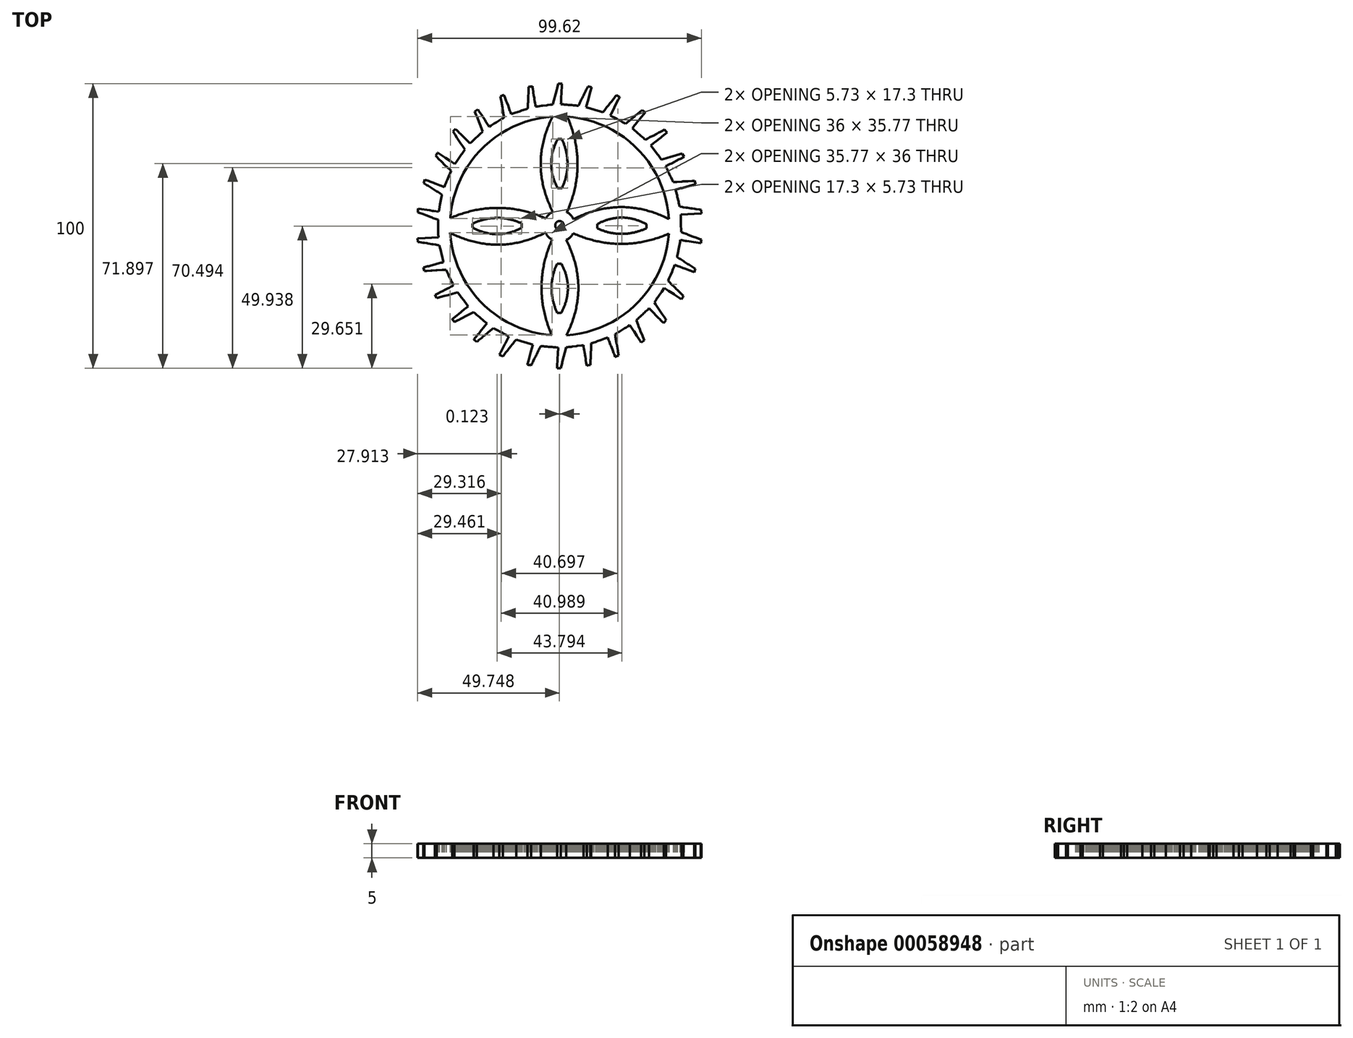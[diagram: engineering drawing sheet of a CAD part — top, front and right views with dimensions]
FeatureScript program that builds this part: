
annotation { "Feature Type Name" : "Feature", "Feature Type Description" : "" }
export const myFeature = defineFeature(function(context is Context, id is Id, definition is map)
    precondition{}
    {
        {
            var Q0;
            Q0=qCreatedBy(makeId("Top.planeOp"),FACE);
            var sketch = newSketch(context, id + "F0", { "sketchPlane" : qUnion([Q0])});
            skLineSegment(sketch, "E0", {"start": v(-36.57, 34.1) * mm, "end": v(-36.87, 33.77) * mm});
            skLineSegment(sketch, "E1", {"start": v(-36.87, 33.77) * mm, "end": v(-37.17, 33.44) * mm});
            skLineSegment(sketch, "E2", {"start": v(-37.17, 33.44) * mm, "end": v(-37.45, 33.13) * mm});
            skLineSegment(sketch, "E3", {"start": v(-37.45, 33.13) * mm, "end": v(-37.2, 32.76) * mm});
            skLineSegment(sketch, "E4", {"start": v(-37.2, 32.76) * mm, "end": v(-36.95, 32.39) * mm});
            skLineSegment(sketch, "E5", {"start": v(-36.95, 32.39) * mm, "end": v(-36.7, 32.02) * mm});
            skLineSegment(sketch, "E6", {"start": v(-36.7, 32.02) * mm, "end": v(-36.46, 31.65) * mm});
            skLineSegment(sketch, "E7", {"start": v(-36.46, 31.65) * mm, "end": v(-36.21, 31.28) * mm});
            skLineSegment(sketch, "E8", {"start": v(-36.21, 31.28) * mm, "end": v(-35.97, 30.9) * mm});
            skLineSegment(sketch, "E9", {"start": v(-35.97, 30.9) * mm, "end": v(-35.72, 30.53) * mm});
            skLineSegment(sketch, "E10", {"start": v(-35.72, 30.53) * mm, "end": v(-35.47, 30.16) * mm});
            skLineSegment(sketch, "E11", {"start": v(-35.47, 30.16) * mm, "end": v(-35.23, 29.8) * mm});
            skLineSegment(sketch, "E12", {"start": v(-35.23, 29.8) * mm, "end": v(-34.98, 29.42) * mm});
            skLineSegment(sketch, "E13", {"start": v(-34.98, 29.42) * mm, "end": v(-34.74, 29.05) * mm});
            skLineSegment(sketch, "E14", {"start": v(-34.74, 29.05) * mm, "end": v(-34.49, 28.68) * mm});
            skLineSegment(sketch, "E15", {"start": v(-34.49, 28.68) * mm, "end": v(-34.24, 28.3) * mm});
            skLineSegment(sketch, "E16", {"start": v(-34.24, 28.3) * mm, "end": v(-34, 27.93) * mm});
            skLineSegment(sketch, "E17", {"start": v(-34, 27.93) * mm, "end": v(-33.75, 27.56) * mm});
            skLineSegment(sketch, "E18", {"start": v(-33.75, 27.56) * mm, "end": v(-33.5, 27.2) * mm});
            skLineSegment(sketch, "E19", {"start": v(-33.5, 27.2) * mm, "end": v(-33.26, 26.83) * mm});
            skLineSegment(sketch, "E20", {"start": v(-33.26, 26.83) * mm, "end": v(-33.51, 26.46) * mm});
            skLineSegment(sketch, "E21", {"start": v(-33.51, 26.46) * mm, "end": v(-33.77, 26.1) * mm});
            skLineSegment(sketch, "E22", {"start": v(-33.77, 26.1) * mm, "end": v(-34.02, 25.73) * mm});
            skLineSegment(sketch, "E23", {"start": v(-34.02, 25.73) * mm, "end": v(-34.28, 25.37) * mm});
            skLineSegment(sketch, "E24", {"start": v(-34.28, 25.37) * mm, "end": v(-34.53, 25) * mm});
            skLineSegment(sketch, "E25", {"start": v(-34.53, 25) * mm, "end": v(-34.79, 24.63) * mm});
            skLineSegment(sketch, "E26", {"start": v(-34.79, 24.63) * mm, "end": v(-35.04, 24.27) * mm});
            skLineSegment(sketch, "E27", {"start": v(-35.04, 24.27) * mm, "end": v(-35.3, 23.9) * mm});
            skLineSegment(sketch, "E28", {"start": v(-35.3, 23.9) * mm, "end": v(-35.55, 23.53) * mm});
            skLineSegment(sketch, "E29", {"start": v(-35.55, 23.53) * mm, "end": v(-35.8, 23.17) * mm});
            skLineSegment(sketch, "E30", {"start": v(-35.8, 23.17) * mm, "end": v(-36.06, 22.8) * mm});
            skLineSegment(sketch, "E31", {"start": v(-36.06, 22.8) * mm, "end": v(-36.31, 22.44) * mm});
            skLineSegment(sketch, "E32", {"start": v(-36.31, 22.44) * mm, "end": v(-36.56, 22.07) * mm});
            skLineSegment(sketch, "E33", {"start": v(-36.56, 22.07) * mm, "end": v(-36.76, 21.8) * mm});
            skLineSegment(sketch, "E34", {"start": v(-36.76, 21.8) * mm, "end": v(-37.13, 22.03) * mm});
            skLineSegment(sketch, "E35", {"start": v(-37.13, 22.03) * mm, "end": v(-37.5, 22.28) * mm});
            skLineSegment(sketch, "E36", {"start": v(-37.5, 22.28) * mm, "end": v(-37.88, 22.52) * mm});
            skLineSegment(sketch, "E37", {"start": v(-37.88, 22.52) * mm, "end": v(-38.25, 22.76) * mm});
            skLineSegment(sketch, "E38", {"start": v(-38.25, 22.76) * mm, "end": v(-38.63, 23) * mm});
            skLineSegment(sketch, "E39", {"start": v(-38.63, 23) * mm, "end": v(-39, 23.25) * mm});
            skLineSegment(sketch, "E40", {"start": v(-39, 23.25) * mm, "end": v(-39.38, 23.49) * mm});
            skLineSegment(sketch, "E41", {"start": v(-39.38, 23.49) * mm, "end": v(-39.75, 23.73) * mm});
            skLineSegment(sketch, "E42", {"start": v(-39.75, 23.73) * mm, "end": v(-40.12, 23.98) * mm});
            skLineSegment(sketch, "E43", {"start": v(-40.12, 23.98) * mm, "end": v(-40.5, 24.22) * mm});
            skLineSegment(sketch, "E44", {"start": v(-40.5, 24.22) * mm, "end": v(-40.87, 24.46) * mm});
            skLineSegment(sketch, "E45", {"start": v(-40.87, 24.46) * mm, "end": v(-41.24, 24.7) * mm});
            skLineSegment(sketch, "E46", {"start": v(-41.24, 24.7) * mm, "end": v(-41.62, 24.95) * mm});
            skLineSegment(sketch, "E47", {"start": v(-41.62, 24.95) * mm, "end": v(-42, 25.19) * mm});
            skLineSegment(sketch, "E48", {"start": v(-42, 25.19) * mm, "end": v(-42.37, 25.43) * mm});
            skLineSegment(sketch, "E49", {"start": v(-42.37, 25.43) * mm, "end": v(-42.74, 25.67) * mm});
            skLineSegment(sketch, "E50", {"start": v(-42.74, 25.67) * mm, "end": v(-42.86, 25.75) * mm});
            skLineSegment(sketch, "E51", {"start": v(-42.86, 25.75) * mm, "end": v(-43.08, 25.37) * mm});
            skLineSegment(sketch, "E52", {"start": v(-43.08, 25.37) * mm, "end": v(-43.3, 24.98) * mm});
            skLineSegment(sketch, "E53", {"start": v(-43.3, 24.98) * mm, "end": v(-43.52, 24.62) * mm});
            skLineSegment(sketch, "E54", {"start": v(-43.52, 24.62) * mm, "end": v(-43.2, 24.3) * mm});
            skLineSegment(sketch, "E55", {"start": v(-43.2, 24.3) * mm, "end": v(-42.88, 24) * mm});
            skLineSegment(sketch, "E56", {"start": v(-42.88, 24) * mm, "end": v(-42.56, 23.69) * mm});
            skLineSegment(sketch, "E57", {"start": v(-42.56, 23.69) * mm, "end": v(-42.24, 23.37) * mm});
            skLineSegment(sketch, "E58", {"start": v(-42.24, 23.37) * mm, "end": v(-41.93, 23.06) * mm});
            skLineSegment(sketch, "E59", {"start": v(-41.93, 23.06) * mm, "end": v(-41.6, 22.75) * mm});
            skLineSegment(sketch, "E60", {"start": v(-41.6, 22.75) * mm, "end": v(-41.29, 22.44) * mm});
            skLineSegment(sketch, "E61", {"start": v(-41.29, 22.44) * mm, "end": v(-40.97, 22.13) * mm});
            skLineSegment(sketch, "E62", {"start": v(-40.97, 22.13) * mm, "end": v(-40.65, 21.82) * mm});
            skLineSegment(sketch, "E63", {"start": v(-40.65, 21.82) * mm, "end": v(-40.33, 21.5) * mm});
            skLineSegment(sketch, "E64", {"start": v(-40.33, 21.5) * mm, "end": v(-40.02, 21.2) * mm});
            skLineSegment(sketch, "E65", {"start": v(-40.02, 21.2) * mm, "end": v(-39.7, 20.88) * mm});
            skLineSegment(sketch, "E66", {"start": v(-39.7, 20.88) * mm, "end": v(-39.38, 20.57) * mm});
            skLineSegment(sketch, "E67", {"start": v(-39.38, 20.57) * mm, "end": v(-39.06, 20.26) * mm});
            skLineSegment(sketch, "E68", {"start": v(-39.06, 20.26) * mm, "end": v(-38.74, 19.94) * mm});
            skLineSegment(sketch, "E69", {"start": v(-38.74, 19.94) * mm, "end": v(-38.42, 19.63) * mm});
            skLineSegment(sketch, "E70", {"start": v(-38.42, 19.63) * mm, "end": v(-38.11, 19.33) * mm});
            skLineSegment(sketch, "E71", {"start": v(-38.11, 19.33) * mm, "end": v(-38.28, 18.92) * mm});
            skLineSegment(sketch, "E72", {"start": v(-38.28, 18.92) * mm, "end": v(-38.46, 18.5) * mm});
            skLineSegment(sketch, "E73", {"start": v(-38.46, 18.5) * mm, "end": v(-38.63, 18.1) * mm});
            skLineSegment(sketch, "E74", {"start": v(-38.63, 18.1) * mm, "end": v(-38.8, 17.68) * mm});
            skLineSegment(sketch, "E75", {"start": v(-38.8, 17.68) * mm, "end": v(-38.97, 17.27) * mm});
            skLineSegment(sketch, "E76", {"start": v(-38.97, 17.27) * mm, "end": v(-39.15, 16.86) * mm});
            skLineSegment(sketch, "E77", {"start": v(-39.15, 16.86) * mm, "end": v(-39.32, 16.45) * mm});
            skLineSegment(sketch, "E78", {"start": v(-39.32, 16.45) * mm, "end": v(-39.5, 16.04) * mm});
            skLineSegment(sketch, "E79", {"start": v(-39.5, 16.04) * mm, "end": v(-39.66, 15.63) * mm});
            skLineSegment(sketch, "E80", {"start": v(-39.66, 15.63) * mm, "end": v(-39.84, 15.22) * mm});
            skLineSegment(sketch, "E81", {"start": v(-39.84, 15.22) * mm, "end": v(-40, 14.8) * mm});
            skLineSegment(sketch, "E82", {"start": v(-40, 14.8) * mm, "end": v(-40.18, 14.4) * mm});
            skLineSegment(sketch, "E83", {"start": v(-40.18, 14.4) * mm, "end": v(-40.35, 13.99) * mm});
            skLineSegment(sketch, "E84", {"start": v(-40.35, 13.99) * mm, "end": v(-40.49, 13.67) * mm});
            skLineSegment(sketch, "E85", {"start": v(-40.49, 13.67) * mm, "end": v(-40.9, 13.83) * mm});
            skLineSegment(sketch, "E86", {"start": v(-40.9, 13.83) * mm, "end": v(-41.32, 14) * mm});
            skLineSegment(sketch, "E87", {"start": v(-41.32, 14) * mm, "end": v(-41.73, 14.15) * mm});
            skLineSegment(sketch, "E88", {"start": v(-41.73, 14.15) * mm, "end": v(-42.15, 14.31) * mm});
            skLineSegment(sketch, "E89", {"start": v(-42.15, 14.31) * mm, "end": v(-42.57, 14.47) * mm});
            skLineSegment(sketch, "E90", {"start": v(-42.57, 14.47) * mm, "end": v(-42.98, 14.63) * mm});
            skLineSegment(sketch, "E91", {"start": v(-42.98, 14.63) * mm, "end": v(-43.4, 14.8) * mm});
            skLineSegment(sketch, "E92", {"start": v(-43.4, 14.8) * mm, "end": v(-43.81, 14.95) * mm});
            skLineSegment(sketch, "E93", {"start": v(-43.81, 14.95) * mm, "end": v(-44.23, 15.1) * mm});
            skLineSegment(sketch, "E94", {"start": v(-44.23, 15.1) * mm, "end": v(-44.65, 15.27) * mm});
            skLineSegment(sketch, "E95", {"start": v(-44.65, 15.27) * mm, "end": v(-45.06, 15.43) * mm});
            skLineSegment(sketch, "E96", {"start": v(-45.06, 15.43) * mm, "end": v(-45.48, 15.59) * mm});
            skLineSegment(sketch, "E97", {"start": v(-45.48, 15.59) * mm, "end": v(-45.9, 15.75) * mm});
            skLineSegment(sketch, "E98", {"start": v(-45.9, 15.75) * mm, "end": v(-46.31, 15.9) * mm});
            skLineSegment(sketch, "E99", {"start": v(-46.31, 15.9) * mm, "end": v(-46.73, 16.07) * mm});
            skLineSegment(sketch, "E100", {"start": v(-46.73, 16.07) * mm, "end": v(-47.14, 16.23) * mm});
            skLineSegment(sketch, "E101", {"start": v(-47.14, 16.23) * mm, "end": v(-47.28, 16.28) * mm});
            skLineSegment(sketch, "E102", {"start": v(-47.28, 16.28) * mm, "end": v(-47.42, 15.86) * mm});
            skLineSegment(sketch, "E103", {"start": v(-47.42, 15.86) * mm, "end": v(-47.56, 15.43) * mm});
            skLineSegment(sketch, "E104", {"start": v(-47.56, 15.43) * mm, "end": v(-47.69, 15.04) * mm});
            skLineSegment(sketch, "E105", {"start": v(-47.69, 15.04) * mm, "end": v(-47.3, 14.8) * mm});
            skLineSegment(sketch, "E106", {"start": v(-47.3, 14.8) * mm, "end": v(-46.93, 14.56) * mm});
            skLineSegment(sketch, "E107", {"start": v(-46.93, 14.56) * mm, "end": v(-46.56, 14.32) * mm});
            skLineSegment(sketch, "E108", {"start": v(-46.56, 14.32) * mm, "end": v(-46.18, 14.08) * mm});
            skLineSegment(sketch, "E109", {"start": v(-46.18, 14.08) * mm, "end": v(-45.8, 13.84) * mm});
            skLineSegment(sketch, "E110", {"start": v(-45.8, 13.84) * mm, "end": v(-45.43, 13.6) * mm});
            skLineSegment(sketch, "E111", {"start": v(-45.43, 13.6) * mm, "end": v(-45.05, 13.36) * mm});
            skLineSegment(sketch, "E112", {"start": v(-45.05, 13.36) * mm, "end": v(-44.68, 13.13) * mm});
            skLineSegment(sketch, "E113", {"start": v(-44.68, 13.13) * mm, "end": v(-44.3, 12.89) * mm});
            skLineSegment(sketch, "E114", {"start": v(-44.3, 12.89) * mm, "end": v(-43.92, 12.65) * mm});
            skLineSegment(sketch, "E115", {"start": v(-43.92, 12.65) * mm, "end": v(-43.55, 12.4) * mm});
            skLineSegment(sketch, "E116", {"start": v(-43.55, 12.4) * mm, "end": v(-43.17, 12.17) * mm});
            skLineSegment(sketch, "E117", {"start": v(-43.17, 12.17) * mm, "end": v(-42.8, 11.93) * mm});
            skLineSegment(sketch, "E118", {"start": v(-42.8, 11.93) * mm, "end": v(-42.42, 11.7) * mm});
            skLineSegment(sketch, "E119", {"start": v(-42.42, 11.7) * mm, "end": v(-42.04, 11.45) * mm});
            skLineSegment(sketch, "E120", {"start": v(-42.04, 11.45) * mm, "end": v(-41.67, 11.22) * mm});
            skLineSegment(sketch, "E121", {"start": v(-41.67, 11.22) * mm, "end": v(-41.3, 10.98) * mm});
            skLineSegment(sketch, "E122", {"start": v(-41.3, 10.98) * mm, "end": v(-41.38, 10.54) * mm});
            skLineSegment(sketch, "E123", {"start": v(-41.38, 10.54) * mm, "end": v(-41.46, 10.1) * mm});
            skLineSegment(sketch, "E124", {"start": v(-41.46, 10.1) * mm, "end": v(-41.55, 9.67) * mm});
            skLineSegment(sketch, "E125", {"start": v(-41.55, 9.67) * mm, "end": v(-41.63, 9.23) * mm});
            skLineSegment(sketch, "E126", {"start": v(-41.63, 9.23) * mm, "end": v(-41.71, 8.8) * mm});
            skLineSegment(sketch, "E127", {"start": v(-41.71, 8.8) * mm, "end": v(-41.8, 8.35) * mm});
            skLineSegment(sketch, "E128", {"start": v(-41.8, 8.35) * mm, "end": v(-41.88, 7.92) * mm});
            skLineSegment(sketch, "E129", {"start": v(-41.88, 7.92) * mm, "end": v(-41.96, 7.48) * mm});
            skLineSegment(sketch, "E130", {"start": v(-41.96, 7.48) * mm, "end": v(-42.05, 7.04) * mm});
            skLineSegment(sketch, "E131", {"start": v(-42.05, 7.04) * mm, "end": v(-42.13, 6.6) * mm});
            skLineSegment(sketch, "E132", {"start": v(-42.13, 6.6) * mm, "end": v(-42.21, 6.17) * mm});
            skLineSegment(sketch, "E133", {"start": v(-42.21, 6.17) * mm, "end": v(-42.3, 5.73) * mm});
            skLineSegment(sketch, "E134", {"start": v(-42.3, 5.73) * mm, "end": v(-42.38, 5.3) * mm});
            skLineSegment(sketch, "E135", {"start": v(-42.38, 5.3) * mm, "end": v(-42.44, 4.96) * mm});
            skLineSegment(sketch, "E136", {"start": v(-42.44, 4.96) * mm, "end": v(-42.88, 5.03) * mm});
            skLineSegment(sketch, "E137", {"start": v(-42.88, 5.03) * mm, "end": v(-43.32, 5.1) * mm});
            skLineSegment(sketch, "E138", {"start": v(-43.32, 5.1) * mm, "end": v(-43.76, 5.16) * mm});
            skLineSegment(sketch, "E139", {"start": v(-43.76, 5.16) * mm, "end": v(-44.2, 5.23) * mm});
            skLineSegment(sketch, "E140", {"start": v(-44.2, 5.23) * mm, "end": v(-44.65, 5.3) * mm});
            skLineSegment(sketch, "E141", {"start": v(-44.65, 5.3) * mm, "end": v(-45.09, 5.37) * mm});
            skLineSegment(sketch, "E142", {"start": v(-45.09, 5.37) * mm, "end": v(-45.53, 5.44) * mm});
            skLineSegment(sketch, "E143", {"start": v(-45.53, 5.44) * mm, "end": v(-45.97, 5.51) * mm});
            skLineSegment(sketch, "E144", {"start": v(-45.97, 5.51) * mm, "end": v(-46.4, 5.58) * mm});
            skLineSegment(sketch, "E145", {"start": v(-46.4, 5.58) * mm, "end": v(-46.85, 5.65) * mm});
            skLineSegment(sketch, "E146", {"start": v(-46.85, 5.65) * mm, "end": v(-47.29, 5.72) * mm});
            skLineSegment(sketch, "E147", {"start": v(-47.29, 5.72) * mm, "end": v(-47.73, 5.8) * mm});
            skLineSegment(sketch, "E148", {"start": v(-47.73, 5.8) * mm, "end": v(-48.17, 5.86) * mm});
            skLineSegment(sketch, "E149", {"start": v(-48.17, 5.86) * mm, "end": v(-48.6, 5.93) * mm});
            skLineSegment(sketch, "E150", {"start": v(-48.6, 5.93) * mm, "end": v(-49.05, 6) * mm});
            skLineSegment(sketch, "E151", {"start": v(-49.05, 6) * mm, "end": v(-49.49, 6.07) * mm});
            skLineSegment(sketch, "E152", {"start": v(-49.49, 6.07) * mm, "end": v(-49.63, 6.1) * mm});
            skLineSegment(sketch, "E153", {"start": v(-49.63, 6.1) * mm, "end": v(-49.68, 5.65) * mm});
            skLineSegment(sketch, "E154", {"start": v(-49.68, 5.65) * mm, "end": v(-49.72, 5.2) * mm});
            skLineSegment(sketch, "E155", {"start": v(-49.72, 5.2) * mm, "end": v(-49.77, 4.8) * mm});
            skLineSegment(sketch, "E156", {"start": v(-49.77, 4.8) * mm, "end": v(-49.35, 4.64) * mm});
            skLineSegment(sketch, "E157", {"start": v(-49.35, 4.64) * mm, "end": v(-48.93, 4.48) * mm});
            skLineSegment(sketch, "E158", {"start": v(-48.93, 4.48) * mm, "end": v(-48.52, 4.33) * mm});
            skLineSegment(sketch, "E159", {"start": v(-48.52, 4.33) * mm, "end": v(-48.1, 4.17) * mm});
            skLineSegment(sketch, "E160", {"start": v(-48.1, 4.17) * mm, "end": v(-47.68, 4.02) * mm});
            skLineSegment(sketch, "E161", {"start": v(-47.68, 4.02) * mm, "end": v(-47.26, 3.86) * mm});
            skLineSegment(sketch, "E162", {"start": v(-47.26, 3.86) * mm, "end": v(-46.85, 3.7) * mm});
            skLineSegment(sketch, "E163", {"start": v(-46.85, 3.7) * mm, "end": v(-46.43, 3.55) * mm});
            skLineSegment(sketch, "E164", {"start": v(-46.43, 3.55) * mm, "end": v(-46.01, 3.4) * mm});
            skLineSegment(sketch, "E165", {"start": v(-46.01, 3.4) * mm, "end": v(-45.6, 3.24) * mm});
            skLineSegment(sketch, "E166", {"start": v(-45.6, 3.24) * mm, "end": v(-45.18, 3.08) * mm});
            skLineSegment(sketch, "E167", {"start": v(-45.18, 3.08) * mm, "end": v(-44.76, 2.93) * mm});
            skLineSegment(sketch, "E168", {"start": v(-44.76, 2.93) * mm, "end": v(-44.34, 2.77) * mm});
            skLineSegment(sketch, "E169", {"start": v(-44.34, 2.77) * mm, "end": v(-43.92, 2.62) * mm});
            skLineSegment(sketch, "E170", {"start": v(-43.92, 2.62) * mm, "end": v(-43.5, 2.46) * mm});
            skLineSegment(sketch, "E171", {"start": v(-43.5, 2.46) * mm, "end": v(-43.09, 2.3) * mm});
            skLineSegment(sketch, "E172", {"start": v(-43.09, 2.3) * mm, "end": v(-42.68, 2.16) * mm});
            skLineSegment(sketch, "E173", {"start": v(-42.68, 2.16) * mm, "end": v(-42.67, 1.7) * mm});
            skLineSegment(sketch, "E174", {"start": v(-42.67, 1.7) * mm, "end": v(-42.66, 1.26) * mm});
            skLineSegment(sketch, "E175", {"start": v(-42.66, 1.26) * mm, "end": v(-42.65, 0.82) * mm});
            skLineSegment(sketch, "E176", {"start": v(-42.65, 0.82) * mm, "end": v(-42.64, 0.37) * mm});
            skLineSegment(sketch, "E177", {"start": v(-42.64, 0.37) * mm, "end": v(-42.63, -0.07) * mm});
            skLineSegment(sketch, "E178", {"start": v(-42.63, -0.07) * mm, "end": v(-42.62, -0.52) * mm});
            skLineSegment(sketch, "E179", {"start": v(-42.62, -0.52) * mm, "end": v(-42.61, -0.96) * mm});
            skLineSegment(sketch, "E180", {"start": v(-42.61, -0.96) * mm, "end": v(-42.6, -1.4) * mm});
            skLineSegment(sketch, "E181", {"start": v(-42.6, -1.4) * mm, "end": v(-42.6, -1.85) * mm});
            skLineSegment(sketch, "E182", {"start": v(-42.6, -1.85) * mm, "end": v(-42.58, -2.3) * mm});
            skLineSegment(sketch, "E183", {"start": v(-42.58, -2.3) * mm, "end": v(-42.57, -2.75) * mm});
            skLineSegment(sketch, "E184", {"start": v(-42.57, -2.75) * mm, "end": v(-42.56, -3.2) * mm});
            skLineSegment(sketch, "E185", {"start": v(-42.56, -3.2) * mm, "end": v(-42.55, -3.64) * mm});
            skLineSegment(sketch, "E186", {"start": v(-42.55, -3.64) * mm, "end": v(-42.55, -3.98) * mm});
            skLineSegment(sketch, "E187", {"start": v(-42.55, -3.98) * mm, "end": v(-43, -4) * mm});
            skLineSegment(sketch, "E188", {"start": v(-43, -4) * mm, "end": v(-43.44, -4.02) * mm});
            skLineSegment(sketch, "E189", {"start": v(-43.44, -4.02) * mm, "end": v(-43.88, -4.05) * mm});
            skLineSegment(sketch, "E190", {"start": v(-43.88, -4.05) * mm, "end": v(-44.33, -4.07) * mm});
            skLineSegment(sketch, "E191", {"start": v(-44.33, -4.07) * mm, "end": v(-44.77, -4.1) * mm});
            skLineSegment(sketch, "E192", {"start": v(-44.77, -4.1) * mm, "end": v(-45.22, -4.12) * mm});
            skLineSegment(sketch, "E193", {"start": v(-45.22, -4.12) * mm, "end": v(-45.66, -4.14) * mm});
            skLineSegment(sketch, "E194", {"start": v(-45.66, -4.14) * mm, "end": v(-46.1, -4.16) * mm});
            skLineSegment(sketch, "E195", {"start": v(-46.1, -4.16) * mm, "end": v(-46.55, -4.19) * mm});
            skLineSegment(sketch, "E196", {"start": v(-46.55, -4.19) * mm, "end": v(-47, -4.21) * mm});
            skLineSegment(sketch, "E197", {"start": v(-47, -4.21) * mm, "end": v(-47.44, -4.23) * mm});
            skLineSegment(sketch, "E198", {"start": v(-47.44, -4.23) * mm, "end": v(-47.89, -4.26) * mm});
            skLineSegment(sketch, "E199", {"start": v(-47.89, -4.26) * mm, "end": v(-48.33, -4.28) * mm});
            skLineSegment(sketch, "E200", {"start": v(-48.33, -4.28) * mm, "end": v(-48.78, -4.3) * mm});
            skLineSegment(sketch, "E201", {"start": v(-48.78, -4.3) * mm, "end": v(-49.22, -4.33) * mm});
            skLineSegment(sketch, "E202", {"start": v(-49.22, -4.33) * mm, "end": v(-49.67, -4.35) * mm});
            skLineSegment(sketch, "E203", {"start": v(-49.67, -4.35) * mm, "end": v(-49.8, -4.36) * mm});
            skLineSegment(sketch, "E204", {"start": v(-49.8, -4.36) * mm, "end": v(-49.77, -4.8) * mm});
            skLineSegment(sketch, "E205", {"start": v(-49.77, -4.8) * mm, "end": v(-49.72, -5.24) * mm});
            skLineSegment(sketch, "E206", {"start": v(-49.72, -5.24) * mm, "end": v(-49.68, -5.66) * mm});
            skLineSegment(sketch, "E207", {"start": v(-49.68, -5.66) * mm, "end": v(-49.24, -5.73) * mm});
            skLineSegment(sketch, "E208", {"start": v(-49.24, -5.73) * mm, "end": v(-48.8, -5.8) * mm});
            skLineSegment(sketch, "E209", {"start": v(-48.8, -5.8) * mm, "end": v(-48.36, -5.86) * mm});
            skLineSegment(sketch, "E210", {"start": v(-48.36, -5.86) * mm, "end": v(-47.92, -5.92) * mm});
            skLineSegment(sketch, "E211", {"start": v(-47.92, -5.92) * mm, "end": v(-47.47, -5.99) * mm});
            skLineSegment(sketch, "E212", {"start": v(-47.47, -5.99) * mm, "end": v(-47.03, -6.05) * mm});
            skLineSegment(sketch, "E213", {"start": v(-47.03, -6.05) * mm, "end": v(-46.6, -6.12) * mm});
            skLineSegment(sketch, "E214", {"start": v(-46.6, -6.12) * mm, "end": v(-46.15, -6.18) * mm});
            skLineSegment(sketch, "E215", {"start": v(-46.15, -6.18) * mm, "end": v(-45.71, -6.25) * mm});
            skLineSegment(sketch, "E216", {"start": v(-45.71, -6.25) * mm, "end": v(-45.27, -6.31) * mm});
            skLineSegment(sketch, "E217", {"start": v(-45.27, -6.31) * mm, "end": v(-44.83, -6.38) * mm});
            skLineSegment(sketch, "E218", {"start": v(-44.83, -6.38) * mm, "end": v(-44.39, -6.44) * mm});
            skLineSegment(sketch, "E219", {"start": v(-44.39, -6.44) * mm, "end": v(-43.95, -6.5) * mm});
            skLineSegment(sketch, "E220", {"start": v(-43.95, -6.5) * mm, "end": v(-43.5, -6.57) * mm});
            skLineSegment(sketch, "E221", {"start": v(-43.5, -6.57) * mm, "end": v(-43.07, -6.64) * mm});
            skLineSegment(sketch, "E222", {"start": v(-43.07, -6.64) * mm, "end": v(-42.63, -6.7) * mm});
            skLineSegment(sketch, "E223", {"start": v(-42.63, -6.7) * mm, "end": v(-42.2, -6.77) * mm});
            skLineSegment(sketch, "E224", {"start": v(-42.2, -6.77) * mm, "end": v(-42.1, -7.2) * mm});
            skLineSegment(sketch, "E225", {"start": v(-42.1, -7.2) * mm, "end": v(-41.99, -7.63) * mm});
            skLineSegment(sketch, "E226", {"start": v(-41.99, -7.63) * mm, "end": v(-41.89, -8.07) * mm});
            skLineSegment(sketch, "E227", {"start": v(-41.89, -8.07) * mm, "end": v(-41.79, -8.5) * mm});
            skLineSegment(sketch, "E228", {"start": v(-41.79, -8.5) * mm, "end": v(-41.68, -8.93) * mm});
            skLineSegment(sketch, "E229", {"start": v(-41.68, -8.93) * mm, "end": v(-41.58, -9.37) * mm});
            skLineSegment(sketch, "E230", {"start": v(-41.58, -9.37) * mm, "end": v(-41.48, -9.8) * mm});
            skLineSegment(sketch, "E231", {"start": v(-41.48, -9.8) * mm, "end": v(-41.38, -10.24) * mm});
            skLineSegment(sketch, "E232", {"start": v(-41.38, -10.24) * mm, "end": v(-41.28, -10.67) * mm});
            skLineSegment(sketch, "E233", {"start": v(-41.28, -10.67) * mm, "end": v(-41.17, -11.1) * mm});
            skLineSegment(sketch, "E234", {"start": v(-41.17, -11.1) * mm, "end": v(-41.07, -11.54) * mm});
            skLineSegment(sketch, "E235", {"start": v(-41.07, -11.54) * mm, "end": v(-40.97, -11.97) * mm});
            skLineSegment(sketch, "E236", {"start": v(-40.97, -11.97) * mm, "end": v(-40.87, -12.4) * mm});
            skLineSegment(sketch, "E237", {"start": v(-40.87, -12.4) * mm, "end": v(-40.8, -12.74) * mm});
            skLineSegment(sketch, "E238", {"start": v(-40.8, -12.74) * mm, "end": v(-41.22, -12.85) * mm});
            skLineSegment(sketch, "E239", {"start": v(-41.22, -12.85) * mm, "end": v(-41.65, -12.97) * mm});
            skLineSegment(sketch, "E240", {"start": v(-41.65, -12.97) * mm, "end": v(-42.08, -13.08) * mm});
            skLineSegment(sketch, "E241", {"start": v(-42.08, -13.08) * mm, "end": v(-42.51, -13.2) * mm});
            skLineSegment(sketch, "E242", {"start": v(-42.51, -13.2) * mm, "end": v(-42.94, -13.31) * mm});
            skLineSegment(sketch, "E243", {"start": v(-42.94, -13.31) * mm, "end": v(-43.37, -13.43) * mm});
            skLineSegment(sketch, "E244", {"start": v(-43.37, -13.43) * mm, "end": v(-43.8, -13.54) * mm});
            skLineSegment(sketch, "E245", {"start": v(-43.8, -13.54) * mm, "end": v(-44.23, -13.66) * mm});
            skLineSegment(sketch, "E246", {"start": v(-44.23, -13.66) * mm, "end": v(-44.66, -13.77) * mm});
            skLineSegment(sketch, "E247", {"start": v(-44.66, -13.77) * mm, "end": v(-45.1, -13.89) * mm});
            skLineSegment(sketch, "E248", {"start": v(-45.1, -13.89) * mm, "end": v(-45.53, -14) * mm});
            skLineSegment(sketch, "E249", {"start": v(-45.53, -14) * mm, "end": v(-45.96, -14.12) * mm});
            skLineSegment(sketch, "E250", {"start": v(-45.96, -14.12) * mm, "end": v(-46.39, -14.24) * mm});
            skLineSegment(sketch, "E251", {"start": v(-46.39, -14.24) * mm, "end": v(-46.82, -14.35) * mm});
            skLineSegment(sketch, "E252", {"start": v(-46.82, -14.35) * mm, "end": v(-47.25, -14.47) * mm});
            skLineSegment(sketch, "E253", {"start": v(-47.25, -14.47) * mm, "end": v(-47.68, -14.58) * mm});
            skLineSegment(sketch, "E254", {"start": v(-47.68, -14.58) * mm, "end": v(-47.82, -14.62) * mm});
            skLineSegment(sketch, "E255", {"start": v(-47.82, -14.62) * mm, "end": v(-47.68, -15.04) * mm});
            skLineSegment(sketch, "E256", {"start": v(-47.68, -15.04) * mm, "end": v(-47.54, -15.47) * mm});
            skLineSegment(sketch, "E257", {"start": v(-47.54, -15.47) * mm, "end": v(-47.42, -15.87) * mm});
            skLineSegment(sketch, "E258", {"start": v(-47.42, -15.87) * mm, "end": v(-46.97, -15.84) * mm});
            skLineSegment(sketch, "E259", {"start": v(-46.97, -15.84) * mm, "end": v(-46.53, -15.8) * mm});
            skLineSegment(sketch, "E260", {"start": v(-46.53, -15.8) * mm, "end": v(-46.08, -15.78) * mm});
            skLineSegment(sketch, "E261", {"start": v(-46.08, -15.78) * mm, "end": v(-45.64, -15.75) * mm});
            skLineSegment(sketch, "E262", {"start": v(-45.64, -15.75) * mm, "end": v(-45.2, -15.73) * mm});
            skLineSegment(sketch, "E263", {"start": v(-45.2, -15.73) * mm, "end": v(-44.75, -15.7) * mm});
            skLineSegment(sketch, "E264", {"start": v(-44.75, -15.7) * mm, "end": v(-44.3, -15.67) * mm});
            skLineSegment(sketch, "E265", {"start": v(-44.3, -15.67) * mm, "end": v(-43.86, -15.64) * mm});
            skLineSegment(sketch, "E266", {"start": v(-43.86, -15.64) * mm, "end": v(-43.41, -15.61) * mm});
            skLineSegment(sketch, "E267", {"start": v(-43.41, -15.61) * mm, "end": v(-42.97, -15.59) * mm});
            skLineSegment(sketch, "E268", {"start": v(-42.97, -15.59) * mm, "end": v(-42.52, -15.56) * mm});
            skLineSegment(sketch, "E269", {"start": v(-42.52, -15.56) * mm, "end": v(-42.08, -15.53) * mm});
            skLineSegment(sketch, "E270", {"start": v(-42.08, -15.53) * mm, "end": v(-41.63, -15.5) * mm});
            skLineSegment(sketch, "E271", {"start": v(-41.63, -15.5) * mm, "end": v(-41.19, -15.47) * mm});
            skLineSegment(sketch, "E272", {"start": v(-41.19, -15.47) * mm, "end": v(-40.75, -15.45) * mm});
            skLineSegment(sketch, "E273", {"start": v(-40.75, -15.45) * mm, "end": v(-40.3, -15.42) * mm});
            skLineSegment(sketch, "E274", {"start": v(-40.3, -15.42) * mm, "end": v(-39.87, -15.39) * mm});
            skLineSegment(sketch, "E275", {"start": v(-39.87, -15.39) * mm, "end": v(-39.68, -15.8) * mm});
            skLineSegment(sketch, "E276", {"start": v(-39.68, -15.8) * mm, "end": v(-39.49, -16.2) * mm});
            skLineSegment(sketch, "E277", {"start": v(-39.49, -16.2) * mm, "end": v(-39.3, -16.6) * mm});
            skLineSegment(sketch, "E278", {"start": v(-39.3, -16.6) * mm, "end": v(-39.1, -17) * mm});
            skLineSegment(sketch, "E279", {"start": v(-39.1, -17) * mm, "end": v(-38.92, -17.4) * mm});
            skLineSegment(sketch, "E280", {"start": v(-38.92, -17.4) * mm, "end": v(-38.73, -17.8) * mm});
            skLineSegment(sketch, "E281", {"start": v(-38.73, -17.8) * mm, "end": v(-38.54, -18.21) * mm});
            skLineSegment(sketch, "E282", {"start": v(-38.54, -18.21) * mm, "end": v(-38.35, -18.61) * mm});
            skLineSegment(sketch, "E283", {"start": v(-38.35, -18.61) * mm, "end": v(-38.16, -19.02) * mm});
            skLineSegment(sketch, "E284", {"start": v(-38.16, -19.02) * mm, "end": v(-37.97, -19.42) * mm});
            skLineSegment(sketch, "E285", {"start": v(-37.97, -19.42) * mm, "end": v(-37.78, -19.82) * mm});
            skLineSegment(sketch, "E286", {"start": v(-37.78, -19.82) * mm, "end": v(-37.59, -20.23) * mm});
            skLineSegment(sketch, "E287", {"start": v(-37.59, -20.23) * mm, "end": v(-37.4, -20.63) * mm});
            skLineSegment(sketch, "E288", {"start": v(-37.4, -20.63) * mm, "end": v(-37.25, -20.94) * mm});
            skLineSegment(sketch, "E289", {"start": v(-37.25, -20.94) * mm, "end": v(-37.65, -21.14) * mm});
            skLineSegment(sketch, "E290", {"start": v(-37.65, -21.14) * mm, "end": v(-38.05, -21.34) * mm});
            skLineSegment(sketch, "E291", {"start": v(-38.05, -21.34) * mm, "end": v(-38.44, -21.55) * mm});
            skLineSegment(sketch, "E292", {"start": v(-38.44, -21.55) * mm, "end": v(-38.84, -21.75) * mm});
            skLineSegment(sketch, "E293", {"start": v(-38.84, -21.75) * mm, "end": v(-39.24, -21.95) * mm});
            skLineSegment(sketch, "E294", {"start": v(-39.24, -21.95) * mm, "end": v(-39.63, -22.15) * mm});
            skLineSegment(sketch, "E295", {"start": v(-39.63, -22.15) * mm, "end": v(-40.03, -22.35) * mm});
            skLineSegment(sketch, "E296", {"start": v(-40.03, -22.35) * mm, "end": v(-40.43, -22.56) * mm});
            skLineSegment(sketch, "E297", {"start": v(-40.43, -22.56) * mm, "end": v(-40.82, -22.76) * mm});
            skLineSegment(sketch, "E298", {"start": v(-40.82, -22.76) * mm, "end": v(-41.22, -22.96) * mm});
            skLineSegment(sketch, "E299", {"start": v(-41.22, -22.96) * mm, "end": v(-41.62, -23.16) * mm});
            skLineSegment(sketch, "E300", {"start": v(-41.62, -23.16) * mm, "end": v(-42.02, -23.37) * mm});
            skLineSegment(sketch, "E301", {"start": v(-42.02, -23.37) * mm, "end": v(-42.41, -23.57) * mm});
            skLineSegment(sketch, "E302", {"start": v(-42.41, -23.57) * mm, "end": v(-42.8, -23.77) * mm});
            skLineSegment(sketch, "E303", {"start": v(-42.8, -23.77) * mm, "end": v(-43.2, -23.97) * mm});
            skLineSegment(sketch, "E304", {"start": v(-43.2, -23.97) * mm, "end": v(-43.6, -24.18) * mm});
            skLineSegment(sketch, "E305", {"start": v(-43.6, -24.18) * mm, "end": v(-43.73, -24.24) * mm});
            skLineSegment(sketch, "E306", {"start": v(-43.73, -24.24) * mm, "end": v(-43.5, -24.63) * mm});
            skLineSegment(sketch, "E307", {"start": v(-43.5, -24.63) * mm, "end": v(-43.29, -25.01) * mm});
            skLineSegment(sketch, "E308", {"start": v(-43.29, -25.01) * mm, "end": v(-43.08, -25.38) * mm});
            skLineSegment(sketch, "E309", {"start": v(-43.08, -25.38) * mm, "end": v(-42.65, -25.26) * mm});
            skLineSegment(sketch, "E310", {"start": v(-42.65, -25.26) * mm, "end": v(-42.22, -25.14) * mm});
            skLineSegment(sketch, "E311", {"start": v(-42.22, -25.14) * mm, "end": v(-41.8, -25.02) * mm});
            skLineSegment(sketch, "E312", {"start": v(-41.8, -25.02) * mm, "end": v(-41.36, -24.9) * mm});
            skLineSegment(sketch, "E313", {"start": v(-41.36, -24.9) * mm, "end": v(-40.94, -24.78) * mm});
            skLineSegment(sketch, "E314", {"start": v(-40.94, -24.78) * mm, "end": v(-40.5, -24.66) * mm});
            skLineSegment(sketch, "E315", {"start": v(-40.5, -24.66) * mm, "end": v(-40.08, -24.54) * mm});
            skLineSegment(sketch, "E316", {"start": v(-40.08, -24.54) * mm, "end": v(-39.65, -24.42) * mm});
            skLineSegment(sketch, "E317", {"start": v(-39.65, -24.42) * mm, "end": v(-39.22, -24.3) * mm});
            skLineSegment(sketch, "E318", {"start": v(-39.22, -24.3) * mm, "end": v(-38.79, -24.18) * mm});
            skLineSegment(sketch, "E319", {"start": v(-38.79, -24.18) * mm, "end": v(-38.36, -24.06) * mm});
            skLineSegment(sketch, "E320", {"start": v(-38.36, -24.06) * mm, "end": v(-37.93, -23.94) * mm});
            skLineSegment(sketch, "E321", {"start": v(-37.93, -23.94) * mm, "end": v(-37.5, -23.82) * mm});
            skLineSegment(sketch, "E322", {"start": v(-37.5, -23.82) * mm, "end": v(-37.07, -23.7) * mm});
            skLineSegment(sketch, "E323", {"start": v(-37.07, -23.7) * mm, "end": v(-36.64, -23.58) * mm});
            skLineSegment(sketch, "E324", {"start": v(-36.64, -23.58) * mm, "end": v(-36.21, -23.46) * mm});
            skLineSegment(sketch, "E325", {"start": v(-36.21, -23.46) * mm, "end": v(-35.8, -23.34) * mm});
            skLineSegment(sketch, "E326", {"start": v(-35.8, -23.34) * mm, "end": v(-35.52, -23.7) * mm});
            skLineSegment(sketch, "E327", {"start": v(-35.52, -23.7) * mm, "end": v(-35.26, -24.05) * mm});
            skLineSegment(sketch, "E328", {"start": v(-35.26, -24.05) * mm, "end": v(-34.99, -24.4) * mm});
            skLineSegment(sketch, "E329", {"start": v(-34.99, -24.4) * mm, "end": v(-34.72, -24.76) * mm});
            skLineSegment(sketch, "E330", {"start": v(-34.72, -24.76) * mm, "end": v(-34.45, -25.12) * mm});
            skLineSegment(sketch, "E331", {"start": v(-34.45, -25.12) * mm, "end": v(-34.18, -25.47) * mm});
            skLineSegment(sketch, "E332", {"start": v(-34.18, -25.47) * mm, "end": v(-33.9, -25.83) * mm});
            skLineSegment(sketch, "E333", {"start": v(-33.9, -25.83) * mm, "end": v(-33.64, -26.18) * mm});
            skLineSegment(sketch, "E334", {"start": v(-33.64, -26.18) * mm, "end": v(-33.37, -26.54) * mm});
            skLineSegment(sketch, "E335", {"start": v(-33.37, -26.54) * mm, "end": v(-33.1, -26.9) * mm});
            skLineSegment(sketch, "E336", {"start": v(-33.1, -26.9) * mm, "end": v(-32.83, -27.25) * mm});
            skLineSegment(sketch, "E337", {"start": v(-32.83, -27.25) * mm, "end": v(-32.56, -27.6) * mm});
            skLineSegment(sketch, "E338", {"start": v(-32.56, -27.6) * mm, "end": v(-32.29, -27.95) * mm});
            skLineSegment(sketch, "E339", {"start": v(-32.29, -27.95) * mm, "end": v(-32.08, -28.23) * mm});
            skLineSegment(sketch, "E340", {"start": v(-32.08, -28.23) * mm, "end": v(-32.43, -28.5) * mm});
            skLineSegment(sketch, "E341", {"start": v(-32.43, -28.5) * mm, "end": v(-32.78, -28.79) * mm});
            skLineSegment(sketch, "E342", {"start": v(-32.78, -28.79) * mm, "end": v(-33.12, -29.07) * mm});
            skLineSegment(sketch, "E343", {"start": v(-33.12, -29.07) * mm, "end": v(-33.47, -29.35) * mm});
            skLineSegment(sketch, "E344", {"start": v(-33.47, -29.35) * mm, "end": v(-33.82, -29.63) * mm});
            skLineSegment(sketch, "E345", {"start": v(-33.82, -29.63) * mm, "end": v(-34.16, -29.9) * mm});
            skLineSegment(sketch, "E346", {"start": v(-34.16, -29.9) * mm, "end": v(-34.5, -30.19) * mm});
            skLineSegment(sketch, "E347", {"start": v(-34.5, -30.19) * mm, "end": v(-34.85, -30.47) * mm});
            skLineSegment(sketch, "E348", {"start": v(-34.85, -30.47) * mm, "end": v(-35.2, -30.75) * mm});
            skLineSegment(sketch, "E349", {"start": v(-35.2, -30.75) * mm, "end": v(-35.55, -31.03) * mm});
            skLineSegment(sketch, "E350", {"start": v(-35.55, -31.03) * mm, "end": v(-35.9, -31.31) * mm});
            skLineSegment(sketch, "E351", {"start": v(-35.9, -31.31) * mm, "end": v(-36.24, -31.6) * mm});
            skLineSegment(sketch, "E352", {"start": v(-36.24, -31.6) * mm, "end": v(-36.59, -31.87) * mm});
            skLineSegment(sketch, "E353", {"start": v(-36.59, -31.87) * mm, "end": v(-36.93, -32.15) * mm});
            skLineSegment(sketch, "E354", {"start": v(-36.93, -32.15) * mm, "end": v(-37.28, -32.43) * mm});
            skLineSegment(sketch, "E355", {"start": v(-37.28, -32.43) * mm, "end": v(-37.62, -32.71) * mm});
            skLineSegment(sketch, "E356", {"start": v(-37.62, -32.71) * mm, "end": v(-37.74, -32.8) * mm});
            skLineSegment(sketch, "E357", {"start": v(-37.74, -32.8) * mm, "end": v(-37.44, -33.14) * mm});
            skLineSegment(sketch, "E358", {"start": v(-37.44, -33.14) * mm, "end": v(-37.14, -33.47) * mm});
            skLineSegment(sketch, "E359", {"start": v(-37.14, -33.47) * mm, "end": v(-36.86, -33.78) * mm});
            skLineSegment(sketch, "E360", {"start": v(-36.86, -33.78) * mm, "end": v(-36.47, -33.57) * mm});
            skLineSegment(sketch, "E361", {"start": v(-36.47, -33.57) * mm, "end": v(-36.07, -33.37) * mm});
            skLineSegment(sketch, "E362", {"start": v(-36.07, -33.37) * mm, "end": v(-35.68, -33.16) * mm});
            skLineSegment(sketch, "E363", {"start": v(-35.68, -33.16) * mm, "end": v(-35.28, -32.95) * mm});
            skLineSegment(sketch, "E364", {"start": v(-35.28, -32.95) * mm, "end": v(-34.89, -32.75) * mm});
            skLineSegment(sketch, "E365", {"start": v(-34.89, -32.75) * mm, "end": v(-34.5, -32.54) * mm});
            skLineSegment(sketch, "E366", {"start": v(-34.5, -32.54) * mm, "end": v(-34.1, -32.33) * mm});
            skLineSegment(sketch, "E367", {"start": v(-34.1, -32.33) * mm, "end": v(-33.7, -32.13) * mm});
            skLineSegment(sketch, "E368", {"start": v(-33.7, -32.13) * mm, "end": v(-33.3, -31.92) * mm});
            skLineSegment(sketch, "E369", {"start": v(-33.3, -31.92) * mm, "end": v(-32.91, -31.71) * mm});
            skLineSegment(sketch, "E370", {"start": v(-32.91, -31.71) * mm, "end": v(-32.52, -31.5) * mm});
            skLineSegment(sketch, "E371", {"start": v(-32.52, -31.5) * mm, "end": v(-32.12, -31.3) * mm});
            skLineSegment(sketch, "E372", {"start": v(-32.12, -31.3) * mm, "end": v(-31.73, -31.1) * mm});
            skLineSegment(sketch, "E373", {"start": v(-31.73, -31.1) * mm, "end": v(-31.34, -30.89) * mm});
            skLineSegment(sketch, "E374", {"start": v(-31.34, -30.89) * mm, "end": v(-30.94, -30.68) * mm});
            skLineSegment(sketch, "E375", {"start": v(-30.94, -30.68) * mm, "end": v(-30.55, -30.48) * mm});
            skLineSegment(sketch, "E376", {"start": v(-30.55, -30.48) * mm, "end": v(-30.16, -30.27) * mm});
            skLineSegment(sketch, "E377", {"start": v(-30.16, -30.27) * mm, "end": v(-29.82, -30.57) * mm});
            skLineSegment(sketch, "E378", {"start": v(-29.82, -30.57) * mm, "end": v(-29.48, -30.86) * mm});
            skLineSegment(sketch, "E379", {"start": v(-29.48, -30.86) * mm, "end": v(-29.15, -31.15) * mm});
            skLineSegment(sketch, "E380", {"start": v(-29.15, -31.15) * mm, "end": v(-28.8, -31.44) * mm});
            skLineSegment(sketch, "E381", {"start": v(-28.8, -31.44) * mm, "end": v(-28.47, -31.73) * mm});
            skLineSegment(sketch, "E382", {"start": v(-28.47, -31.73) * mm, "end": v(-28.13, -32.02) * mm});
            skLineSegment(sketch, "E383", {"start": v(-28.13, -32.02) * mm, "end": v(-27.8, -32.31) * mm});
            skLineSegment(sketch, "E384", {"start": v(-27.8, -32.31) * mm, "end": v(-27.46, -32.6) * mm});
            skLineSegment(sketch, "E385", {"start": v(-27.46, -32.6) * mm, "end": v(-27.12, -32.9) * mm});
            skLineSegment(sketch, "E386", {"start": v(-27.12, -32.9) * mm, "end": v(-26.78, -33.18) * mm});
            skLineSegment(sketch, "E387", {"start": v(-26.78, -33.18) * mm, "end": v(-26.45, -33.48) * mm});
            skLineSegment(sketch, "E388", {"start": v(-26.45, -33.48) * mm, "end": v(-26.1, -33.77) * mm});
            skLineSegment(sketch, "E389", {"start": v(-26.1, -33.77) * mm, "end": v(-25.77, -34.06) * mm});
            skLineSegment(sketch, "E390", {"start": v(-25.77, -34.06) * mm, "end": v(-25.51, -34.28) * mm});
            skLineSegment(sketch, "E391", {"start": v(-25.51, -34.28) * mm, "end": v(-25.8, -34.63) * mm});
            skLineSegment(sketch, "E392", {"start": v(-25.8, -34.63) * mm, "end": v(-26.07, -34.97) * mm});
            skLineSegment(sketch, "E393", {"start": v(-26.07, -34.97) * mm, "end": v(-26.36, -35.32) * mm});
            skLineSegment(sketch, "E394", {"start": v(-26.36, -35.32) * mm, "end": v(-26.64, -35.67) * mm});
            skLineSegment(sketch, "E395", {"start": v(-26.64, -35.67) * mm, "end": v(-26.92, -36.01) * mm});
            skLineSegment(sketch, "E396", {"start": v(-26.92, -36.01) * mm, "end": v(-27.2, -36.36) * mm});
            skLineSegment(sketch, "E397", {"start": v(-27.2, -36.36) * mm, "end": v(-27.48, -36.7) * mm});
            skLineSegment(sketch, "E398", {"start": v(-27.48, -36.7) * mm, "end": v(-27.76, -37.05) * mm});
            skLineSegment(sketch, "E399", {"start": v(-27.76, -37.05) * mm, "end": v(-28.04, -37.4) * mm});
            skLineSegment(sketch, "E400", {"start": v(-28.04, -37.4) * mm, "end": v(-28.32, -37.74) * mm});
            skLineSegment(sketch, "E401", {"start": v(-28.32, -37.74) * mm, "end": v(-28.6, -38.09) * mm});
            skLineSegment(sketch, "E402", {"start": v(-28.6, -38.09) * mm, "end": v(-28.88, -38.44) * mm});
            skLineSegment(sketch, "E403", {"start": v(-28.88, -38.44) * mm, "end": v(-29.16, -38.78) * mm});
            skLineSegment(sketch, "E404", {"start": v(-29.16, -38.78) * mm, "end": v(-29.44, -39.13) * mm});
            skLineSegment(sketch, "E405", {"start": v(-29.44, -39.13) * mm, "end": v(-29.72, -39.47) * mm});
            skLineSegment(sketch, "E406", {"start": v(-29.72, -39.47) * mm, "end": v(-30, -39.82) * mm});
            skLineSegment(sketch, "E407", {"start": v(-30, -39.82) * mm, "end": v(-30.1, -39.93) * mm});
            skLineSegment(sketch, "E408", {"start": v(-30.1, -39.93) * mm, "end": v(-29.73, -40.2) * mm});
            skLineSegment(sketch, "E409", {"start": v(-29.73, -40.2) * mm, "end": v(-29.37, -40.46) * mm});
            skLineSegment(sketch, "E410", {"start": v(-29.37, -40.46) * mm, "end": v(-29.04, -40.7) * mm});
            skLineSegment(sketch, "E411", {"start": v(-29.04, -40.7) * mm, "end": v(-28.7, -40.42) * mm});
            skLineSegment(sketch, "E412", {"start": v(-28.7, -40.42) * mm, "end": v(-28.35, -40.14) * mm});
            skLineSegment(sketch, "E413", {"start": v(-28.35, -40.14) * mm, "end": v(-28, -39.85) * mm});
            skLineSegment(sketch, "E414", {"start": v(-28, -39.85) * mm, "end": v(-27.66, -39.57) * mm});
            skLineSegment(sketch, "E415", {"start": v(-27.66, -39.57) * mm, "end": v(-27.32, -39.29) * mm});
            skLineSegment(sketch, "E416", {"start": v(-27.32, -39.29) * mm, "end": v(-26.98, -39) * mm});
            skLineSegment(sketch, "E417", {"start": v(-26.98, -39) * mm, "end": v(-26.63, -38.72) * mm});
            skLineSegment(sketch, "E418", {"start": v(-26.63, -38.72) * mm, "end": v(-26.29, -38.43) * mm});
            skLineSegment(sketch, "E419", {"start": v(-26.29, -38.43) * mm, "end": v(-25.94, -38.15) * mm});
            skLineSegment(sketch, "E420", {"start": v(-25.94, -38.15) * mm, "end": v(-25.6, -37.87) * mm});
            skLineSegment(sketch, "E421", {"start": v(-25.6, -37.87) * mm, "end": v(-25.26, -37.58) * mm});
            skLineSegment(sketch, "E422", {"start": v(-25.26, -37.58) * mm, "end": v(-24.91, -37.3) * mm});
            skLineSegment(sketch, "E423", {"start": v(-24.91, -37.3) * mm, "end": v(-24.57, -37.01) * mm});
            skLineSegment(sketch, "E424", {"start": v(-24.57, -37.01) * mm, "end": v(-24.23, -36.73) * mm});
            skLineSegment(sketch, "E425", {"start": v(-24.23, -36.73) * mm, "end": v(-23.88, -36.44) * mm});
            skLineSegment(sketch, "E426", {"start": v(-23.88, -36.44) * mm, "end": v(-23.54, -36.16) * mm});
            skLineSegment(sketch, "E427", {"start": v(-23.54, -36.16) * mm, "end": v(-23.2, -35.88) * mm});
            skLineSegment(sketch, "E428", {"start": v(-23.2, -35.88) * mm, "end": v(-22.82, -36.1) * mm});
            skLineSegment(sketch, "E429", {"start": v(-22.82, -36.1) * mm, "end": v(-22.42, -36.31) * mm});
            skLineSegment(sketch, "E430", {"start": v(-22.42, -36.31) * mm, "end": v(-22.03, -36.53) * mm});
            skLineSegment(sketch, "E431", {"start": v(-22.03, -36.53) * mm, "end": v(-21.64, -36.74) * mm});
            skLineSegment(sketch, "E432", {"start": v(-21.64, -36.74) * mm, "end": v(-21.25, -36.96) * mm});
            skLineSegment(sketch, "E433", {"start": v(-21.25, -36.96) * mm, "end": v(-20.86, -37.17) * mm});
            skLineSegment(sketch, "E434", {"start": v(-20.86, -37.17) * mm, "end": v(-20.47, -37.38) * mm});
            skLineSegment(sketch, "E435", {"start": v(-20.47, -37.38) * mm, "end": v(-20.08, -37.6) * mm});
            skLineSegment(sketch, "E436", {"start": v(-20.08, -37.6) * mm, "end": v(-19.7, -37.81) * mm});
            skLineSegment(sketch, "E437", {"start": v(-19.7, -37.81) * mm, "end": v(-19.3, -38.03) * mm});
            skLineSegment(sketch, "E438", {"start": v(-19.3, -38.03) * mm, "end": v(-18.9, -38.24) * mm});
            skLineSegment(sketch, "E439", {"start": v(-18.9, -38.24) * mm, "end": v(-18.52, -38.46) * mm});
            skLineSegment(sketch, "E440", {"start": v(-18.52, -38.46) * mm, "end": v(-18.13, -38.67) * mm});
            skLineSegment(sketch, "E441", {"start": v(-18.13, -38.67) * mm, "end": v(-17.83, -38.84) * mm});
            skLineSegment(sketch, "E442", {"start": v(-17.83, -38.84) * mm, "end": v(-18.03, -39.23) * mm});
            skLineSegment(sketch, "E443", {"start": v(-18.03, -39.23) * mm, "end": v(-18.23, -39.63) * mm});
            skLineSegment(sketch, "E444", {"start": v(-18.23, -39.63) * mm, "end": v(-18.44, -40.03) * mm});
            skLineSegment(sketch, "E445", {"start": v(-18.44, -40.03) * mm, "end": v(-18.64, -40.42) * mm});
            skLineSegment(sketch, "E446", {"start": v(-18.64, -40.42) * mm, "end": v(-18.84, -40.82) * mm});
            skLineSegment(sketch, "E447", {"start": v(-18.84, -40.82) * mm, "end": v(-19.04, -41.22) * mm});
            skLineSegment(sketch, "E448", {"start": v(-19.04, -41.22) * mm, "end": v(-19.25, -41.61) * mm});
            skLineSegment(sketch, "E449", {"start": v(-19.25, -41.61) * mm, "end": v(-19.45, -42.01) * mm});
            skLineSegment(sketch, "E450", {"start": v(-19.45, -42.01) * mm, "end": v(-19.65, -42.4) * mm});
            skLineSegment(sketch, "E451", {"start": v(-19.65, -42.4) * mm, "end": v(-19.85, -42.8) * mm});
            skLineSegment(sketch, "E452", {"start": v(-19.85, -42.8) * mm, "end": v(-20.05, -43.2) * mm});
            skLineSegment(sketch, "E453", {"start": v(-20.05, -43.2) * mm, "end": v(-20.26, -43.6) * mm});
            skLineSegment(sketch, "E454", {"start": v(-20.26, -43.6) * mm, "end": v(-20.46, -44) * mm});
            skLineSegment(sketch, "E455", {"start": v(-20.46, -44) * mm, "end": v(-20.66, -44.4) * mm});
            skLineSegment(sketch, "E456", {"start": v(-20.66, -44.4) * mm, "end": v(-20.86, -44.8) * mm});
            skLineSegment(sketch, "E457", {"start": v(-20.86, -44.8) * mm, "end": v(-21.07, -45.19) * mm});
            skLineSegment(sketch, "E458", {"start": v(-21.07, -45.19) * mm, "end": v(-21.13, -45.32) * mm});
            skLineSegment(sketch, "E459", {"start": v(-21.13, -45.32) * mm, "end": v(-20.72, -45.5) * mm});
            skLineSegment(sketch, "E460", {"start": v(-20.72, -45.5) * mm, "end": v(-20.32, -45.68) * mm});
            skLineSegment(sketch, "E461", {"start": v(-20.32, -45.68) * mm, "end": v(-19.94, -45.85) * mm});
            skLineSegment(sketch, "E462", {"start": v(-19.94, -45.85) * mm, "end": v(-19.66, -45.5) * mm});
            skLineSegment(sketch, "E463", {"start": v(-19.66, -45.5) * mm, "end": v(-19.38, -45.15) * mm});
            skLineSegment(sketch, "E464", {"start": v(-19.38, -45.15) * mm, "end": v(-19.1, -44.8) * mm});
            skLineSegment(sketch, "E465", {"start": v(-19.1, -44.8) * mm, "end": v(-18.83, -44.46) * mm});
            skLineSegment(sketch, "E466", {"start": v(-18.83, -44.46) * mm, "end": v(-18.55, -44.1) * mm});
            skLineSegment(sketch, "E467", {"start": v(-18.55, -44.1) * mm, "end": v(-18.28, -43.76) * mm});
            skLineSegment(sketch, "E468", {"start": v(-18.28, -43.76) * mm, "end": v(-18, -43.4) * mm});
            skLineSegment(sketch, "E469", {"start": v(-18, -43.4) * mm, "end": v(-17.72, -43.06) * mm});
            skLineSegment(sketch, "E470", {"start": v(-17.72, -43.06) * mm, "end": v(-17.45, -42.7) * mm});
            skLineSegment(sketch, "E471", {"start": v(-17.45, -42.7) * mm, "end": v(-17.17, -42.36) * mm});
            skLineSegment(sketch, "E472", {"start": v(-17.17, -42.36) * mm, "end": v(-16.9, -42.01) * mm});
            skLineSegment(sketch, "E473", {"start": v(-16.9, -42.01) * mm, "end": v(-16.62, -41.66) * mm});
            skLineSegment(sketch, "E474", {"start": v(-16.62, -41.66) * mm, "end": v(-16.34, -41.31) * mm});
            skLineSegment(sketch, "E475", {"start": v(-16.34, -41.31) * mm, "end": v(-16.06, -40.96) * mm});
            skLineSegment(sketch, "E476", {"start": v(-16.06, -40.96) * mm, "end": v(-15.79, -40.61) * mm});
            skLineSegment(sketch, "E477", {"start": v(-15.79, -40.61) * mm, "end": v(-15.5, -40.27) * mm});
            skLineSegment(sketch, "E478", {"start": v(-15.5, -40.27) * mm, "end": v(-15.24, -39.92) * mm});
            skLineSegment(sketch, "E479", {"start": v(-15.24, -39.92) * mm, "end": v(-14.81, -40.05) * mm});
            skLineSegment(sketch, "E480", {"start": v(-14.81, -40.05) * mm, "end": v(-14.38, -40.18) * mm});
            skLineSegment(sketch, "E481", {"start": v(-14.38, -40.18) * mm, "end": v(-13.96, -40.3) * mm});
            skLineSegment(sketch, "E482", {"start": v(-13.96, -40.3) * mm, "end": v(-13.53, -40.44) * mm});
            skLineSegment(sketch, "E483", {"start": v(-13.53, -40.44) * mm, "end": v(-13.1, -40.57) * mm});
            skLineSegment(sketch, "E484", {"start": v(-13.1, -40.57) * mm, "end": v(-12.68, -40.7) * mm});
            skLineSegment(sketch, "E485", {"start": v(-12.68, -40.7) * mm, "end": v(-12.25, -40.82) * mm});
            skLineSegment(sketch, "E486", {"start": v(-12.25, -40.82) * mm, "end": v(-11.82, -40.95) * mm});
            skLineSegment(sketch, "E487", {"start": v(-11.82, -40.95) * mm, "end": v(-11.4, -41.08) * mm});
            skLineSegment(sketch, "E488", {"start": v(-11.4, -41.08) * mm, "end": v(-10.97, -41.2) * mm});
            skLineSegment(sketch, "E489", {"start": v(-10.97, -41.2) * mm, "end": v(-10.54, -41.34) * mm});
            skLineSegment(sketch, "E490", {"start": v(-10.54, -41.34) * mm, "end": v(-10.12, -41.47) * mm});
            skLineSegment(sketch, "E491", {"start": v(-10.12, -41.47) * mm, "end": v(-9.7, -41.6) * mm});
            skLineSegment(sketch, "E492", {"start": v(-9.7, -41.6) * mm, "end": v(-9.37, -41.7) * mm});
            skLineSegment(sketch, "E493", {"start": v(-9.37, -41.7) * mm, "end": v(-9.48, -42.12) * mm});
            skLineSegment(sketch, "E494", {"start": v(-9.48, -42.12) * mm, "end": v(-9.6, -42.55) * mm});
            skLineSegment(sketch, "E495", {"start": v(-9.6, -42.55) * mm, "end": v(-9.71, -42.99) * mm});
            skLineSegment(sketch, "E496", {"start": v(-9.71, -42.99) * mm, "end": v(-9.83, -43.42) * mm});
            skLineSegment(sketch, "E497", {"start": v(-9.83, -43.42) * mm, "end": v(-9.94, -43.85) * mm});
            skLineSegment(sketch, "E498", {"start": v(-9.94, -43.85) * mm, "end": v(-10.06, -44.28) * mm});
            skLineSegment(sketch, "E499", {"start": v(-10.06, -44.28) * mm, "end": v(-10.17, -44.7) * mm});
            skLineSegment(sketch, "E500", {"start": v(-10.17, -44.7) * mm, "end": v(-10.29, -45.14) * mm});
            skLineSegment(sketch, "E501", {"start": v(-10.29, -45.14) * mm, "end": v(-10.4, -45.57) * mm});
            skLineSegment(sketch, "E502", {"start": v(-10.4, -45.57) * mm, "end": v(-10.52, -46) * mm});
            skLineSegment(sketch, "E503", {"start": v(-10.52, -46) * mm, "end": v(-10.63, -46.43) * mm});
            skLineSegment(sketch, "E504", {"start": v(-10.63, -46.43) * mm, "end": v(-10.75, -46.86) * mm});
            skLineSegment(sketch, "E505", {"start": v(-10.75, -46.86) * mm, "end": v(-10.86, -47.29) * mm});
            skLineSegment(sketch, "E506", {"start": v(-10.86, -47.29) * mm, "end": v(-10.98, -47.72) * mm});
            skLineSegment(sketch, "E507", {"start": v(-10.98, -47.72) * mm, "end": v(-11.1, -48.15) * mm});
            skLineSegment(sketch, "E508", {"start": v(-11.1, -48.15) * mm, "end": v(-11.21, -48.58) * mm});
            skLineSegment(sketch, "E509", {"start": v(-11.21, -48.58) * mm, "end": v(-11.25, -48.72) * mm});
            skLineSegment(sketch, "E510", {"start": v(-11.25, -48.72) * mm, "end": v(-10.81, -48.81) * mm});
            skLineSegment(sketch, "E511", {"start": v(-10.81, -48.81) * mm, "end": v(-10.38, -48.9) * mm});
            skLineSegment(sketch, "E512", {"start": v(-10.38, -48.9) * mm, "end": v(-9.97, -49) * mm});
            skLineSegment(sketch, "E513", {"start": v(-9.97, -49) * mm, "end": v(-9.77, -48.6) * mm});
            skLineSegment(sketch, "E514", {"start": v(-9.77, -48.6) * mm, "end": v(-9.57, -48.2) * mm});
            skLineSegment(sketch, "E515", {"start": v(-9.57, -48.2) * mm, "end": v(-9.37, -47.8) * mm});
            skLineSegment(sketch, "E516", {"start": v(-9.37, -47.8) * mm, "end": v(-9.18, -47.4) * mm});
            skLineSegment(sketch, "E517", {"start": v(-9.18, -47.4) * mm, "end": v(-8.98, -47) * mm});
            skLineSegment(sketch, "E518", {"start": v(-8.98, -47) * mm, "end": v(-8.78, -46.6) * mm});
            skLineSegment(sketch, "E519", {"start": v(-8.78, -46.6) * mm, "end": v(-8.58, -46.2) * mm});
            skLineSegment(sketch, "E520", {"start": v(-8.58, -46.2) * mm, "end": v(-8.38, -45.8) * mm});
            skLineSegment(sketch, "E521", {"start": v(-8.38, -45.8) * mm, "end": v(-8.19, -45.4) * mm});
            skLineSegment(sketch, "E522", {"start": v(-8.19, -45.4) * mm, "end": v(-7.99, -45) * mm});
            skLineSegment(sketch, "E523", {"start": v(-7.99, -45) * mm, "end": v(-7.79, -44.6) * mm});
            skLineSegment(sketch, "E524", {"start": v(-7.79, -44.6) * mm, "end": v(-7.6, -44.2) * mm});
            skLineSegment(sketch, "E525", {"start": v(-7.6, -44.2) * mm, "end": v(-7.4, -43.8) * mm});
            skLineSegment(sketch, "E526", {"start": v(-7.4, -43.8) * mm, "end": v(-7.2, -43.4) * mm});
            skLineSegment(sketch, "E527", {"start": v(-7.2, -43.4) * mm, "end": v(-7, -43) * mm});
            skLineSegment(sketch, "E528", {"start": v(-7, -43) * mm, "end": v(-6.8, -42.6) * mm});
            skLineSegment(sketch, "E529", {"start": v(-6.8, -42.6) * mm, "end": v(-6.6, -42.22) * mm});
            skLineSegment(sketch, "E530", {"start": v(-6.6, -42.22) * mm, "end": v(-6.16, -42.26) * mm});
            skLineSegment(sketch, "E531", {"start": v(-6.16, -42.26) * mm, "end": v(-5.72, -42.3) * mm});
            skLineSegment(sketch, "E532", {"start": v(-5.72, -42.3) * mm, "end": v(-5.27, -42.33) * mm});
            skLineSegment(sketch, "E533", {"start": v(-5.27, -42.33) * mm, "end": v(-4.83, -42.37) * mm});
            skLineSegment(sketch, "E534", {"start": v(-4.83, -42.37) * mm, "end": v(-4.38, -42.4) * mm});
            skLineSegment(sketch, "E535", {"start": v(-4.38, -42.4) * mm, "end": v(-3.94, -42.44) * mm});
            skLineSegment(sketch, "E536", {"start": v(-3.94, -42.44) * mm, "end": v(-3.5, -42.48) * mm});
            skLineSegment(sketch, "E537", {"start": v(-3.5, -42.48) * mm, "end": v(-3.05, -42.52) * mm});
            skLineSegment(sketch, "E538", {"start": v(-3.05, -42.52) * mm, "end": v(-2.6, -42.55) * mm});
            skLineSegment(sketch, "E539", {"start": v(-2.6, -42.55) * mm, "end": v(-2.16, -42.6) * mm});
            skLineSegment(sketch, "E540", {"start": v(-2.16, -42.6) * mm, "end": v(-1.72, -42.63) * mm});
            skLineSegment(sketch, "E541", {"start": v(-1.72, -42.63) * mm, "end": v(-1.28, -42.66) * mm});
            skLineSegment(sketch, "E542", {"start": v(-1.28, -42.66) * mm, "end": v(-0.83, -42.7) * mm});
            skLineSegment(sketch, "E543", {"start": v(-0.83, -42.7) * mm, "end": v(-0.5, -42.73) * mm});
            skLineSegment(sketch, "E544", {"start": v(-0.5, -42.73) * mm, "end": v(-0.52, -43.17) * mm});
            skLineSegment(sketch, "E545", {"start": v(-0.52, -43.17) * mm, "end": v(-0.54, -43.62) * mm});
            skLineSegment(sketch, "E546", {"start": v(-0.54, -43.62) * mm, "end": v(-0.56, -44.06) * mm});
            skLineSegment(sketch, "E547", {"start": v(-0.56, -44.06) * mm, "end": v(-0.59, -44.5) * mm});
            skLineSegment(sketch, "E548", {"start": v(-0.59, -44.5) * mm, "end": v(-0.6, -44.95) * mm});
            skLineSegment(sketch, "E549", {"start": v(-0.6, -44.95) * mm, "end": v(-0.63, -45.4) * mm});
            skLineSegment(sketch, "E550", {"start": v(-0.63, -45.4) * mm, "end": v(-0.66, -45.84) * mm});
            skLineSegment(sketch, "E551", {"start": v(-0.66, -45.84) * mm, "end": v(-0.68, -46.29) * mm});
            skLineSegment(sketch, "E552", {"start": v(-0.68, -46.29) * mm, "end": v(-0.7, -46.73) * mm});
            skLineSegment(sketch, "E553", {"start": v(-0.7, -46.73) * mm, "end": v(-0.73, -47.18) * mm});
            skLineSegment(sketch, "E554", {"start": v(-0.73, -47.18) * mm, "end": v(-0.75, -47.62) * mm});
            skLineSegment(sketch, "E555", {"start": v(-0.75, -47.62) * mm, "end": v(-0.77, -48.07) * mm});
            skLineSegment(sketch, "E556", {"start": v(-0.77, -48.07) * mm, "end": v(-0.8, -48.52) * mm});
            skLineSegment(sketch, "E557", {"start": v(-0.8, -48.52) * mm, "end": v(-0.82, -48.96) * mm});
            skLineSegment(sketch, "E558", {"start": v(-0.82, -48.96) * mm, "end": v(-0.84, -49.4) * mm});
            skLineSegment(sketch, "E559", {"start": v(-0.84, -49.4) * mm, "end": v(-0.87, -49.85) * mm});
            skLineSegment(sketch, "E560", {"start": v(-0.87, -49.85) * mm, "end": v(-0.87, -50) * mm});
            skLineSegment(sketch, "E561", {"start": v(-0.87, -50) * mm, "end": v(-0.43, -50) * mm});
            skLineSegment(sketch, "E562", {"start": v(-0.43, -50) * mm, "end": v(0.02, -50) * mm});
            skLineSegment(sketch, "E563", {"start": v(0.02, -50) * mm, "end": v(0.44, -50) * mm});
            skLineSegment(sketch, "E564", {"start": v(0.44, -50) * mm, "end": v(0.55, -49.57) * mm});
            skLineSegment(sketch, "E565", {"start": v(0.55, -49.57) * mm, "end": v(0.66, -49.13) * mm});
            skLineSegment(sketch, "E566", {"start": v(0.66, -49.13) * mm, "end": v(0.77, -48.7) * mm});
            skLineSegment(sketch, "E567", {"start": v(0.77, -48.7) * mm, "end": v(0.88, -48.27) * mm});
            skLineSegment(sketch, "E568", {"start": v(0.88, -48.27) * mm, "end": v(1, -47.84) * mm});
            skLineSegment(sketch, "E569", {"start": v(1, -47.84) * mm, "end": v(1.1, -47.4) * mm});
            skLineSegment(sketch, "E570", {"start": v(1.1, -47.4) * mm, "end": v(1.21, -46.98) * mm});
            skLineSegment(sketch, "E571", {"start": v(1.21, -46.98) * mm, "end": v(1.32, -46.55) * mm});
            skLineSegment(sketch, "E572", {"start": v(1.32, -46.55) * mm, "end": v(1.43, -46.11) * mm});
            skLineSegment(sketch, "E573", {"start": v(1.43, -46.11) * mm, "end": v(1.54, -45.68) * mm});
            skLineSegment(sketch, "E574", {"start": v(1.54, -45.68) * mm, "end": v(1.66, -45.25) * mm});
            skLineSegment(sketch, "E575", {"start": v(1.66, -45.25) * mm, "end": v(1.77, -44.82) * mm});
            skLineSegment(sketch, "E576", {"start": v(1.77, -44.82) * mm, "end": v(1.88, -44.39) * mm});
            skLineSegment(sketch, "E577", {"start": v(1.88, -44.39) * mm, "end": v(1.99, -43.96) * mm});
            skLineSegment(sketch, "E578", {"start": v(1.99, -43.96) * mm, "end": v(2.1, -43.52) * mm});
            skLineSegment(sketch, "E579", {"start": v(2.1, -43.52) * mm, "end": v(2.2, -43.1) * mm});
            skLineSegment(sketch, "E580", {"start": v(2.2, -43.1) * mm, "end": v(2.32, -42.67) * mm});
            skLineSegment(sketch, "E581", {"start": v(2.32, -42.67) * mm, "end": v(2.76, -42.61) * mm});
            skLineSegment(sketch, "E582", {"start": v(2.76, -42.61) * mm, "end": v(3.2, -42.56) * mm});
            skLineSegment(sketch, "E583", {"start": v(3.2, -42.56) * mm, "end": v(3.64, -42.5) * mm});
            skLineSegment(sketch, "E584", {"start": v(3.64, -42.5) * mm, "end": v(4.09, -42.45) * mm});
            skLineSegment(sketch, "E585", {"start": v(4.09, -42.45) * mm, "end": v(4.53, -42.39) * mm});
            skLineSegment(sketch, "E586", {"start": v(4.53, -42.39) * mm, "end": v(4.97, -42.33) * mm});
            skLineSegment(sketch, "E587", {"start": v(4.97, -42.33) * mm, "end": v(5.41, -42.28) * mm});
            skLineSegment(sketch, "E588", {"start": v(5.41, -42.28) * mm, "end": v(5.85, -42.22) * mm});
            skLineSegment(sketch, "E589", {"start": v(5.85, -42.22) * mm, "end": v(6.3, -42.17) * mm});
            skLineSegment(sketch, "E590", {"start": v(6.3, -42.17) * mm, "end": v(6.74, -42.1) * mm});
            skLineSegment(sketch, "E591", {"start": v(6.74, -42.1) * mm, "end": v(7.18, -42.05) * mm});
            skLineSegment(sketch, "E592", {"start": v(7.18, -42.05) * mm, "end": v(7.62, -42) * mm});
            skLineSegment(sketch, "E593", {"start": v(7.62, -42) * mm, "end": v(8.06, -41.94) * mm});
            skLineSegment(sketch, "E594", {"start": v(8.06, -41.94) * mm, "end": v(8.4, -41.9) * mm});
            skLineSegment(sketch, "E595", {"start": v(8.4, -41.9) * mm, "end": v(8.47, -42.34) * mm});
            skLineSegment(sketch, "E596", {"start": v(8.47, -42.34) * mm, "end": v(8.54, -42.78) * mm});
            skLineSegment(sketch, "E597", {"start": v(8.54, -42.78) * mm, "end": v(8.61, -43.22) * mm});
            skLineSegment(sketch, "E598", {"start": v(8.61, -43.22) * mm, "end": v(8.68, -43.66) * mm});
            skLineSegment(sketch, "E599", {"start": v(8.68, -43.66) * mm, "end": v(8.75, -44.1) * mm});
            skLineSegment(sketch, "E600", {"start": v(8.75, -44.1) * mm, "end": v(8.82, -44.54) * mm});
            skLineSegment(sketch, "E601", {"start": v(8.82, -44.54) * mm, "end": v(8.9, -44.98) * mm});
            skLineSegment(sketch, "E602", {"start": v(8.9, -44.98) * mm, "end": v(8.96, -45.42) * mm});
            skLineSegment(sketch, "E603", {"start": v(8.96, -45.42) * mm, "end": v(9.03, -45.86) * mm});
            skLineSegment(sketch, "E604", {"start": v(9.03, -45.86) * mm, "end": v(9.1, -46.3) * mm});
            skLineSegment(sketch, "E605", {"start": v(9.1, -46.3) * mm, "end": v(9.17, -46.74) * mm});
            skLineSegment(sketch, "E606", {"start": v(9.17, -46.74) * mm, "end": v(9.24, -47.18) * mm});
            skLineSegment(sketch, "E607", {"start": v(9.24, -47.18) * mm, "end": v(9.3, -47.62) * mm});
            skLineSegment(sketch, "E608", {"start": v(9.3, -47.62) * mm, "end": v(9.38, -48.06) * mm});
            skLineSegment(sketch, "E609", {"start": v(9.38, -48.06) * mm, "end": v(9.45, -48.5) * mm});
            skLineSegment(sketch, "E610", {"start": v(9.45, -48.5) * mm, "end": v(9.52, -48.94) * mm});
            skLineSegment(sketch, "E611", {"start": v(9.52, -48.94) * mm, "end": v(9.54, -49.08) * mm});
            skLineSegment(sketch, "E612", {"start": v(9.54, -49.08) * mm, "end": v(9.98, -49) * mm});
            skLineSegment(sketch, "E613", {"start": v(9.98, -49) * mm, "end": v(10.41, -48.9) * mm});
            skLineSegment(sketch, "E614", {"start": v(10.41, -48.9) * mm, "end": v(10.82, -48.81) * mm});
            skLineSegment(sketch, "E615", {"start": v(10.82, -48.81) * mm, "end": v(10.84, -48.37) * mm});
            skLineSegment(sketch, "E616", {"start": v(10.84, -48.37) * mm, "end": v(10.86, -47.92) * mm});
            skLineSegment(sketch, "E617", {"start": v(10.86, -47.92) * mm, "end": v(10.88, -47.48) * mm});
            skLineSegment(sketch, "E618", {"start": v(10.88, -47.48) * mm, "end": v(10.9, -47.03) * mm});
            skLineSegment(sketch, "E619", {"start": v(10.9, -47.03) * mm, "end": v(10.92, -46.59) * mm});
            skLineSegment(sketch, "E620", {"start": v(10.92, -46.59) * mm, "end": v(10.93, -46.14) * mm});
            skLineSegment(sketch, "E621", {"start": v(10.93, -46.14) * mm, "end": v(10.95, -45.7) * mm});
            skLineSegment(sketch, "E622", {"start": v(10.95, -45.7) * mm, "end": v(10.97, -45.25) * mm});
            skLineSegment(sketch, "E623", {"start": v(10.97, -45.25) * mm, "end": v(10.99, -44.8) * mm});
            skLineSegment(sketch, "E624", {"start": v(10.99, -44.8) * mm, "end": v(11, -44.36) * mm});
            skLineSegment(sketch, "E625", {"start": v(11, -44.36) * mm, "end": v(11.03, -43.92) * mm});
            skLineSegment(sketch, "E626", {"start": v(11.03, -43.92) * mm, "end": v(11.05, -43.47) * mm});
            skLineSegment(sketch, "E627", {"start": v(11.05, -43.47) * mm, "end": v(11.06, -43.03) * mm});
            skLineSegment(sketch, "E628", {"start": v(11.06, -43.03) * mm, "end": v(11.08, -42.58) * mm});
            skLineSegment(sketch, "E629", {"start": v(11.08, -42.58) * mm, "end": v(11.1, -42.14) * mm});
            skLineSegment(sketch, "E630", {"start": v(11.1, -42.14) * mm, "end": v(11.12, -41.7) * mm});
            skLineSegment(sketch, "E631", {"start": v(11.12, -41.7) * mm, "end": v(11.14, -41.26) * mm});
            skLineSegment(sketch, "E632", {"start": v(11.14, -41.26) * mm, "end": v(11.56, -41.1) * mm});
            skLineSegment(sketch, "E633", {"start": v(11.56, -41.1) * mm, "end": v(11.98, -40.96) * mm});
            skLineSegment(sketch, "E634", {"start": v(11.98, -40.96) * mm, "end": v(12.4, -40.82) * mm});
            skLineSegment(sketch, "E635", {"start": v(12.4, -40.82) * mm, "end": v(12.82, -40.67) * mm});
            skLineSegment(sketch, "E636", {"start": v(12.82, -40.67) * mm, "end": v(13.24, -40.52) * mm});
            skLineSegment(sketch, "E637", {"start": v(13.24, -40.52) * mm, "end": v(13.66, -40.38) * mm});
            skLineSegment(sketch, "E638", {"start": v(13.66, -40.38) * mm, "end": v(14.08, -40.23) * mm});
            skLineSegment(sketch, "E639", {"start": v(14.08, -40.23) * mm, "end": v(14.5, -40.08) * mm});
            skLineSegment(sketch, "E640", {"start": v(14.5, -40.08) * mm, "end": v(14.93, -39.93) * mm});
            skLineSegment(sketch, "E641", {"start": v(14.93, -39.93) * mm, "end": v(15.35, -39.79) * mm});
            skLineSegment(sketch, "E642", {"start": v(15.35, -39.79) * mm, "end": v(15.77, -39.64) * mm});
            skLineSegment(sketch, "E643", {"start": v(15.77, -39.64) * mm, "end": v(16.19, -39.5) * mm});
            skLineSegment(sketch, "E644", {"start": v(16.19, -39.5) * mm, "end": v(16.6, -39.35) * mm});
            skLineSegment(sketch, "E645", {"start": v(16.6, -39.35) * mm, "end": v(16.93, -39.24) * mm});
            skLineSegment(sketch, "E646", {"start": v(16.93, -39.24) * mm, "end": v(17.09, -39.65) * mm});
            skLineSegment(sketch, "E647", {"start": v(17.09, -39.65) * mm, "end": v(17.25, -40.07) * mm});
            skLineSegment(sketch, "E648", {"start": v(17.25, -40.07) * mm, "end": v(17.4, -40.48) * mm});
            skLineSegment(sketch, "E649", {"start": v(17.4, -40.48) * mm, "end": v(17.57, -40.9) * mm});
            skLineSegment(sketch, "E650", {"start": v(17.57, -40.9) * mm, "end": v(17.73, -41.32) * mm});
            skLineSegment(sketch, "E651", {"start": v(17.73, -41.32) * mm, "end": v(17.89, -41.73) * mm});
            skLineSegment(sketch, "E652", {"start": v(17.89, -41.73) * mm, "end": v(18.05, -42.15) * mm});
            skLineSegment(sketch, "E653", {"start": v(18.05, -42.15) * mm, "end": v(18.2, -42.56) * mm});
            skLineSegment(sketch, "E654", {"start": v(18.2, -42.56) * mm, "end": v(18.37, -42.98) * mm});
            skLineSegment(sketch, "E655", {"start": v(18.37, -42.98) * mm, "end": v(18.53, -43.4) * mm});
            skLineSegment(sketch, "E656", {"start": v(18.53, -43.4) * mm, "end": v(18.69, -43.81) * mm});
            skLineSegment(sketch, "E657", {"start": v(18.69, -43.81) * mm, "end": v(18.85, -44.23) * mm});
            skLineSegment(sketch, "E658", {"start": v(18.85, -44.23) * mm, "end": v(19, -44.64) * mm});
            skLineSegment(sketch, "E659", {"start": v(19, -44.64) * mm, "end": v(19.17, -45.06) * mm});
            skLineSegment(sketch, "E660", {"start": v(19.17, -45.06) * mm, "end": v(19.33, -45.48) * mm});
            skLineSegment(sketch, "E661", {"start": v(19.33, -45.48) * mm, "end": v(19.49, -45.9) * mm});
            skLineSegment(sketch, "E662", {"start": v(19.49, -45.9) * mm, "end": v(19.54, -46.03) * mm});
            skLineSegment(sketch, "E663", {"start": v(19.54, -46.03) * mm, "end": v(19.94, -45.85) * mm});
            skLineSegment(sketch, "E664", {"start": v(19.94, -45.85) * mm, "end": v(20.35, -45.67) * mm});
            skLineSegment(sketch, "E665", {"start": v(20.35, -45.67) * mm, "end": v(20.73, -45.5) * mm});
            skLineSegment(sketch, "E666", {"start": v(20.73, -45.5) * mm, "end": v(20.66, -45.06) * mm});
            skLineSegment(sketch, "E667", {"start": v(20.66, -45.06) * mm, "end": v(20.59, -44.62) * mm});
            skLineSegment(sketch, "E668", {"start": v(20.59, -44.62) * mm, "end": v(20.51, -44.18) * mm});
            skLineSegment(sketch, "E669", {"start": v(20.51, -44.18) * mm, "end": v(20.44, -43.74) * mm});
            skLineSegment(sketch, "E670", {"start": v(20.44, -43.74) * mm, "end": v(20.36, -43.3) * mm});
            skLineSegment(sketch, "E671", {"start": v(20.36, -43.3) * mm, "end": v(20.29, -42.86) * mm});
            skLineSegment(sketch, "E672", {"start": v(20.29, -42.86) * mm, "end": v(20.21, -42.42) * mm});
            skLineSegment(sketch, "E673", {"start": v(20.21, -42.42) * mm, "end": v(20.14, -41.98) * mm});
            skLineSegment(sketch, "E674", {"start": v(20.14, -41.98) * mm, "end": v(20.07, -41.54) * mm});
            skLineSegment(sketch, "E675", {"start": v(20.07, -41.54) * mm, "end": v(20, -41.1) * mm});
            skLineSegment(sketch, "E676", {"start": v(20, -41.1) * mm, "end": v(19.92, -40.66) * mm});
            skLineSegment(sketch, "E677", {"start": v(19.92, -40.66) * mm, "end": v(19.84, -40.23) * mm});
            skLineSegment(sketch, "E678", {"start": v(19.84, -40.23) * mm, "end": v(19.77, -39.79) * mm});
            skLineSegment(sketch, "E679", {"start": v(19.77, -39.79) * mm, "end": v(19.7, -39.35) * mm});
            skLineSegment(sketch, "E680", {"start": v(19.7, -39.35) * mm, "end": v(19.62, -38.9) * mm});
            skLineSegment(sketch, "E681", {"start": v(19.62, -38.9) * mm, "end": v(19.55, -38.47) * mm});
            skLineSegment(sketch, "E682", {"start": v(19.55, -38.47) * mm, "end": v(19.47, -38.04) * mm});
            skLineSegment(sketch, "E683", {"start": v(19.47, -38.04) * mm, "end": v(19.85, -37.8) * mm});
            skLineSegment(sketch, "E684", {"start": v(19.85, -37.8) * mm, "end": v(20.23, -37.58) * mm});
            skLineSegment(sketch, "E685", {"start": v(20.23, -37.58) * mm, "end": v(20.62, -37.35) * mm});
            skLineSegment(sketch, "E686", {"start": v(20.62, -37.35) * mm, "end": v(21, -37.11) * mm});
            skLineSegment(sketch, "E687", {"start": v(21, -37.11) * mm, "end": v(21.38, -36.88) * mm});
            skLineSegment(sketch, "E688", {"start": v(21.38, -36.88) * mm, "end": v(21.76, -36.65) * mm});
            skLineSegment(sketch, "E689", {"start": v(21.76, -36.65) * mm, "end": v(22.14, -36.42) * mm});
            skLineSegment(sketch, "E690", {"start": v(22.14, -36.42) * mm, "end": v(22.52, -36.2) * mm});
            skLineSegment(sketch, "E691", {"start": v(22.52, -36.2) * mm, "end": v(22.9, -35.96) * mm});
            skLineSegment(sketch, "E692", {"start": v(22.9, -35.96) * mm, "end": v(23.28, -35.73) * mm});
            skLineSegment(sketch, "E693", {"start": v(23.28, -35.73) * mm, "end": v(23.66, -35.5) * mm});
            skLineSegment(sketch, "E694", {"start": v(23.66, -35.5) * mm, "end": v(24.05, -35.27) * mm});
            skLineSegment(sketch, "E695", {"start": v(24.05, -35.27) * mm, "end": v(24.43, -35.03) * mm});
            skLineSegment(sketch, "E696", {"start": v(24.43, -35.03) * mm, "end": v(24.72, -34.86) * mm});
            skLineSegment(sketch, "E697", {"start": v(24.72, -34.86) * mm, "end": v(24.96, -35.23) * mm});
            skLineSegment(sketch, "E698", {"start": v(24.96, -35.23) * mm, "end": v(25.2, -35.6) * mm});
            skLineSegment(sketch, "E699", {"start": v(25.2, -35.6) * mm, "end": v(25.45, -35.98) * mm});
            skLineSegment(sketch, "E700", {"start": v(25.45, -35.98) * mm, "end": v(25.69, -36.35) * mm});
            skLineSegment(sketch, "E701", {"start": v(25.69, -36.35) * mm, "end": v(25.93, -36.73) * mm});
            skLineSegment(sketch, "E702", {"start": v(25.93, -36.73) * mm, "end": v(26.17, -37.1) * mm});
            skLineSegment(sketch, "E703", {"start": v(26.17, -37.1) * mm, "end": v(26.42, -37.47) * mm});
            skLineSegment(sketch, "E704", {"start": v(26.42, -37.47) * mm, "end": v(26.66, -37.85) * mm});
            skLineSegment(sketch, "E705", {"start": v(26.66, -37.85) * mm, "end": v(26.9, -38.22) * mm});
            skLineSegment(sketch, "E706", {"start": v(26.9, -38.22) * mm, "end": v(27.14, -38.6) * mm});
            skLineSegment(sketch, "E707", {"start": v(27.14, -38.6) * mm, "end": v(27.39, -38.97) * mm});
            skLineSegment(sketch, "E708", {"start": v(27.39, -38.97) * mm, "end": v(27.63, -39.34) * mm});
            skLineSegment(sketch, "E709", {"start": v(27.63, -39.34) * mm, "end": v(27.87, -39.72) * mm});
            skLineSegment(sketch, "E710", {"start": v(27.87, -39.72) * mm, "end": v(28.12, -40.1) * mm});
            skLineSegment(sketch, "E711", {"start": v(28.12, -40.1) * mm, "end": v(28.36, -40.46) * mm});
            skLineSegment(sketch, "E712", {"start": v(28.36, -40.46) * mm, "end": v(28.6, -40.84) * mm});
            skLineSegment(sketch, "E713", {"start": v(28.6, -40.84) * mm, "end": v(28.68, -40.96) * mm});
            skLineSegment(sketch, "E714", {"start": v(28.68, -40.96) * mm, "end": v(29.04, -40.7) * mm});
            skLineSegment(sketch, "E715", {"start": v(29.04, -40.7) * mm, "end": v(29.4, -40.44) * mm});
            skLineSegment(sketch, "E716", {"start": v(29.4, -40.44) * mm, "end": v(29.74, -40.2) * mm});
            skLineSegment(sketch, "E717", {"start": v(29.74, -40.2) * mm, "end": v(29.58, -39.78) * mm});
            skLineSegment(sketch, "E718", {"start": v(29.58, -39.78) * mm, "end": v(29.41, -39.36) * mm});
            skLineSegment(sketch, "E719", {"start": v(29.41, -39.36) * mm, "end": v(29.25, -38.95) * mm});
            skLineSegment(sketch, "E720", {"start": v(29.25, -38.95) * mm, "end": v(29.08, -38.54) * mm});
            skLineSegment(sketch, "E721", {"start": v(29.08, -38.54) * mm, "end": v(28.92, -38.12) * mm});
            skLineSegment(sketch, "E722", {"start": v(28.92, -38.12) * mm, "end": v(28.76, -37.7) * mm});
            skLineSegment(sketch, "E723", {"start": v(28.76, -37.7) * mm, "end": v(28.6, -37.3) * mm});
            skLineSegment(sketch, "E724", {"start": v(28.6, -37.3) * mm, "end": v(28.43, -36.88) * mm});
            skLineSegment(sketch, "E725", {"start": v(28.43, -36.88) * mm, "end": v(28.26, -36.46) * mm});
            skLineSegment(sketch, "E726", {"start": v(28.26, -36.46) * mm, "end": v(28.1, -36.05) * mm});
            skLineSegment(sketch, "E727", {"start": v(28.1, -36.05) * mm, "end": v(27.94, -35.64) * mm});
            skLineSegment(sketch, "E728", {"start": v(27.94, -35.64) * mm, "end": v(27.77, -35.22) * mm});
            skLineSegment(sketch, "E729", {"start": v(27.77, -35.22) * mm, "end": v(27.6, -34.8) * mm});
            skLineSegment(sketch, "E730", {"start": v(27.6, -34.8) * mm, "end": v(27.44, -34.4) * mm});
            skLineSegment(sketch, "E731", {"start": v(27.44, -34.4) * mm, "end": v(27.28, -33.98) * mm});
            skLineSegment(sketch, "E732", {"start": v(27.28, -33.98) * mm, "end": v(27.12, -33.56) * mm});
            skLineSegment(sketch, "E733", {"start": v(27.12, -33.56) * mm, "end": v(26.96, -33.16) * mm});
            skLineSegment(sketch, "E734", {"start": v(26.96, -33.16) * mm, "end": v(27.28, -32.85) * mm});
            skLineSegment(sketch, "E735", {"start": v(27.28, -32.85) * mm, "end": v(27.6, -32.55) * mm});
            skLineSegment(sketch, "E736", {"start": v(27.6, -32.55) * mm, "end": v(27.93, -32.24) * mm});
            skLineSegment(sketch, "E737", {"start": v(27.93, -32.24) * mm, "end": v(28.25, -31.94) * mm});
            skLineSegment(sketch, "E738", {"start": v(28.25, -31.94) * mm, "end": v(28.58, -31.63) * mm});
            skLineSegment(sketch, "E739", {"start": v(28.58, -31.63) * mm, "end": v(28.9, -31.33) * mm});
            skLineSegment(sketch, "E740", {"start": v(28.9, -31.33) * mm, "end": v(29.23, -31.02) * mm});
            skLineSegment(sketch, "E741", {"start": v(29.23, -31.02) * mm, "end": v(29.55, -30.72) * mm});
            skLineSegment(sketch, "E742", {"start": v(29.55, -30.72) * mm, "end": v(29.88, -30.41) * mm});
            skLineSegment(sketch, "E743", {"start": v(29.88, -30.41) * mm, "end": v(30.2, -30.1) * mm});
            skLineSegment(sketch, "E744", {"start": v(30.2, -30.1) * mm, "end": v(30.53, -29.8) * mm});
            skLineSegment(sketch, "E745", {"start": v(30.53, -29.8) * mm, "end": v(30.85, -29.5) * mm});
            skLineSegment(sketch, "E746", {"start": v(30.85, -29.5) * mm, "end": v(31.18, -29.2) * mm});
            skLineSegment(sketch, "E747", {"start": v(31.18, -29.2) * mm, "end": v(31.43, -28.96) * mm});
            skLineSegment(sketch, "E748", {"start": v(31.43, -28.96) * mm, "end": v(31.74, -29.27) * mm});
            skLineSegment(sketch, "E749", {"start": v(31.74, -29.27) * mm, "end": v(32.06, -29.59) * mm});
            skLineSegment(sketch, "E750", {"start": v(32.06, -29.59) * mm, "end": v(32.37, -29.9) * mm});
            skLineSegment(sketch, "E751", {"start": v(32.37, -29.9) * mm, "end": v(32.69, -30.22) * mm});
            skLineSegment(sketch, "E752", {"start": v(32.69, -30.22) * mm, "end": v(33, -30.53) * mm});
            skLineSegment(sketch, "E753", {"start": v(33, -30.53) * mm, "end": v(33.32, -30.85) * mm});
            skLineSegment(sketch, "E754", {"start": v(33.32, -30.85) * mm, "end": v(33.63, -31.16) * mm});
            skLineSegment(sketch, "E755", {"start": v(33.63, -31.16) * mm, "end": v(33.95, -31.48) * mm});
            skLineSegment(sketch, "E756", {"start": v(33.95, -31.48) * mm, "end": v(34.26, -31.8) * mm});
            skLineSegment(sketch, "E757", {"start": v(34.26, -31.8) * mm, "end": v(34.58, -32.1) * mm});
            skLineSegment(sketch, "E758", {"start": v(34.58, -32.1) * mm, "end": v(34.9, -32.42) * mm});
            skLineSegment(sketch, "E759", {"start": v(34.9, -32.42) * mm, "end": v(35.2, -32.74) * mm});
            skLineSegment(sketch, "E760", {"start": v(35.2, -32.74) * mm, "end": v(35.52, -33.05) * mm});
            skLineSegment(sketch, "E761", {"start": v(35.52, -33.05) * mm, "end": v(35.84, -33.37) * mm});
            skLineSegment(sketch, "E762", {"start": v(35.84, -33.37) * mm, "end": v(36.15, -33.68) * mm});
            skLineSegment(sketch, "E763", {"start": v(36.15, -33.68) * mm, "end": v(36.47, -34) * mm});
            skLineSegment(sketch, "E764", {"start": v(36.47, -34) * mm, "end": v(36.57, -34.1) * mm});
            skLineSegment(sketch, "E765", {"start": v(36.57, -34.1) * mm, "end": v(36.87, -33.77) * mm});
            skLineSegment(sketch, "E766", {"start": v(36.87, -33.77) * mm, "end": v(37.17, -33.44) * mm});
            skLineSegment(sketch, "E767", {"start": v(37.17, -33.44) * mm, "end": v(37.45, -33.13) * mm});
            skLineSegment(sketch, "E768", {"start": v(37.45, -33.13) * mm, "end": v(37.2, -32.76) * mm});
            skLineSegment(sketch, "E769", {"start": v(37.2, -32.76) * mm, "end": v(36.95, -32.39) * mm});
            skLineSegment(sketch, "E770", {"start": v(36.95, -32.39) * mm, "end": v(36.7, -32.02) * mm});
            skLineSegment(sketch, "E771", {"start": v(36.7, -32.02) * mm, "end": v(36.46, -31.65) * mm});
            skLineSegment(sketch, "E772", {"start": v(36.46, -31.65) * mm, "end": v(36.21, -31.28) * mm});
            skLineSegment(sketch, "E773", {"start": v(36.21, -31.28) * mm, "end": v(35.97, -30.9) * mm});
            skLineSegment(sketch, "E774", {"start": v(35.97, -30.9) * mm, "end": v(35.72, -30.53) * mm});
            skLineSegment(sketch, "E775", {"start": v(35.72, -30.53) * mm, "end": v(35.47, -30.16) * mm});
            skLineSegment(sketch, "E776", {"start": v(35.47, -30.16) * mm, "end": v(35.23, -29.8) * mm});
            skLineSegment(sketch, "E777", {"start": v(35.23, -29.8) * mm, "end": v(34.98, -29.42) * mm});
            skLineSegment(sketch, "E778", {"start": v(34.98, -29.42) * mm, "end": v(34.74, -29.05) * mm});
            skLineSegment(sketch, "E779", {"start": v(34.74, -29.05) * mm, "end": v(34.49, -28.68) * mm});
            skLineSegment(sketch, "E780", {"start": v(34.49, -28.68) * mm, "end": v(34.24, -28.3) * mm});
            skLineSegment(sketch, "E781", {"start": v(34.24, -28.3) * mm, "end": v(34, -27.93) * mm});
            skLineSegment(sketch, "E782", {"start": v(34, -27.93) * mm, "end": v(33.75, -27.56) * mm});
            skLineSegment(sketch, "E783", {"start": v(33.75, -27.56) * mm, "end": v(33.5, -27.2) * mm});
            skLineSegment(sketch, "E784", {"start": v(33.5, -27.2) * mm, "end": v(33.26, -26.83) * mm});
            skLineSegment(sketch, "E785", {"start": v(33.26, -26.83) * mm, "end": v(33.51, -26.46) * mm});
            skLineSegment(sketch, "E786", {"start": v(33.51, -26.46) * mm, "end": v(33.77, -26.1) * mm});
            skLineSegment(sketch, "E787", {"start": v(33.77, -26.1) * mm, "end": v(34.02, -25.73) * mm});
            skLineSegment(sketch, "E788", {"start": v(34.02, -25.73) * mm, "end": v(34.28, -25.37) * mm});
            skLineSegment(sketch, "E789", {"start": v(34.28, -25.37) * mm, "end": v(34.53, -25) * mm});
            skLineSegment(sketch, "E790", {"start": v(34.53, -25) * mm, "end": v(34.79, -24.63) * mm});
            skLineSegment(sketch, "E791", {"start": v(34.79, -24.63) * mm, "end": v(35.04, -24.27) * mm});
            skLineSegment(sketch, "E792", {"start": v(35.04, -24.27) * mm, "end": v(35.3, -23.9) * mm});
            skLineSegment(sketch, "E793", {"start": v(35.3, -23.9) * mm, "end": v(35.55, -23.53) * mm});
            skLineSegment(sketch, "E794", {"start": v(35.55, -23.53) * mm, "end": v(35.8, -23.17) * mm});
            skLineSegment(sketch, "E795", {"start": v(35.8, -23.17) * mm, "end": v(36.06, -22.8) * mm});
            skLineSegment(sketch, "E796", {"start": v(36.06, -22.8) * mm, "end": v(36.31, -22.44) * mm});
            skLineSegment(sketch, "E797", {"start": v(36.31, -22.44) * mm, "end": v(36.56, -22.07) * mm});
            skLineSegment(sketch, "E798", {"start": v(36.56, -22.07) * mm, "end": v(36.76, -21.8) * mm});
            skLineSegment(sketch, "E799", {"start": v(36.76, -21.8) * mm, "end": v(37.13, -22.03) * mm});
            skLineSegment(sketch, "E800", {"start": v(37.13, -22.03) * mm, "end": v(37.5, -22.28) * mm});
            skLineSegment(sketch, "E801", {"start": v(37.5, -22.28) * mm, "end": v(37.88, -22.52) * mm});
            skLineSegment(sketch, "E802", {"start": v(37.88, -22.52) * mm, "end": v(38.25, -22.76) * mm});
            skLineSegment(sketch, "E803", {"start": v(38.25, -22.76) * mm, "end": v(38.63, -23) * mm});
            skLineSegment(sketch, "E804", {"start": v(38.63, -23) * mm, "end": v(39, -23.25) * mm});
            skLineSegment(sketch, "E805", {"start": v(39, -23.25) * mm, "end": v(39.38, -23.49) * mm});
            skLineSegment(sketch, "E806", {"start": v(39.38, -23.49) * mm, "end": v(39.75, -23.73) * mm});
            skLineSegment(sketch, "E807", {"start": v(39.75, -23.73) * mm, "end": v(40.12, -23.98) * mm});
            skLineSegment(sketch, "E808", {"start": v(40.12, -23.98) * mm, "end": v(40.5, -24.22) * mm});
            skLineSegment(sketch, "E809", {"start": v(40.5, -24.22) * mm, "end": v(40.87, -24.46) * mm});
            skLineSegment(sketch, "E810", {"start": v(40.87, -24.46) * mm, "end": v(41.24, -24.7) * mm});
            skLineSegment(sketch, "E811", {"start": v(41.24, -24.7) * mm, "end": v(41.62, -24.95) * mm});
            skLineSegment(sketch, "E812", {"start": v(41.62, -24.95) * mm, "end": v(42, -25.19) * mm});
            skLineSegment(sketch, "E813", {"start": v(42, -25.19) * mm, "end": v(42.37, -25.43) * mm});
            skLineSegment(sketch, "E814", {"start": v(42.37, -25.43) * mm, "end": v(42.74, -25.67) * mm});
            skLineSegment(sketch, "E815", {"start": v(42.74, -25.67) * mm, "end": v(42.86, -25.75) * mm});
            skLineSegment(sketch, "E816", {"start": v(42.86, -25.75) * mm, "end": v(43.08, -25.37) * mm});
            skLineSegment(sketch, "E817", {"start": v(43.08, -25.37) * mm, "end": v(43.3, -24.98) * mm});
            skLineSegment(sketch, "E818", {"start": v(43.3, -24.98) * mm, "end": v(43.52, -24.62) * mm});
            skLineSegment(sketch, "E819", {"start": v(43.52, -24.62) * mm, "end": v(43.2, -24.3) * mm});
            skLineSegment(sketch, "E820", {"start": v(43.2, -24.3) * mm, "end": v(42.88, -24) * mm});
            skLineSegment(sketch, "E821", {"start": v(42.88, -24) * mm, "end": v(42.56, -23.69) * mm});
            skLineSegment(sketch, "E822", {"start": v(42.56, -23.69) * mm, "end": v(42.24, -23.37) * mm});
            skLineSegment(sketch, "E823", {"start": v(42.24, -23.37) * mm, "end": v(41.93, -23.06) * mm});
            skLineSegment(sketch, "E824", {"start": v(41.93, -23.06) * mm, "end": v(41.6, -22.75) * mm});
            skLineSegment(sketch, "E825", {"start": v(41.6, -22.75) * mm, "end": v(41.29, -22.44) * mm});
            skLineSegment(sketch, "E826", {"start": v(41.29, -22.44) * mm, "end": v(40.97, -22.13) * mm});
            skLineSegment(sketch, "E827", {"start": v(40.97, -22.13) * mm, "end": v(40.65, -21.82) * mm});
            skLineSegment(sketch, "E828", {"start": v(40.65, -21.82) * mm, "end": v(40.33, -21.5) * mm});
            skLineSegment(sketch, "E829", {"start": v(40.33, -21.5) * mm, "end": v(40.02, -21.2) * mm});
            skLineSegment(sketch, "E830", {"start": v(40.02, -21.2) * mm, "end": v(39.7, -20.88) * mm});
            skLineSegment(sketch, "E831", {"start": v(39.7, -20.88) * mm, "end": v(39.38, -20.57) * mm});
            skLineSegment(sketch, "E832", {"start": v(39.38, -20.57) * mm, "end": v(39.06, -20.26) * mm});
            skLineSegment(sketch, "E833", {"start": v(39.06, -20.26) * mm, "end": v(38.74, -19.94) * mm});
            skLineSegment(sketch, "E834", {"start": v(38.74, -19.94) * mm, "end": v(38.42, -19.63) * mm});
            skLineSegment(sketch, "E835", {"start": v(38.42, -19.63) * mm, "end": v(38.11, -19.33) * mm});
            skLineSegment(sketch, "E836", {"start": v(38.11, -19.33) * mm, "end": v(38.28, -18.92) * mm});
            skLineSegment(sketch, "E837", {"start": v(38.28, -18.92) * mm, "end": v(38.46, -18.5) * mm});
            skLineSegment(sketch, "E838", {"start": v(38.46, -18.5) * mm, "end": v(38.63, -18.1) * mm});
            skLineSegment(sketch, "E839", {"start": v(38.63, -18.1) * mm, "end": v(38.8, -17.68) * mm});
            skLineSegment(sketch, "E840", {"start": v(38.8, -17.68) * mm, "end": v(38.97, -17.27) * mm});
            skLineSegment(sketch, "E841", {"start": v(38.97, -17.27) * mm, "end": v(39.15, -16.86) * mm});
            skLineSegment(sketch, "E842", {"start": v(39.15, -16.86) * mm, "end": v(39.32, -16.45) * mm});
            skLineSegment(sketch, "E843", {"start": v(39.32, -16.45) * mm, "end": v(39.5, -16.04) * mm});
            skLineSegment(sketch, "E844", {"start": v(39.5, -16.04) * mm, "end": v(39.66, -15.63) * mm});
            skLineSegment(sketch, "E845", {"start": v(39.66, -15.63) * mm, "end": v(39.84, -15.22) * mm});
            skLineSegment(sketch, "E846", {"start": v(39.84, -15.22) * mm, "end": v(40, -14.8) * mm});
            skLineSegment(sketch, "E847", {"start": v(40, -14.8) * mm, "end": v(40.18, -14.4) * mm});
            skLineSegment(sketch, "E848", {"start": v(40.18, -14.4) * mm, "end": v(40.35, -13.99) * mm});
            skLineSegment(sketch, "E849", {"start": v(40.35, -13.99) * mm, "end": v(40.49, -13.67) * mm});
            skLineSegment(sketch, "E850", {"start": v(40.49, -13.67) * mm, "end": v(40.9, -13.83) * mm});
            skLineSegment(sketch, "E851", {"start": v(40.9, -13.83) * mm, "end": v(41.32, -14) * mm});
            skLineSegment(sketch, "E852", {"start": v(41.32, -14) * mm, "end": v(41.73, -14.15) * mm});
            skLineSegment(sketch, "E853", {"start": v(41.73, -14.15) * mm, "end": v(42.15, -14.31) * mm});
            skLineSegment(sketch, "E854", {"start": v(42.15, -14.31) * mm, "end": v(42.57, -14.47) * mm});
            skLineSegment(sketch, "E855", {"start": v(42.57, -14.47) * mm, "end": v(42.98, -14.63) * mm});
            skLineSegment(sketch, "E856", {"start": v(42.98, -14.63) * mm, "end": v(43.4, -14.8) * mm});
            skLineSegment(sketch, "E857", {"start": v(43.4, -14.8) * mm, "end": v(43.81, -14.95) * mm});
            skLineSegment(sketch, "E858", {"start": v(43.81, -14.95) * mm, "end": v(44.23, -15.1) * mm});
            skLineSegment(sketch, "E859", {"start": v(44.23, -15.1) * mm, "end": v(44.65, -15.27) * mm});
            skLineSegment(sketch, "E860", {"start": v(44.65, -15.27) * mm, "end": v(45.06, -15.43) * mm});
            skLineSegment(sketch, "E861", {"start": v(45.06, -15.43) * mm, "end": v(45.48, -15.59) * mm});
            skLineSegment(sketch, "E862", {"start": v(45.48, -15.59) * mm, "end": v(45.9, -15.75) * mm});
            skLineSegment(sketch, "E863", {"start": v(45.9, -15.75) * mm, "end": v(46.31, -15.9) * mm});
            skLineSegment(sketch, "E864", {"start": v(46.31, -15.9) * mm, "end": v(46.73, -16.07) * mm});
            skLineSegment(sketch, "E865", {"start": v(46.73, -16.07) * mm, "end": v(47.14, -16.23) * mm});
            skLineSegment(sketch, "E866", {"start": v(47.14, -16.23) * mm, "end": v(47.28, -16.28) * mm});
            skLineSegment(sketch, "E867", {"start": v(47.28, -16.28) * mm, "end": v(47.42, -15.86) * mm});
            skLineSegment(sketch, "E868", {"start": v(47.42, -15.86) * mm, "end": v(47.56, -15.43) * mm});
            skLineSegment(sketch, "E869", {"start": v(47.56, -15.43) * mm, "end": v(47.69, -15.04) * mm});
            skLineSegment(sketch, "E870", {"start": v(47.69, -15.04) * mm, "end": v(47.3, -14.8) * mm});
            skLineSegment(sketch, "E871", {"start": v(47.3, -14.8) * mm, "end": v(46.93, -14.56) * mm});
            skLineSegment(sketch, "E872", {"start": v(46.93, -14.56) * mm, "end": v(46.56, -14.32) * mm});
            skLineSegment(sketch, "E873", {"start": v(46.56, -14.32) * mm, "end": v(46.18, -14.08) * mm});
            skLineSegment(sketch, "E874", {"start": v(46.18, -14.08) * mm, "end": v(45.8, -13.84) * mm});
            skLineSegment(sketch, "E875", {"start": v(45.8, -13.84) * mm, "end": v(45.43, -13.6) * mm});
            skLineSegment(sketch, "E876", {"start": v(45.43, -13.6) * mm, "end": v(45.05, -13.36) * mm});
            skLineSegment(sketch, "E877", {"start": v(45.05, -13.36) * mm, "end": v(44.68, -13.13) * mm});
            skLineSegment(sketch, "E878", {"start": v(44.68, -13.13) * mm, "end": v(44.3, -12.89) * mm});
            skLineSegment(sketch, "E879", {"start": v(44.3, -12.89) * mm, "end": v(43.92, -12.65) * mm});
            skLineSegment(sketch, "E880", {"start": v(43.92, -12.65) * mm, "end": v(43.55, -12.4) * mm});
            skLineSegment(sketch, "E881", {"start": v(43.55, -12.4) * mm, "end": v(43.17, -12.17) * mm});
            skLineSegment(sketch, "E882", {"start": v(43.17, -12.17) * mm, "end": v(42.8, -11.93) * mm});
            skLineSegment(sketch, "E883", {"start": v(42.8, -11.93) * mm, "end": v(42.42, -11.7) * mm});
            skLineSegment(sketch, "E884", {"start": v(42.42, -11.7) * mm, "end": v(42.04, -11.45) * mm});
            skLineSegment(sketch, "E885", {"start": v(42.04, -11.45) * mm, "end": v(41.67, -11.22) * mm});
            skLineSegment(sketch, "E886", {"start": v(41.67, -11.22) * mm, "end": v(41.3, -10.98) * mm});
            skLineSegment(sketch, "E887", {"start": v(41.3, -10.98) * mm, "end": v(41.38, -10.54) * mm});
            skLineSegment(sketch, "E888", {"start": v(41.38, -10.54) * mm, "end": v(41.46, -10.1) * mm});
            skLineSegment(sketch, "E889", {"start": v(41.46, -10.1) * mm, "end": v(41.55, -9.67) * mm});
            skLineSegment(sketch, "E890", {"start": v(41.55, -9.67) * mm, "end": v(41.63, -9.23) * mm});
            skLineSegment(sketch, "E891", {"start": v(41.63, -9.23) * mm, "end": v(41.71, -8.8) * mm});
            skLineSegment(sketch, "E892", {"start": v(41.71, -8.8) * mm, "end": v(41.8, -8.35) * mm});
            skLineSegment(sketch, "E893", {"start": v(41.8, -8.35) * mm, "end": v(41.88, -7.92) * mm});
            skLineSegment(sketch, "E894", {"start": v(41.88, -7.92) * mm, "end": v(41.96, -7.48) * mm});
            skLineSegment(sketch, "E895", {"start": v(41.96, -7.48) * mm, "end": v(42.05, -7.04) * mm});
            skLineSegment(sketch, "E896", {"start": v(42.05, -7.04) * mm, "end": v(42.13, -6.6) * mm});
            skLineSegment(sketch, "E897", {"start": v(42.13, -6.6) * mm, "end": v(42.21, -6.17) * mm});
            skLineSegment(sketch, "E898", {"start": v(42.21, -6.17) * mm, "end": v(42.3, -5.73) * mm});
            skLineSegment(sketch, "E899", {"start": v(42.3, -5.73) * mm, "end": v(42.38, -5.3) * mm});
            skLineSegment(sketch, "E900", {"start": v(42.38, -5.3) * mm, "end": v(42.44, -4.96) * mm});
            skLineSegment(sketch, "E901", {"start": v(42.44, -4.96) * mm, "end": v(42.88, -5.03) * mm});
            skLineSegment(sketch, "E902", {"start": v(42.88, -5.03) * mm, "end": v(43.32, -5.1) * mm});
            skLineSegment(sketch, "E903", {"start": v(43.32, -5.1) * mm, "end": v(43.76, -5.16) * mm});
            skLineSegment(sketch, "E904", {"start": v(43.76, -5.16) * mm, "end": v(44.2, -5.23) * mm});
            skLineSegment(sketch, "E905", {"start": v(44.2, -5.23) * mm, "end": v(44.65, -5.3) * mm});
            skLineSegment(sketch, "E906", {"start": v(44.65, -5.3) * mm, "end": v(45.09, -5.37) * mm});
            skLineSegment(sketch, "E907", {"start": v(45.09, -5.37) * mm, "end": v(45.53, -5.44) * mm});
            skLineSegment(sketch, "E908", {"start": v(45.53, -5.44) * mm, "end": v(45.97, -5.51) * mm});
            skLineSegment(sketch, "E909", {"start": v(45.97, -5.51) * mm, "end": v(46.4, -5.58) * mm});
            skLineSegment(sketch, "E910", {"start": v(46.4, -5.58) * mm, "end": v(46.85, -5.65) * mm});
            skLineSegment(sketch, "E911", {"start": v(46.85, -5.65) * mm, "end": v(47.29, -5.72) * mm});
            skLineSegment(sketch, "E912", {"start": v(47.29, -5.72) * mm, "end": v(47.73, -5.8) * mm});
            skLineSegment(sketch, "E913", {"start": v(47.73, -5.8) * mm, "end": v(48.17, -5.86) * mm});
            skLineSegment(sketch, "E914", {"start": v(48.17, -5.86) * mm, "end": v(48.6, -5.93) * mm});
            skLineSegment(sketch, "E915", {"start": v(48.6, -5.93) * mm, "end": v(49.05, -6) * mm});
            skLineSegment(sketch, "E916", {"start": v(49.05, -6) * mm, "end": v(49.49, -6.07) * mm});
            skLineSegment(sketch, "E917", {"start": v(49.49, -6.07) * mm, "end": v(49.63, -6.1) * mm});
            skLineSegment(sketch, "E918", {"start": v(49.63, -6.1) * mm, "end": v(49.68, -5.65) * mm});
            skLineSegment(sketch, "E919", {"start": v(49.68, -5.65) * mm, "end": v(49.72, -5.2) * mm});
            skLineSegment(sketch, "E920", {"start": v(49.72, -5.2) * mm, "end": v(49.77, -4.8) * mm});
            skLineSegment(sketch, "E921", {"start": v(49.77, -4.8) * mm, "end": v(49.35, -4.64) * mm});
            skLineSegment(sketch, "E922", {"start": v(49.35, -4.64) * mm, "end": v(48.93, -4.48) * mm});
            skLineSegment(sketch, "E923", {"start": v(48.93, -4.48) * mm, "end": v(48.52, -4.33) * mm});
            skLineSegment(sketch, "E924", {"start": v(48.52, -4.33) * mm, "end": v(48.1, -4.17) * mm});
            skLineSegment(sketch, "E925", {"start": v(48.1, -4.17) * mm, "end": v(47.68, -4.02) * mm});
            skLineSegment(sketch, "E926", {"start": v(47.68, -4.02) * mm, "end": v(47.26, -3.86) * mm});
            skLineSegment(sketch, "E927", {"start": v(47.26, -3.86) * mm, "end": v(46.85, -3.7) * mm});
            skLineSegment(sketch, "E928", {"start": v(46.85, -3.7) * mm, "end": v(46.43, -3.55) * mm});
            skLineSegment(sketch, "E929", {"start": v(46.43, -3.55) * mm, "end": v(46.01, -3.4) * mm});
            skLineSegment(sketch, "E930", {"start": v(46.01, -3.4) * mm, "end": v(45.6, -3.24) * mm});
            skLineSegment(sketch, "E931", {"start": v(45.6, -3.24) * mm, "end": v(45.18, -3.08) * mm});
            skLineSegment(sketch, "E932", {"start": v(45.18, -3.08) * mm, "end": v(44.76, -2.93) * mm});
            skLineSegment(sketch, "E933", {"start": v(44.76, -2.93) * mm, "end": v(44.34, -2.77) * mm});
            skLineSegment(sketch, "E934", {"start": v(44.34, -2.77) * mm, "end": v(43.92, -2.62) * mm});
            skLineSegment(sketch, "E935", {"start": v(43.92, -2.62) * mm, "end": v(43.5, -2.46) * mm});
            skLineSegment(sketch, "E936", {"start": v(43.5, -2.46) * mm, "end": v(43.09, -2.3) * mm});
            skLineSegment(sketch, "E937", {"start": v(43.09, -2.3) * mm, "end": v(42.68, -2.16) * mm});
            skLineSegment(sketch, "E938", {"start": v(42.68, -2.16) * mm, "end": v(42.67, -1.7) * mm});
            skLineSegment(sketch, "E939", {"start": v(42.67, -1.7) * mm, "end": v(42.66, -1.26) * mm});
            skLineSegment(sketch, "E940", {"start": v(42.66, -1.26) * mm, "end": v(42.65, -0.82) * mm});
            skLineSegment(sketch, "E941", {"start": v(42.65, -0.82) * mm, "end": v(42.64, -0.37) * mm});
            skLineSegment(sketch, "E942", {"start": v(42.64, -0.37) * mm, "end": v(42.63, 0.07) * mm});
            skLineSegment(sketch, "E943", {"start": v(42.63, 0.07) * mm, "end": v(42.62, 0.52) * mm});
            skLineSegment(sketch, "E944", {"start": v(42.62, 0.52) * mm, "end": v(42.61, 0.96) * mm});
            skLineSegment(sketch, "E945", {"start": v(42.61, 0.96) * mm, "end": v(42.6, 1.4) * mm});
            skLineSegment(sketch, "E946", {"start": v(42.6, 1.4) * mm, "end": v(42.6, 1.85) * mm});
            skLineSegment(sketch, "E947", {"start": v(42.6, 1.85) * mm, "end": v(42.58, 2.3) * mm});
            skLineSegment(sketch, "E948", {"start": v(42.58, 2.3) * mm, "end": v(42.57, 2.75) * mm});
            skLineSegment(sketch, "E949", {"start": v(42.57, 2.75) * mm, "end": v(42.56, 3.2) * mm});
            skLineSegment(sketch, "E950", {"start": v(42.56, 3.2) * mm, "end": v(42.55, 3.64) * mm});
            skLineSegment(sketch, "E951", {"start": v(42.55, 3.64) * mm, "end": v(42.55, 3.98) * mm});
            skLineSegment(sketch, "E952", {"start": v(42.55, 3.98) * mm, "end": v(43, 4) * mm});
            skLineSegment(sketch, "E953", {"start": v(43, 4) * mm, "end": v(43.44, 4.02) * mm});
            skLineSegment(sketch, "E954", {"start": v(43.44, 4.02) * mm, "end": v(43.88, 4.05) * mm});
            skLineSegment(sketch, "E955", {"start": v(43.88, 4.05) * mm, "end": v(44.33, 4.07) * mm});
            skLineSegment(sketch, "E956", {"start": v(44.33, 4.07) * mm, "end": v(44.77, 4.1) * mm});
            skLineSegment(sketch, "E957", {"start": v(44.77, 4.1) * mm, "end": v(45.22, 4.12) * mm});
            skLineSegment(sketch, "E958", {"start": v(45.22, 4.12) * mm, "end": v(45.66, 4.14) * mm});
            skLineSegment(sketch, "E959", {"start": v(45.66, 4.14) * mm, "end": v(46.1, 4.16) * mm});
            skLineSegment(sketch, "E960", {"start": v(46.1, 4.16) * mm, "end": v(46.55, 4.19) * mm});
            skLineSegment(sketch, "E961", {"start": v(46.55, 4.19) * mm, "end": v(47, 4.21) * mm});
            skLineSegment(sketch, "E962", {"start": v(47, 4.21) * mm, "end": v(47.44, 4.23) * mm});
            skLineSegment(sketch, "E963", {"start": v(47.44, 4.23) * mm, "end": v(47.89, 4.26) * mm});
            skLineSegment(sketch, "E964", {"start": v(47.89, 4.26) * mm, "end": v(48.33, 4.28) * mm});
            skLineSegment(sketch, "E965", {"start": v(48.33, 4.28) * mm, "end": v(48.78, 4.3) * mm});
            skLineSegment(sketch, "E966", {"start": v(48.78, 4.3) * mm, "end": v(49.22, 4.33) * mm});
            skLineSegment(sketch, "E967", {"start": v(49.22, 4.33) * mm, "end": v(49.67, 4.35) * mm});
            skLineSegment(sketch, "E968", {"start": v(49.67, 4.35) * mm, "end": v(49.8, 4.36) * mm});
            skLineSegment(sketch, "E969", {"start": v(49.8, 4.36) * mm, "end": v(49.77, 4.8) * mm});
            skLineSegment(sketch, "E970", {"start": v(49.77, 4.8) * mm, "end": v(49.72, 5.24) * mm});
            skLineSegment(sketch, "E971", {"start": v(49.72, 5.24) * mm, "end": v(49.68, 5.66) * mm});
            skLineSegment(sketch, "E972", {"start": v(49.68, 5.66) * mm, "end": v(49.24, 5.73) * mm});
            skLineSegment(sketch, "E973", {"start": v(49.24, 5.73) * mm, "end": v(48.8, 5.8) * mm});
            skLineSegment(sketch, "E974", {"start": v(48.8, 5.8) * mm, "end": v(48.36, 5.86) * mm});
            skLineSegment(sketch, "E975", {"start": v(48.36, 5.86) * mm, "end": v(47.92, 5.92) * mm});
            skLineSegment(sketch, "E976", {"start": v(47.92, 5.92) * mm, "end": v(47.47, 5.99) * mm});
            skLineSegment(sketch, "E977", {"start": v(47.47, 5.99) * mm, "end": v(47.03, 6.05) * mm});
            skLineSegment(sketch, "E978", {"start": v(47.03, 6.05) * mm, "end": v(46.6, 6.12) * mm});
            skLineSegment(sketch, "E979", {"start": v(46.6, 6.12) * mm, "end": v(46.15, 6.18) * mm});
            skLineSegment(sketch, "E980", {"start": v(46.15, 6.18) * mm, "end": v(45.71, 6.25) * mm});
            skLineSegment(sketch, "E981", {"start": v(45.71, 6.25) * mm, "end": v(45.27, 6.31) * mm});
            skLineSegment(sketch, "E982", {"start": v(45.27, 6.31) * mm, "end": v(44.83, 6.38) * mm});
            skLineSegment(sketch, "E983", {"start": v(44.83, 6.38) * mm, "end": v(44.39, 6.44) * mm});
            skLineSegment(sketch, "E984", {"start": v(44.39, 6.44) * mm, "end": v(43.95, 6.5) * mm});
            skLineSegment(sketch, "E985", {"start": v(43.95, 6.5) * mm, "end": v(43.5, 6.57) * mm});
            skLineSegment(sketch, "E986", {"start": v(43.5, 6.57) * mm, "end": v(43.07, 6.64) * mm});
            skLineSegment(sketch, "E987", {"start": v(43.07, 6.64) * mm, "end": v(42.63, 6.7) * mm});
            skLineSegment(sketch, "E988", {"start": v(42.63, 6.7) * mm, "end": v(42.2, 6.77) * mm});
            skLineSegment(sketch, "E989", {"start": v(42.2, 6.77) * mm, "end": v(42.1, 7.2) * mm});
            skLineSegment(sketch, "E990", {"start": v(42.1, 7.2) * mm, "end": v(41.99, 7.63) * mm});
            skLineSegment(sketch, "E991", {"start": v(41.99, 7.63) * mm, "end": v(41.89, 8.07) * mm});
            skLineSegment(sketch, "E992", {"start": v(41.89, 8.07) * mm, "end": v(41.79, 8.5) * mm});
            skLineSegment(sketch, "E993", {"start": v(41.79, 8.5) * mm, "end": v(41.68, 8.93) * mm});
            skLineSegment(sketch, "E994", {"start": v(41.68, 8.93) * mm, "end": v(41.58, 9.37) * mm});
            skLineSegment(sketch, "E995", {"start": v(41.58, 9.37) * mm, "end": v(41.48, 9.8) * mm});
            skLineSegment(sketch, "E996", {"start": v(41.48, 9.8) * mm, "end": v(41.38, 10.24) * mm});
            skLineSegment(sketch, "E997", {"start": v(41.38, 10.24) * mm, "end": v(41.28, 10.67) * mm});
            skLineSegment(sketch, "E998", {"start": v(41.28, 10.67) * mm, "end": v(41.17, 11.1) * mm});
            skLineSegment(sketch, "E999", {"start": v(41.17, 11.1) * mm, "end": v(41.07, 11.54) * mm});
            skLineSegment(sketch, "E1000", {"start": v(41.07, 11.54) * mm, "end": v(40.97, 11.97) * mm});
            skLineSegment(sketch, "E1001", {"start": v(40.97, 11.97) * mm, "end": v(40.87, 12.4) * mm});
            skLineSegment(sketch, "E1002", {"start": v(40.87, 12.4) * mm, "end": v(40.8, 12.74) * mm});
            skLineSegment(sketch, "E1003", {"start": v(40.8, 12.74) * mm, "end": v(41.22, 12.85) * mm});
            skLineSegment(sketch, "E1004", {"start": v(41.22, 12.85) * mm, "end": v(41.65, 12.97) * mm});
            skLineSegment(sketch, "E1005", {"start": v(41.65, 12.97) * mm, "end": v(42.08, 13.08) * mm});
            skLineSegment(sketch, "E1006", {"start": v(42.08, 13.08) * mm, "end": v(42.51, 13.2) * mm});
            skLineSegment(sketch, "E1007", {"start": v(42.51, 13.2) * mm, "end": v(42.94, 13.31) * mm});
            skLineSegment(sketch, "E1008", {"start": v(42.94, 13.31) * mm, "end": v(43.37, 13.43) * mm});
            skLineSegment(sketch, "E1009", {"start": v(43.37, 13.43) * mm, "end": v(43.8, 13.54) * mm});
            skLineSegment(sketch, "E1010", {"start": v(43.8, 13.54) * mm, "end": v(44.23, 13.66) * mm});
            skLineSegment(sketch, "E1011", {"start": v(44.23, 13.66) * mm, "end": v(44.66, 13.77) * mm});
            skLineSegment(sketch, "E1012", {"start": v(44.66, 13.77) * mm, "end": v(45.1, 13.89) * mm});
            skLineSegment(sketch, "E1013", {"start": v(45.1, 13.89) * mm, "end": v(45.53, 14) * mm});
            skLineSegment(sketch, "E1014", {"start": v(45.53, 14) * mm, "end": v(45.96, 14.12) * mm});
            skLineSegment(sketch, "E1015", {"start": v(45.96, 14.12) * mm, "end": v(46.39, 14.24) * mm});
            skLineSegment(sketch, "E1016", {"start": v(46.39, 14.24) * mm, "end": v(46.82, 14.35) * mm});
            skLineSegment(sketch, "E1017", {"start": v(46.82, 14.35) * mm, "end": v(47.25, 14.47) * mm});
            skLineSegment(sketch, "E1018", {"start": v(47.25, 14.47) * mm, "end": v(47.68, 14.58) * mm});
            skLineSegment(sketch, "E1019", {"start": v(47.68, 14.58) * mm, "end": v(47.82, 14.62) * mm});
            skLineSegment(sketch, "E1020", {"start": v(47.82, 14.62) * mm, "end": v(47.68, 15.04) * mm});
            skLineSegment(sketch, "E1021", {"start": v(47.68, 15.04) * mm, "end": v(47.54, 15.47) * mm});
            skLineSegment(sketch, "E1022", {"start": v(47.54, 15.47) * mm, "end": v(47.42, 15.87) * mm});
            skLineSegment(sketch, "E1023", {"start": v(47.42, 15.87) * mm, "end": v(46.97, 15.84) * mm});
            skLineSegment(sketch, "E1024", {"start": v(46.97, 15.84) * mm, "end": v(46.53, 15.8) * mm});
            skLineSegment(sketch, "E1025", {"start": v(46.53, 15.8) * mm, "end": v(46.08, 15.78) * mm});
            skLineSegment(sketch, "E1026", {"start": v(46.08, 15.78) * mm, "end": v(45.64, 15.75) * mm});
            skLineSegment(sketch, "E1027", {"start": v(45.64, 15.75) * mm, "end": v(45.2, 15.73) * mm});
            skLineSegment(sketch, "E1028", {"start": v(45.2, 15.73) * mm, "end": v(44.75, 15.7) * mm});
            skLineSegment(sketch, "E1029", {"start": v(44.75, 15.7) * mm, "end": v(44.3, 15.67) * mm});
            skLineSegment(sketch, "E1030", {"start": v(44.3, 15.67) * mm, "end": v(43.86, 15.64) * mm});
            skLineSegment(sketch, "E1031", {"start": v(43.86, 15.64) * mm, "end": v(43.41, 15.61) * mm});
            skLineSegment(sketch, "E1032", {"start": v(43.41, 15.61) * mm, "end": v(42.97, 15.59) * mm});
            skLineSegment(sketch, "E1033", {"start": v(42.97, 15.59) * mm, "end": v(42.52, 15.56) * mm});
            skLineSegment(sketch, "E1034", {"start": v(42.52, 15.56) * mm, "end": v(42.08, 15.53) * mm});
            skLineSegment(sketch, "E1035", {"start": v(42.08, 15.53) * mm, "end": v(41.63, 15.5) * mm});
            skLineSegment(sketch, "E1036", {"start": v(41.63, 15.5) * mm, "end": v(41.19, 15.47) * mm});
            skLineSegment(sketch, "E1037", {"start": v(41.19, 15.47) * mm, "end": v(40.75, 15.45) * mm});
            skLineSegment(sketch, "E1038", {"start": v(40.75, 15.45) * mm, "end": v(40.3, 15.42) * mm});
            skLineSegment(sketch, "E1039", {"start": v(40.3, 15.42) * mm, "end": v(39.87, 15.39) * mm});
            skLineSegment(sketch, "E1040", {"start": v(39.87, 15.39) * mm, "end": v(39.68, 15.8) * mm});
            skLineSegment(sketch, "E1041", {"start": v(39.68, 15.8) * mm, "end": v(39.49, 16.2) * mm});
            skLineSegment(sketch, "E1042", {"start": v(39.49, 16.2) * mm, "end": v(39.3, 16.6) * mm});
            skLineSegment(sketch, "E1043", {"start": v(39.3, 16.6) * mm, "end": v(39.1, 17) * mm});
            skLineSegment(sketch, "E1044", {"start": v(39.1, 17) * mm, "end": v(38.92, 17.4) * mm});
            skLineSegment(sketch, "E1045", {"start": v(38.92, 17.4) * mm, "end": v(38.73, 17.8) * mm});
            skLineSegment(sketch, "E1046", {"start": v(38.73, 17.8) * mm, "end": v(38.54, 18.21) * mm});
            skLineSegment(sketch, "E1047", {"start": v(38.54, 18.21) * mm, "end": v(38.35, 18.61) * mm});
            skLineSegment(sketch, "E1048", {"start": v(38.35, 18.61) * mm, "end": v(38.16, 19.02) * mm});
            skLineSegment(sketch, "E1049", {"start": v(38.16, 19.02) * mm, "end": v(37.97, 19.42) * mm});
            skLineSegment(sketch, "E1050", {"start": v(37.97, 19.42) * mm, "end": v(37.78, 19.82) * mm});
            skLineSegment(sketch, "E1051", {"start": v(37.78, 19.82) * mm, "end": v(37.59, 20.23) * mm});
            skLineSegment(sketch, "E1052", {"start": v(37.59, 20.23) * mm, "end": v(37.4, 20.63) * mm});
            skLineSegment(sketch, "E1053", {"start": v(37.4, 20.63) * mm, "end": v(37.25, 20.94) * mm});
            skLineSegment(sketch, "E1054", {"start": v(37.25, 20.94) * mm, "end": v(37.65, 21.14) * mm});
            skLineSegment(sketch, "E1055", {"start": v(37.65, 21.14) * mm, "end": v(38.05, 21.34) * mm});
            skLineSegment(sketch, "E1056", {"start": v(38.05, 21.34) * mm, "end": v(38.44, 21.55) * mm});
            skLineSegment(sketch, "E1057", {"start": v(38.44, 21.55) * mm, "end": v(38.84, 21.75) * mm});
            skLineSegment(sketch, "E1058", {"start": v(38.84, 21.75) * mm, "end": v(39.24, 21.95) * mm});
            skLineSegment(sketch, "E1059", {"start": v(39.24, 21.95) * mm, "end": v(39.63, 22.15) * mm});
            skLineSegment(sketch, "E1060", {"start": v(39.63, 22.15) * mm, "end": v(40.03, 22.35) * mm});
            skLineSegment(sketch, "E1061", {"start": v(40.03, 22.35) * mm, "end": v(40.43, 22.56) * mm});
            skLineSegment(sketch, "E1062", {"start": v(40.43, 22.56) * mm, "end": v(40.82, 22.76) * mm});
            skLineSegment(sketch, "E1063", {"start": v(40.82, 22.76) * mm, "end": v(41.22, 22.96) * mm});
            skLineSegment(sketch, "E1064", {"start": v(41.22, 22.96) * mm, "end": v(41.62, 23.16) * mm});
            skLineSegment(sketch, "E1065", {"start": v(41.62, 23.16) * mm, "end": v(42.02, 23.37) * mm});
            skLineSegment(sketch, "E1066", {"start": v(42.02, 23.37) * mm, "end": v(42.41, 23.57) * mm});
            skLineSegment(sketch, "E1067", {"start": v(42.41, 23.57) * mm, "end": v(42.8, 23.77) * mm});
            skLineSegment(sketch, "E1068", {"start": v(42.8, 23.77) * mm, "end": v(43.2, 23.97) * mm});
            skLineSegment(sketch, "E1069", {"start": v(43.2, 23.97) * mm, "end": v(43.6, 24.18) * mm});
            skLineSegment(sketch, "E1070", {"start": v(43.6, 24.18) * mm, "end": v(43.73, 24.24) * mm});
            skLineSegment(sketch, "E1071", {"start": v(43.73, 24.24) * mm, "end": v(43.5, 24.63) * mm});
            skLineSegment(sketch, "E1072", {"start": v(43.5, 24.63) * mm, "end": v(43.29, 25.01) * mm});
            skLineSegment(sketch, "E1073", {"start": v(43.29, 25.01) * mm, "end": v(43.08, 25.38) * mm});
            skLineSegment(sketch, "E1074", {"start": v(43.08, 25.38) * mm, "end": v(42.65, 25.26) * mm});
            skLineSegment(sketch, "E1075", {"start": v(42.65, 25.26) * mm, "end": v(42.22, 25.14) * mm});
            skLineSegment(sketch, "E1076", {"start": v(42.22, 25.14) * mm, "end": v(41.8, 25.02) * mm});
            skLineSegment(sketch, "E1077", {"start": v(41.8, 25.02) * mm, "end": v(41.36, 24.9) * mm});
            skLineSegment(sketch, "E1078", {"start": v(41.36, 24.9) * mm, "end": v(40.94, 24.78) * mm});
            skLineSegment(sketch, "E1079", {"start": v(40.94, 24.78) * mm, "end": v(40.5, 24.66) * mm});
            skLineSegment(sketch, "E1080", {"start": v(40.5, 24.66) * mm, "end": v(40.08, 24.54) * mm});
            skLineSegment(sketch, "E1081", {"start": v(40.08, 24.54) * mm, "end": v(39.65, 24.42) * mm});
            skLineSegment(sketch, "E1082", {"start": v(39.65, 24.42) * mm, "end": v(39.22, 24.3) * mm});
            skLineSegment(sketch, "E1083", {"start": v(39.22, 24.3) * mm, "end": v(38.79, 24.18) * mm});
            skLineSegment(sketch, "E1084", {"start": v(38.79, 24.18) * mm, "end": v(38.36, 24.06) * mm});
            skLineSegment(sketch, "E1085", {"start": v(38.36, 24.06) * mm, "end": v(37.93, 23.94) * mm});
            skLineSegment(sketch, "E1086", {"start": v(37.93, 23.94) * mm, "end": v(37.5, 23.82) * mm});
            skLineSegment(sketch, "E1087", {"start": v(37.5, 23.82) * mm, "end": v(37.07, 23.7) * mm});
            skLineSegment(sketch, "E1088", {"start": v(37.07, 23.7) * mm, "end": v(36.64, 23.58) * mm});
            skLineSegment(sketch, "E1089", {"start": v(36.64, 23.58) * mm, "end": v(36.21, 23.46) * mm});
            skLineSegment(sketch, "E1090", {"start": v(36.21, 23.46) * mm, "end": v(35.8, 23.34) * mm});
            skLineSegment(sketch, "E1091", {"start": v(35.8, 23.34) * mm, "end": v(35.52, 23.7) * mm});
            skLineSegment(sketch, "E1092", {"start": v(35.52, 23.7) * mm, "end": v(35.26, 24.05) * mm});
            skLineSegment(sketch, "E1093", {"start": v(35.26, 24.05) * mm, "end": v(34.99, 24.4) * mm});
            skLineSegment(sketch, "E1094", {"start": v(34.99, 24.4) * mm, "end": v(34.72, 24.76) * mm});
            skLineSegment(sketch, "E1095", {"start": v(34.72, 24.76) * mm, "end": v(34.45, 25.12) * mm});
            skLineSegment(sketch, "E1096", {"start": v(34.45, 25.12) * mm, "end": v(34.18, 25.47) * mm});
            skLineSegment(sketch, "E1097", {"start": v(34.18, 25.47) * mm, "end": v(33.9, 25.83) * mm});
            skLineSegment(sketch, "E1098", {"start": v(33.9, 25.83) * mm, "end": v(33.64, 26.18) * mm});
            skLineSegment(sketch, "E1099", {"start": v(33.64, 26.18) * mm, "end": v(33.37, 26.54) * mm});
            skLineSegment(sketch, "E1100", {"start": v(33.37, 26.54) * mm, "end": v(33.1, 26.9) * mm});
            skLineSegment(sketch, "E1101", {"start": v(33.1, 26.9) * mm, "end": v(32.83, 27.25) * mm});
            skLineSegment(sketch, "E1102", {"start": v(32.83, 27.25) * mm, "end": v(32.56, 27.6) * mm});
            skLineSegment(sketch, "E1103", {"start": v(32.56, 27.6) * mm, "end": v(32.29, 27.95) * mm});
            skLineSegment(sketch, "E1104", {"start": v(32.29, 27.95) * mm, "end": v(32.08, 28.23) * mm});
            skLineSegment(sketch, "E1105", {"start": v(32.08, 28.23) * mm, "end": v(32.43, 28.5) * mm});
            skLineSegment(sketch, "E1106", {"start": v(32.43, 28.5) * mm, "end": v(32.78, 28.79) * mm});
            skLineSegment(sketch, "E1107", {"start": v(32.78, 28.79) * mm, "end": v(33.12, 29.07) * mm});
            skLineSegment(sketch, "E1108", {"start": v(33.12, 29.07) * mm, "end": v(33.47, 29.35) * mm});
            skLineSegment(sketch, "E1109", {"start": v(33.47, 29.35) * mm, "end": v(33.82, 29.63) * mm});
            skLineSegment(sketch, "E1110", {"start": v(33.82, 29.63) * mm, "end": v(34.16, 29.9) * mm});
            skLineSegment(sketch, "E1111", {"start": v(34.16, 29.9) * mm, "end": v(34.5, 30.19) * mm});
            skLineSegment(sketch, "E1112", {"start": v(34.5, 30.19) * mm, "end": v(34.85, 30.47) * mm});
            skLineSegment(sketch, "E1113", {"start": v(34.85, 30.47) * mm, "end": v(35.2, 30.75) * mm});
            skLineSegment(sketch, "E1114", {"start": v(35.2, 30.75) * mm, "end": v(35.55, 31.03) * mm});
            skLineSegment(sketch, "E1115", {"start": v(35.55, 31.03) * mm, "end": v(35.9, 31.31) * mm});
            skLineSegment(sketch, "E1116", {"start": v(35.9, 31.31) * mm, "end": v(36.24, 31.6) * mm});
            skLineSegment(sketch, "E1117", {"start": v(36.24, 31.6) * mm, "end": v(36.59, 31.87) * mm});
            skLineSegment(sketch, "E1118", {"start": v(36.59, 31.87) * mm, "end": v(36.93, 32.15) * mm});
            skLineSegment(sketch, "E1119", {"start": v(36.93, 32.15) * mm, "end": v(37.28, 32.43) * mm});
            skLineSegment(sketch, "E1120", {"start": v(37.28, 32.43) * mm, "end": v(37.62, 32.71) * mm});
            skLineSegment(sketch, "E1121", {"start": v(37.62, 32.71) * mm, "end": v(37.74, 32.8) * mm});
            skLineSegment(sketch, "E1122", {"start": v(37.74, 32.8) * mm, "end": v(37.44, 33.14) * mm});
            skLineSegment(sketch, "E1123", {"start": v(37.44, 33.14) * mm, "end": v(37.14, 33.47) * mm});
            skLineSegment(sketch, "E1124", {"start": v(37.14, 33.47) * mm, "end": v(36.86, 33.78) * mm});
            skLineSegment(sketch, "E1125", {"start": v(36.86, 33.78) * mm, "end": v(36.47, 33.57) * mm});
            skLineSegment(sketch, "E1126", {"start": v(36.47, 33.57) * mm, "end": v(36.07, 33.37) * mm});
            skLineSegment(sketch, "E1127", {"start": v(36.07, 33.37) * mm, "end": v(35.68, 33.16) * mm});
            skLineSegment(sketch, "E1128", {"start": v(35.68, 33.16) * mm, "end": v(35.28, 32.95) * mm});
            skLineSegment(sketch, "E1129", {"start": v(35.28, 32.95) * mm, "end": v(34.89, 32.75) * mm});
            skLineSegment(sketch, "E1130", {"start": v(34.89, 32.75) * mm, "end": v(34.5, 32.54) * mm});
            skLineSegment(sketch, "E1131", {"start": v(34.5, 32.54) * mm, "end": v(34.1, 32.33) * mm});
            skLineSegment(sketch, "E1132", {"start": v(34.1, 32.33) * mm, "end": v(33.7, 32.13) * mm});
            skLineSegment(sketch, "E1133", {"start": v(33.7, 32.13) * mm, "end": v(33.3, 31.92) * mm});
            skLineSegment(sketch, "E1134", {"start": v(33.3, 31.92) * mm, "end": v(32.91, 31.71) * mm});
            skLineSegment(sketch, "E1135", {"start": v(32.91, 31.71) * mm, "end": v(32.52, 31.5) * mm});
            skLineSegment(sketch, "E1136", {"start": v(32.52, 31.5) * mm, "end": v(32.12, 31.3) * mm});
            skLineSegment(sketch, "E1137", {"start": v(32.12, 31.3) * mm, "end": v(31.73, 31.1) * mm});
            skLineSegment(sketch, "E1138", {"start": v(31.73, 31.1) * mm, "end": v(31.34, 30.89) * mm});
            skLineSegment(sketch, "E1139", {"start": v(31.34, 30.89) * mm, "end": v(30.94, 30.68) * mm});
            skLineSegment(sketch, "E1140", {"start": v(30.94, 30.68) * mm, "end": v(30.55, 30.48) * mm});
            skLineSegment(sketch, "E1141", {"start": v(30.55, 30.48) * mm, "end": v(30.16, 30.27) * mm});
            skLineSegment(sketch, "E1142", {"start": v(30.16, 30.27) * mm, "end": v(29.82, 30.57) * mm});
            skLineSegment(sketch, "E1143", {"start": v(29.82, 30.57) * mm, "end": v(29.48, 30.86) * mm});
            skLineSegment(sketch, "E1144", {"start": v(29.48, 30.86) * mm, "end": v(29.15, 31.15) * mm});
            skLineSegment(sketch, "E1145", {"start": v(29.15, 31.15) * mm, "end": v(28.8, 31.44) * mm});
            skLineSegment(sketch, "E1146", {"start": v(28.8, 31.44) * mm, "end": v(28.47, 31.73) * mm});
            skLineSegment(sketch, "E1147", {"start": v(28.47, 31.73) * mm, "end": v(28.13, 32.02) * mm});
            skLineSegment(sketch, "E1148", {"start": v(28.13, 32.02) * mm, "end": v(27.8, 32.31) * mm});
            skLineSegment(sketch, "E1149", {"start": v(27.8, 32.31) * mm, "end": v(27.46, 32.6) * mm});
            skLineSegment(sketch, "E1150", {"start": v(27.46, 32.6) * mm, "end": v(27.12, 32.9) * mm});
            skLineSegment(sketch, "E1151", {"start": v(27.12, 32.9) * mm, "end": v(26.78, 33.18) * mm});
            skLineSegment(sketch, "E1152", {"start": v(26.78, 33.18) * mm, "end": v(26.45, 33.48) * mm});
            skLineSegment(sketch, "E1153", {"start": v(26.45, 33.48) * mm, "end": v(26.1, 33.77) * mm});
            skLineSegment(sketch, "E1154", {"start": v(26.1, 33.77) * mm, "end": v(25.77, 34.06) * mm});
            skLineSegment(sketch, "E1155", {"start": v(25.77, 34.06) * mm, "end": v(25.51, 34.28) * mm});
            skLineSegment(sketch, "E1156", {"start": v(25.51, 34.28) * mm, "end": v(25.8, 34.63) * mm});
            skLineSegment(sketch, "E1157", {"start": v(25.8, 34.63) * mm, "end": v(26.07, 34.97) * mm});
            skLineSegment(sketch, "E1158", {"start": v(26.07, 34.97) * mm, "end": v(26.36, 35.32) * mm});
            skLineSegment(sketch, "E1159", {"start": v(26.36, 35.32) * mm, "end": v(26.64, 35.67) * mm});
            skLineSegment(sketch, "E1160", {"start": v(26.64, 35.67) * mm, "end": v(26.92, 36.01) * mm});
            skLineSegment(sketch, "E1161", {"start": v(26.92, 36.01) * mm, "end": v(27.2, 36.36) * mm});
            skLineSegment(sketch, "E1162", {"start": v(27.2, 36.36) * mm, "end": v(27.48, 36.7) * mm});
            skLineSegment(sketch, "E1163", {"start": v(27.48, 36.7) * mm, "end": v(27.76, 37.05) * mm});
            skLineSegment(sketch, "E1164", {"start": v(27.76, 37.05) * mm, "end": v(28.04, 37.4) * mm});
            skLineSegment(sketch, "E1165", {"start": v(28.04, 37.4) * mm, "end": v(28.32, 37.74) * mm});
            skLineSegment(sketch, "E1166", {"start": v(28.32, 37.74) * mm, "end": v(28.6, 38.09) * mm});
            skLineSegment(sketch, "E1167", {"start": v(28.6, 38.09) * mm, "end": v(28.88, 38.44) * mm});
            skLineSegment(sketch, "E1168", {"start": v(28.88, 38.44) * mm, "end": v(29.16, 38.78) * mm});
            skLineSegment(sketch, "E1169", {"start": v(29.16, 38.78) * mm, "end": v(29.44, 39.13) * mm});
            skLineSegment(sketch, "E1170", {"start": v(29.44, 39.13) * mm, "end": v(29.72, 39.47) * mm});
            skLineSegment(sketch, "E1171", {"start": v(29.72, 39.47) * mm, "end": v(30, 39.82) * mm});
            skLineSegment(sketch, "E1172", {"start": v(30, 39.82) * mm, "end": v(30.1, 39.93) * mm});
            skLineSegment(sketch, "E1173", {"start": v(30.1, 39.93) * mm, "end": v(29.73, 40.2) * mm});
            skLineSegment(sketch, "E1174", {"start": v(29.73, 40.2) * mm, "end": v(29.37, 40.46) * mm});
            skLineSegment(sketch, "E1175", {"start": v(29.37, 40.46) * mm, "end": v(29.04, 40.7) * mm});
            skLineSegment(sketch, "E1176", {"start": v(29.04, 40.7) * mm, "end": v(28.7, 40.42) * mm});
            skLineSegment(sketch, "E1177", {"start": v(28.7, 40.42) * mm, "end": v(28.35, 40.14) * mm});
            skLineSegment(sketch, "E1178", {"start": v(28.35, 40.14) * mm, "end": v(28, 39.85) * mm});
            skLineSegment(sketch, "E1179", {"start": v(28, 39.85) * mm, "end": v(27.66, 39.57) * mm});
            skLineSegment(sketch, "E1180", {"start": v(27.66, 39.57) * mm, "end": v(27.32, 39.29) * mm});
            skLineSegment(sketch, "E1181", {"start": v(27.32, 39.29) * mm, "end": v(26.98, 39) * mm});
            skLineSegment(sketch, "E1182", {"start": v(26.98, 39) * mm, "end": v(26.63, 38.72) * mm});
            skLineSegment(sketch, "E1183", {"start": v(26.63, 38.72) * mm, "end": v(26.29, 38.43) * mm});
            skLineSegment(sketch, "E1184", {"start": v(26.29, 38.43) * mm, "end": v(25.94, 38.15) * mm});
            skLineSegment(sketch, "E1185", {"start": v(25.94, 38.15) * mm, "end": v(25.6, 37.87) * mm});
            skLineSegment(sketch, "E1186", {"start": v(25.6, 37.87) * mm, "end": v(25.26, 37.58) * mm});
            skLineSegment(sketch, "E1187", {"start": v(25.26, 37.58) * mm, "end": v(24.91, 37.3) * mm});
            skLineSegment(sketch, "E1188", {"start": v(24.91, 37.3) * mm, "end": v(24.57, 37.01) * mm});
            skLineSegment(sketch, "E1189", {"start": v(24.57, 37.01) * mm, "end": v(24.23, 36.73) * mm});
            skLineSegment(sketch, "E1190", {"start": v(24.23, 36.73) * mm, "end": v(23.88, 36.44) * mm});
            skLineSegment(sketch, "E1191", {"start": v(23.88, 36.44) * mm, "end": v(23.54, 36.16) * mm});
            skLineSegment(sketch, "E1192", {"start": v(23.54, 36.16) * mm, "end": v(23.2, 35.88) * mm});
            skLineSegment(sketch, "E1193", {"start": v(23.2, 35.88) * mm, "end": v(22.82, 36.1) * mm});
            skLineSegment(sketch, "E1194", {"start": v(22.82, 36.1) * mm, "end": v(22.42, 36.31) * mm});
            skLineSegment(sketch, "E1195", {"start": v(22.42, 36.31) * mm, "end": v(22.03, 36.53) * mm});
            skLineSegment(sketch, "E1196", {"start": v(22.03, 36.53) * mm, "end": v(21.64, 36.74) * mm});
            skLineSegment(sketch, "E1197", {"start": v(21.64, 36.74) * mm, "end": v(21.25, 36.96) * mm});
            skLineSegment(sketch, "E1198", {"start": v(21.25, 36.96) * mm, "end": v(20.86, 37.17) * mm});
            skLineSegment(sketch, "E1199", {"start": v(20.86, 37.17) * mm, "end": v(20.47, 37.38) * mm});
            skLineSegment(sketch, "E1200", {"start": v(20.47, 37.38) * mm, "end": v(20.08, 37.6) * mm});
            skLineSegment(sketch, "E1201", {"start": v(20.08, 37.6) * mm, "end": v(19.7, 37.81) * mm});
            skLineSegment(sketch, "E1202", {"start": v(19.7, 37.81) * mm, "end": v(19.3, 38.03) * mm});
            skLineSegment(sketch, "E1203", {"start": v(19.3, 38.03) * mm, "end": v(18.9, 38.24) * mm});
            skLineSegment(sketch, "E1204", {"start": v(18.9, 38.24) * mm, "end": v(18.52, 38.46) * mm});
            skLineSegment(sketch, "E1205", {"start": v(18.52, 38.46) * mm, "end": v(18.13, 38.67) * mm});
            skLineSegment(sketch, "E1206", {"start": v(18.13, 38.67) * mm, "end": v(17.83, 38.84) * mm});
            skLineSegment(sketch, "E1207", {"start": v(17.83, 38.84) * mm, "end": v(18.03, 39.23) * mm});
            skLineSegment(sketch, "E1208", {"start": v(18.03, 39.23) * mm, "end": v(18.23, 39.63) * mm});
            skLineSegment(sketch, "E1209", {"start": v(18.23, 39.63) * mm, "end": v(18.44, 40.03) * mm});
            skLineSegment(sketch, "E1210", {"start": v(18.44, 40.03) * mm, "end": v(18.64, 40.42) * mm});
            skLineSegment(sketch, "E1211", {"start": v(18.64, 40.42) * mm, "end": v(18.84, 40.82) * mm});
            skLineSegment(sketch, "E1212", {"start": v(18.84, 40.82) * mm, "end": v(19.04, 41.22) * mm});
            skLineSegment(sketch, "E1213", {"start": v(19.04, 41.22) * mm, "end": v(19.25, 41.61) * mm});
            skLineSegment(sketch, "E1214", {"start": v(19.25, 41.61) * mm, "end": v(19.45, 42.01) * mm});
            skLineSegment(sketch, "E1215", {"start": v(19.45, 42.01) * mm, "end": v(19.65, 42.4) * mm});
            skLineSegment(sketch, "E1216", {"start": v(19.65, 42.4) * mm, "end": v(19.85, 42.8) * mm});
            skLineSegment(sketch, "E1217", {"start": v(19.85, 42.8) * mm, "end": v(20.05, 43.2) * mm});
            skLineSegment(sketch, "E1218", {"start": v(20.05, 43.2) * mm, "end": v(20.26, 43.6) * mm});
            skLineSegment(sketch, "E1219", {"start": v(20.26, 43.6) * mm, "end": v(20.46, 44) * mm});
            skLineSegment(sketch, "E1220", {"start": v(20.46, 44) * mm, "end": v(20.66, 44.4) * mm});
            skLineSegment(sketch, "E1221", {"start": v(20.66, 44.4) * mm, "end": v(20.86, 44.8) * mm});
            skLineSegment(sketch, "E1222", {"start": v(20.86, 44.8) * mm, "end": v(21.07, 45.19) * mm});
            skLineSegment(sketch, "E1223", {"start": v(21.07, 45.19) * mm, "end": v(21.13, 45.32) * mm});
            skLineSegment(sketch, "E1224", {"start": v(21.13, 45.32) * mm, "end": v(20.72, 45.5) * mm});
            skLineSegment(sketch, "E1225", {"start": v(20.72, 45.5) * mm, "end": v(20.32, 45.68) * mm});
            skLineSegment(sketch, "E1226", {"start": v(20.32, 45.68) * mm, "end": v(19.94, 45.85) * mm});
            skLineSegment(sketch, "E1227", {"start": v(19.94, 45.85) * mm, "end": v(19.66, 45.5) * mm});
            skLineSegment(sketch, "E1228", {"start": v(19.66, 45.5) * mm, "end": v(19.38, 45.15) * mm});
            skLineSegment(sketch, "E1229", {"start": v(19.38, 45.15) * mm, "end": v(19.1, 44.8) * mm});
            skLineSegment(sketch, "E1230", {"start": v(19.1, 44.8) * mm, "end": v(18.83, 44.46) * mm});
            skLineSegment(sketch, "E1231", {"start": v(18.83, 44.46) * mm, "end": v(18.55, 44.1) * mm});
            skLineSegment(sketch, "E1232", {"start": v(18.55, 44.1) * mm, "end": v(18.28, 43.76) * mm});
            skLineSegment(sketch, "E1233", {"start": v(18.28, 43.76) * mm, "end": v(18, 43.4) * mm});
            skLineSegment(sketch, "E1234", {"start": v(18, 43.4) * mm, "end": v(17.72, 43.06) * mm});
            skLineSegment(sketch, "E1235", {"start": v(17.72, 43.06) * mm, "end": v(17.45, 42.7) * mm});
            skLineSegment(sketch, "E1236", {"start": v(17.45, 42.7) * mm, "end": v(17.17, 42.36) * mm});
            skLineSegment(sketch, "E1237", {"start": v(17.17, 42.36) * mm, "end": v(16.9, 42.01) * mm});
            skLineSegment(sketch, "E1238", {"start": v(16.9, 42.01) * mm, "end": v(16.62, 41.66) * mm});
            skLineSegment(sketch, "E1239", {"start": v(16.62, 41.66) * mm, "end": v(16.34, 41.31) * mm});
            skLineSegment(sketch, "E1240", {"start": v(16.34, 41.31) * mm, "end": v(16.06, 40.96) * mm});
            skLineSegment(sketch, "E1241", {"start": v(16.06, 40.96) * mm, "end": v(15.79, 40.61) * mm});
            skLineSegment(sketch, "E1242", {"start": v(15.79, 40.61) * mm, "end": v(15.5, 40.27) * mm});
            skLineSegment(sketch, "E1243", {"start": v(15.5, 40.27) * mm, "end": v(15.24, 39.92) * mm});
            skLineSegment(sketch, "E1244", {"start": v(15.24, 39.92) * mm, "end": v(14.81, 40.05) * mm});
            skLineSegment(sketch, "E1245", {"start": v(14.81, 40.05) * mm, "end": v(14.38, 40.18) * mm});
            skLineSegment(sketch, "E1246", {"start": v(14.38, 40.18) * mm, "end": v(13.96, 40.3) * mm});
            skLineSegment(sketch, "E1247", {"start": v(13.96, 40.3) * mm, "end": v(13.53, 40.44) * mm});
            skLineSegment(sketch, "E1248", {"start": v(13.53, 40.44) * mm, "end": v(13.1, 40.57) * mm});
            skLineSegment(sketch, "E1249", {"start": v(13.1, 40.57) * mm, "end": v(12.68, 40.7) * mm});
            skLineSegment(sketch, "E1250", {"start": v(12.68, 40.7) * mm, "end": v(12.25, 40.82) * mm});
            skLineSegment(sketch, "E1251", {"start": v(12.25, 40.82) * mm, "end": v(11.82, 40.95) * mm});
            skLineSegment(sketch, "E1252", {"start": v(11.82, 40.95) * mm, "end": v(11.4, 41.08) * mm});
            skLineSegment(sketch, "E1253", {"start": v(11.4, 41.08) * mm, "end": v(10.97, 41.2) * mm});
            skLineSegment(sketch, "E1254", {"start": v(10.97, 41.2) * mm, "end": v(10.54, 41.34) * mm});
            skLineSegment(sketch, "E1255", {"start": v(10.54, 41.34) * mm, "end": v(10.12, 41.47) * mm});
            skLineSegment(sketch, "E1256", {"start": v(10.12, 41.47) * mm, "end": v(9.7, 41.6) * mm});
            skLineSegment(sketch, "E1257", {"start": v(9.7, 41.6) * mm, "end": v(9.37, 41.7) * mm});
            skLineSegment(sketch, "E1258", {"start": v(9.37, 41.7) * mm, "end": v(9.48, 42.12) * mm});
            skLineSegment(sketch, "E1259", {"start": v(9.48, 42.12) * mm, "end": v(9.6, 42.55) * mm});
            skLineSegment(sketch, "E1260", {"start": v(9.6, 42.55) * mm, "end": v(9.71, 42.99) * mm});
            skLineSegment(sketch, "E1261", {"start": v(9.71, 42.99) * mm, "end": v(9.83, 43.42) * mm});
            skLineSegment(sketch, "E1262", {"start": v(9.83, 43.42) * mm, "end": v(9.94, 43.85) * mm});
            skLineSegment(sketch, "E1263", {"start": v(9.94, 43.85) * mm, "end": v(10.06, 44.28) * mm});
            skLineSegment(sketch, "E1264", {"start": v(10.06, 44.28) * mm, "end": v(10.17, 44.7) * mm});
            skLineSegment(sketch, "E1265", {"start": v(10.17, 44.7) * mm, "end": v(10.29, 45.14) * mm});
            skLineSegment(sketch, "E1266", {"start": v(10.29, 45.14) * mm, "end": v(10.4, 45.57) * mm});
            skLineSegment(sketch, "E1267", {"start": v(10.4, 45.57) * mm, "end": v(10.52, 46) * mm});
            skLineSegment(sketch, "E1268", {"start": v(10.52, 46) * mm, "end": v(10.63, 46.43) * mm});
            skLineSegment(sketch, "E1269", {"start": v(10.63, 46.43) * mm, "end": v(10.75, 46.86) * mm});
            skLineSegment(sketch, "E1270", {"start": v(10.75, 46.86) * mm, "end": v(10.86, 47.29) * mm});
            skLineSegment(sketch, "E1271", {"start": v(10.86, 47.29) * mm, "end": v(10.98, 47.72) * mm});
            skLineSegment(sketch, "E1272", {"start": v(10.98, 47.72) * mm, "end": v(11.1, 48.15) * mm});
            skLineSegment(sketch, "E1273", {"start": v(11.1, 48.15) * mm, "end": v(11.21, 48.58) * mm});
            skLineSegment(sketch, "E1274", {"start": v(11.21, 48.58) * mm, "end": v(11.25, 48.72) * mm});
            skLineSegment(sketch, "E1275", {"start": v(11.25, 48.72) * mm, "end": v(10.81, 48.81) * mm});
            skLineSegment(sketch, "E1276", {"start": v(10.81, 48.81) * mm, "end": v(10.38, 48.9) * mm});
            skLineSegment(sketch, "E1277", {"start": v(10.38, 48.9) * mm, "end": v(9.97, 49) * mm});
            skLineSegment(sketch, "E1278", {"start": v(9.97, 49) * mm, "end": v(9.77, 48.6) * mm});
            skLineSegment(sketch, "E1279", {"start": v(9.77, 48.6) * mm, "end": v(9.57, 48.2) * mm});
            skLineSegment(sketch, "E1280", {"start": v(9.57, 48.2) * mm, "end": v(9.37, 47.8) * mm});
            skLineSegment(sketch, "E1281", {"start": v(9.37, 47.8) * mm, "end": v(9.18, 47.4) * mm});
            skLineSegment(sketch, "E1282", {"start": v(9.18, 47.4) * mm, "end": v(8.98, 47) * mm});
            skLineSegment(sketch, "E1283", {"start": v(8.98, 47) * mm, "end": v(8.78, 46.6) * mm});
            skLineSegment(sketch, "E1284", {"start": v(8.78, 46.6) * mm, "end": v(8.58, 46.2) * mm});
            skLineSegment(sketch, "E1285", {"start": v(8.58, 46.2) * mm, "end": v(8.38, 45.8) * mm});
            skLineSegment(sketch, "E1286", {"start": v(8.38, 45.8) * mm, "end": v(8.19, 45.4) * mm});
            skLineSegment(sketch, "E1287", {"start": v(8.19, 45.4) * mm, "end": v(7.99, 45) * mm});
            skLineSegment(sketch, "E1288", {"start": v(7.99, 45) * mm, "end": v(7.79, 44.6) * mm});
            skLineSegment(sketch, "E1289", {"start": v(7.79, 44.6) * mm, "end": v(7.6, 44.2) * mm});
            skLineSegment(sketch, "E1290", {"start": v(7.6, 44.2) * mm, "end": v(7.4, 43.8) * mm});
            skLineSegment(sketch, "E1291", {"start": v(7.4, 43.8) * mm, "end": v(7.2, 43.4) * mm});
            skLineSegment(sketch, "E1292", {"start": v(7.2, 43.4) * mm, "end": v(7, 43) * mm});
            skLineSegment(sketch, "E1293", {"start": v(7, 43) * mm, "end": v(6.8, 42.6) * mm});
            skLineSegment(sketch, "E1294", {"start": v(6.8, 42.6) * mm, "end": v(6.6, 42.22) * mm});
            skLineSegment(sketch, "E1295", {"start": v(6.6, 42.22) * mm, "end": v(6.16, 42.26) * mm});
            skLineSegment(sketch, "E1296", {"start": v(6.16, 42.26) * mm, "end": v(5.72, 42.3) * mm});
            skLineSegment(sketch, "E1297", {"start": v(5.72, 42.3) * mm, "end": v(5.27, 42.33) * mm});
            skLineSegment(sketch, "E1298", {"start": v(5.27, 42.33) * mm, "end": v(4.83, 42.37) * mm});
            skLineSegment(sketch, "E1299", {"start": v(4.83, 42.37) * mm, "end": v(4.38, 42.4) * mm});
            skLineSegment(sketch, "E1300", {"start": v(4.38, 42.4) * mm, "end": v(3.94, 42.44) * mm});
            skLineSegment(sketch, "E1301", {"start": v(3.94, 42.44) * mm, "end": v(3.5, 42.48) * mm});
            skLineSegment(sketch, "E1302", {"start": v(3.5, 42.48) * mm, "end": v(3.05, 42.52) * mm});
            skLineSegment(sketch, "E1303", {"start": v(3.05, 42.52) * mm, "end": v(2.6, 42.55) * mm});
            skLineSegment(sketch, "E1304", {"start": v(2.6, 42.55) * mm, "end": v(2.16, 42.6) * mm});
            skLineSegment(sketch, "E1305", {"start": v(2.16, 42.6) * mm, "end": v(1.72, 42.63) * mm});
            skLineSegment(sketch, "E1306", {"start": v(1.72, 42.63) * mm, "end": v(1.28, 42.66) * mm});
            skLineSegment(sketch, "E1307", {"start": v(1.28, 42.66) * mm, "end": v(0.83, 42.7) * mm});
            skLineSegment(sketch, "E1308", {"start": v(0.83, 42.7) * mm, "end": v(0.5, 42.73) * mm});
            skLineSegment(sketch, "E1309", {"start": v(0.5, 42.73) * mm, "end": v(0.52, 43.17) * mm});
            skLineSegment(sketch, "E1310", {"start": v(0.52, 43.17) * mm, "end": v(0.54, 43.62) * mm});
            skLineSegment(sketch, "E1311", {"start": v(0.54, 43.62) * mm, "end": v(0.56, 44.06) * mm});
            skLineSegment(sketch, "E1312", {"start": v(0.56, 44.06) * mm, "end": v(0.59, 44.5) * mm});
            skLineSegment(sketch, "E1313", {"start": v(0.59, 44.5) * mm, "end": v(0.6, 44.95) * mm});
            skLineSegment(sketch, "E1314", {"start": v(0.6, 44.95) * mm, "end": v(0.63, 45.4) * mm});
            skLineSegment(sketch, "E1315", {"start": v(0.63, 45.4) * mm, "end": v(0.66, 45.84) * mm});
            skLineSegment(sketch, "E1316", {"start": v(0.66, 45.84) * mm, "end": v(0.68, 46.29) * mm});
            skLineSegment(sketch, "E1317", {"start": v(0.68, 46.29) * mm, "end": v(0.7, 46.73) * mm});
            skLineSegment(sketch, "E1318", {"start": v(0.7, 46.73) * mm, "end": v(0.73, 47.18) * mm});
            skLineSegment(sketch, "E1319", {"start": v(0.73, 47.18) * mm, "end": v(0.75, 47.62) * mm});
            skLineSegment(sketch, "E1320", {"start": v(0.75, 47.62) * mm, "end": v(0.77, 48.07) * mm});
            skLineSegment(sketch, "E1321", {"start": v(0.77, 48.07) * mm, "end": v(0.8, 48.52) * mm});
            skLineSegment(sketch, "E1322", {"start": v(0.8, 48.52) * mm, "end": v(0.82, 48.96) * mm});
            skLineSegment(sketch, "E1323", {"start": v(0.82, 48.96) * mm, "end": v(0.84, 49.4) * mm});
            skLineSegment(sketch, "E1324", {"start": v(0.84, 49.4) * mm, "end": v(0.87, 49.85) * mm});
            skLineSegment(sketch, "E1325", {"start": v(0.87, 49.85) * mm, "end": v(0.87, 50) * mm});
            skLineSegment(sketch, "E1326", {"start": v(0.87, 50) * mm, "end": v(0.43, 50) * mm});
            skLineSegment(sketch, "E1327", {"start": v(0.43, 50) * mm, "end": v(-0.02, 50) * mm});
            skLineSegment(sketch, "E1328", {"start": v(-0.02, 50) * mm, "end": v(-0.44, 50) * mm});
            skLineSegment(sketch, "E1329", {"start": v(-0.44, 50) * mm, "end": v(-0.55, 49.57) * mm});
            skLineSegment(sketch, "E1330", {"start": v(-0.55, 49.57) * mm, "end": v(-0.66, 49.13) * mm});
            skLineSegment(sketch, "E1331", {"start": v(-0.66, 49.13) * mm, "end": v(-0.77, 48.7) * mm});
            skLineSegment(sketch, "E1332", {"start": v(-0.77, 48.7) * mm, "end": v(-0.88, 48.27) * mm});
            skLineSegment(sketch, "E1333", {"start": v(-0.88, 48.27) * mm, "end": v(-1, 47.84) * mm});
            skLineSegment(sketch, "E1334", {"start": v(-1, 47.84) * mm, "end": v(-1.1, 47.4) * mm});
            skLineSegment(sketch, "E1335", {"start": v(-1.1, 47.4) * mm, "end": v(-1.21, 46.98) * mm});
            skLineSegment(sketch, "E1336", {"start": v(-1.21, 46.98) * mm, "end": v(-1.32, 46.55) * mm});
            skLineSegment(sketch, "E1337", {"start": v(-1.32, 46.55) * mm, "end": v(-1.43, 46.11) * mm});
            skLineSegment(sketch, "E1338", {"start": v(-1.43, 46.11) * mm, "end": v(-1.54, 45.68) * mm});
            skLineSegment(sketch, "E1339", {"start": v(-1.54, 45.68) * mm, "end": v(-1.66, 45.25) * mm});
            skLineSegment(sketch, "E1340", {"start": v(-1.66, 45.25) * mm, "end": v(-1.77, 44.82) * mm});
            skLineSegment(sketch, "E1341", {"start": v(-1.77, 44.82) * mm, "end": v(-1.88, 44.39) * mm});
            skLineSegment(sketch, "E1342", {"start": v(-1.88, 44.39) * mm, "end": v(-1.99, 43.96) * mm});
            skLineSegment(sketch, "E1343", {"start": v(-1.99, 43.96) * mm, "end": v(-2.1, 43.52) * mm});
            skLineSegment(sketch, "E1344", {"start": v(-2.1, 43.52) * mm, "end": v(-2.2, 43.1) * mm});
            skLineSegment(sketch, "E1345", {"start": v(-2.2, 43.1) * mm, "end": v(-2.32, 42.67) * mm});
            skLineSegment(sketch, "E1346", {"start": v(-2.32, 42.67) * mm, "end": v(-2.76, 42.61) * mm});
            skLineSegment(sketch, "E1347", {"start": v(-2.76, 42.61) * mm, "end": v(-3.2, 42.56) * mm});
            skLineSegment(sketch, "E1348", {"start": v(-3.2, 42.56) * mm, "end": v(-3.64, 42.5) * mm});
            skLineSegment(sketch, "E1349", {"start": v(-3.64, 42.5) * mm, "end": v(-4.09, 42.45) * mm});
            skLineSegment(sketch, "E1350", {"start": v(-4.09, 42.45) * mm, "end": v(-4.53, 42.39) * mm});
            skLineSegment(sketch, "E1351", {"start": v(-4.53, 42.39) * mm, "end": v(-4.97, 42.33) * mm});
            skLineSegment(sketch, "E1352", {"start": v(-4.97, 42.33) * mm, "end": v(-5.41, 42.28) * mm});
            skLineSegment(sketch, "E1353", {"start": v(-5.41, 42.28) * mm, "end": v(-5.85, 42.22) * mm});
            skLineSegment(sketch, "E1354", {"start": v(-5.85, 42.22) * mm, "end": v(-6.3, 42.17) * mm});
            skLineSegment(sketch, "E1355", {"start": v(-6.3, 42.17) * mm, "end": v(-6.74, 42.1) * mm});
            skLineSegment(sketch, "E1356", {"start": v(-6.74, 42.1) * mm, "end": v(-7.18, 42.05) * mm});
            skLineSegment(sketch, "E1357", {"start": v(-7.18, 42.05) * mm, "end": v(-7.62, 42) * mm});
            skLineSegment(sketch, "E1358", {"start": v(-7.62, 42) * mm, "end": v(-8.06, 41.94) * mm});
            skLineSegment(sketch, "E1359", {"start": v(-8.06, 41.94) * mm, "end": v(-8.4, 41.9) * mm});
            skLineSegment(sketch, "E1360", {"start": v(-8.4, 41.9) * mm, "end": v(-8.47, 42.34) * mm});
            skLineSegment(sketch, "E1361", {"start": v(-8.47, 42.34) * mm, "end": v(-8.54, 42.78) * mm});
            skLineSegment(sketch, "E1362", {"start": v(-8.54, 42.78) * mm, "end": v(-8.61, 43.22) * mm});
            skLineSegment(sketch, "E1363", {"start": v(-8.61, 43.22) * mm, "end": v(-8.68, 43.66) * mm});
            skLineSegment(sketch, "E1364", {"start": v(-8.68, 43.66) * mm, "end": v(-8.75, 44.1) * mm});
            skLineSegment(sketch, "E1365", {"start": v(-8.75, 44.1) * mm, "end": v(-8.82, 44.54) * mm});
            skLineSegment(sketch, "E1366", {"start": v(-8.82, 44.54) * mm, "end": v(-8.9, 44.98) * mm});
            skLineSegment(sketch, "E1367", {"start": v(-8.9, 44.98) * mm, "end": v(-8.96, 45.42) * mm});
            skLineSegment(sketch, "E1368", {"start": v(-8.96, 45.42) * mm, "end": v(-9.03, 45.86) * mm});
            skLineSegment(sketch, "E1369", {"start": v(-9.03, 45.86) * mm, "end": v(-9.1, 46.3) * mm});
            skLineSegment(sketch, "E1370", {"start": v(-9.1, 46.3) * mm, "end": v(-9.17, 46.74) * mm});
            skLineSegment(sketch, "E1371", {"start": v(-9.17, 46.74) * mm, "end": v(-9.24, 47.18) * mm});
            skLineSegment(sketch, "E1372", {"start": v(-9.24, 47.18) * mm, "end": v(-9.3, 47.62) * mm});
            skLineSegment(sketch, "E1373", {"start": v(-9.3, 47.62) * mm, "end": v(-9.38, 48.06) * mm});
            skLineSegment(sketch, "E1374", {"start": v(-9.38, 48.06) * mm, "end": v(-9.45, 48.5) * mm});
            skLineSegment(sketch, "E1375", {"start": v(-9.45, 48.5) * mm, "end": v(-9.52, 48.94) * mm});
            skLineSegment(sketch, "E1376", {"start": v(-9.52, 48.94) * mm, "end": v(-9.54, 49.08) * mm});
            skLineSegment(sketch, "E1377", {"start": v(-9.54, 49.08) * mm, "end": v(-9.98, 49) * mm});
            skLineSegment(sketch, "E1378", {"start": v(-9.98, 49) * mm, "end": v(-10.41, 48.9) * mm});
            skLineSegment(sketch, "E1379", {"start": v(-10.41, 48.9) * mm, "end": v(-10.82, 48.81) * mm});
            skLineSegment(sketch, "E1380", {"start": v(-10.82, 48.81) * mm, "end": v(-10.84, 48.37) * mm});
            skLineSegment(sketch, "E1381", {"start": v(-10.84, 48.37) * mm, "end": v(-10.86, 47.92) * mm});
            skLineSegment(sketch, "E1382", {"start": v(-10.86, 47.92) * mm, "end": v(-10.88, 47.48) * mm});
            skLineSegment(sketch, "E1383", {"start": v(-10.88, 47.48) * mm, "end": v(-10.9, 47.03) * mm});
            skLineSegment(sketch, "E1384", {"start": v(-10.9, 47.03) * mm, "end": v(-10.92, 46.59) * mm});
            skLineSegment(sketch, "E1385", {"start": v(-10.92, 46.59) * mm, "end": v(-10.93, 46.14) * mm});
            skLineSegment(sketch, "E1386", {"start": v(-10.93, 46.14) * mm, "end": v(-10.95, 45.7) * mm});
            skLineSegment(sketch, "E1387", {"start": v(-10.95, 45.7) * mm, "end": v(-10.97, 45.25) * mm});
            skLineSegment(sketch, "E1388", {"start": v(-10.97, 45.25) * mm, "end": v(-10.99, 44.8) * mm});
            skLineSegment(sketch, "E1389", {"start": v(-10.99, 44.8) * mm, "end": v(-11, 44.36) * mm});
            skLineSegment(sketch, "E1390", {"start": v(-11, 44.36) * mm, "end": v(-11.03, 43.92) * mm});
            skLineSegment(sketch, "E1391", {"start": v(-11.03, 43.92) * mm, "end": v(-11.05, 43.47) * mm});
            skLineSegment(sketch, "E1392", {"start": v(-11.05, 43.47) * mm, "end": v(-11.06, 43.03) * mm});
            skLineSegment(sketch, "E1393", {"start": v(-11.06, 43.03) * mm, "end": v(-11.08, 42.58) * mm});
            skLineSegment(sketch, "E1394", {"start": v(-11.08, 42.58) * mm, "end": v(-11.1, 42.14) * mm});
            skLineSegment(sketch, "E1395", {"start": v(-11.1, 42.14) * mm, "end": v(-11.12, 41.7) * mm});
            skLineSegment(sketch, "E1396", {"start": v(-11.12, 41.7) * mm, "end": v(-11.14, 41.26) * mm});
            skLineSegment(sketch, "E1397", {"start": v(-11.14, 41.26) * mm, "end": v(-11.56, 41.1) * mm});
            skLineSegment(sketch, "E1398", {"start": v(-11.56, 41.1) * mm, "end": v(-11.98, 40.96) * mm});
            skLineSegment(sketch, "E1399", {"start": v(-11.98, 40.96) * mm, "end": v(-12.4, 40.82) * mm});
            skLineSegment(sketch, "E1400", {"start": v(-12.4, 40.82) * mm, "end": v(-12.82, 40.67) * mm});
            skLineSegment(sketch, "E1401", {"start": v(-12.82, 40.67) * mm, "end": v(-13.24, 40.52) * mm});
            skLineSegment(sketch, "E1402", {"start": v(-13.24, 40.52) * mm, "end": v(-13.66, 40.38) * mm});
            skLineSegment(sketch, "E1403", {"start": v(-13.66, 40.38) * mm, "end": v(-14.08, 40.23) * mm});
            skLineSegment(sketch, "E1404", {"start": v(-14.08, 40.23) * mm, "end": v(-14.5, 40.08) * mm});
            skLineSegment(sketch, "E1405", {"start": v(-14.5, 40.08) * mm, "end": v(-14.93, 39.93) * mm});
            skLineSegment(sketch, "E1406", {"start": v(-14.93, 39.93) * mm, "end": v(-15.35, 39.79) * mm});
            skLineSegment(sketch, "E1407", {"start": v(-15.35, 39.79) * mm, "end": v(-15.77, 39.64) * mm});
            skLineSegment(sketch, "E1408", {"start": v(-15.77, 39.64) * mm, "end": v(-16.19, 39.5) * mm});
            skLineSegment(sketch, "E1409", {"start": v(-16.19, 39.5) * mm, "end": v(-16.6, 39.35) * mm});
            skLineSegment(sketch, "E1410", {"start": v(-16.6, 39.35) * mm, "end": v(-16.93, 39.24) * mm});
            skLineSegment(sketch, "E1411", {"start": v(-16.93, 39.24) * mm, "end": v(-17.09, 39.65) * mm});
            skLineSegment(sketch, "E1412", {"start": v(-17.09, 39.65) * mm, "end": v(-17.25, 40.07) * mm});
            skLineSegment(sketch, "E1413", {"start": v(-17.25, 40.07) * mm, "end": v(-17.4, 40.48) * mm});
            skLineSegment(sketch, "E1414", {"start": v(-17.4, 40.48) * mm, "end": v(-17.57, 40.9) * mm});
            skLineSegment(sketch, "E1415", {"start": v(-17.57, 40.9) * mm, "end": v(-17.73, 41.32) * mm});
            skLineSegment(sketch, "E1416", {"start": v(-17.73, 41.32) * mm, "end": v(-17.89, 41.73) * mm});
            skLineSegment(sketch, "E1417", {"start": v(-17.89, 41.73) * mm, "end": v(-18.05, 42.15) * mm});
            skLineSegment(sketch, "E1418", {"start": v(-18.05, 42.15) * mm, "end": v(-18.2, 42.56) * mm});
            skLineSegment(sketch, "E1419", {"start": v(-18.2, 42.56) * mm, "end": v(-18.37, 42.98) * mm});
            skLineSegment(sketch, "E1420", {"start": v(-18.37, 42.98) * mm, "end": v(-18.53, 43.4) * mm});
            skLineSegment(sketch, "E1421", {"start": v(-18.53, 43.4) * mm, "end": v(-18.69, 43.81) * mm});
            skLineSegment(sketch, "E1422", {"start": v(-18.69, 43.81) * mm, "end": v(-18.85, 44.23) * mm});
            skLineSegment(sketch, "E1423", {"start": v(-18.85, 44.23) * mm, "end": v(-19, 44.64) * mm});
            skLineSegment(sketch, "E1424", {"start": v(-19, 44.64) * mm, "end": v(-19.17, 45.06) * mm});
            skLineSegment(sketch, "E1425", {"start": v(-19.17, 45.06) * mm, "end": v(-19.33, 45.48) * mm});
            skLineSegment(sketch, "E1426", {"start": v(-19.33, 45.48) * mm, "end": v(-19.49, 45.9) * mm});
            skLineSegment(sketch, "E1427", {"start": v(-19.49, 45.9) * mm, "end": v(-19.54, 46.03) * mm});
            skLineSegment(sketch, "E1428", {"start": v(-19.54, 46.03) * mm, "end": v(-19.94, 45.85) * mm});
            skLineSegment(sketch, "E1429", {"start": v(-19.94, 45.85) * mm, "end": v(-20.35, 45.67) * mm});
            skLineSegment(sketch, "E1430", {"start": v(-20.35, 45.67) * mm, "end": v(-20.73, 45.5) * mm});
            skLineSegment(sketch, "E1431", {"start": v(-20.73, 45.5) * mm, "end": v(-20.66, 45.06) * mm});
            skLineSegment(sketch, "E1432", {"start": v(-20.66, 45.06) * mm, "end": v(-20.59, 44.62) * mm});
            skLineSegment(sketch, "E1433", {"start": v(-20.59, 44.62) * mm, "end": v(-20.51, 44.18) * mm});
            skLineSegment(sketch, "E1434", {"start": v(-20.51, 44.18) * mm, "end": v(-20.44, 43.74) * mm});
            skLineSegment(sketch, "E1435", {"start": v(-20.44, 43.74) * mm, "end": v(-20.36, 43.3) * mm});
            skLineSegment(sketch, "E1436", {"start": v(-20.36, 43.3) * mm, "end": v(-20.29, 42.86) * mm});
            skLineSegment(sketch, "E1437", {"start": v(-20.29, 42.86) * mm, "end": v(-20.21, 42.42) * mm});
            skLineSegment(sketch, "E1438", {"start": v(-20.21, 42.42) * mm, "end": v(-20.14, 41.98) * mm});
            skLineSegment(sketch, "E1439", {"start": v(-20.14, 41.98) * mm, "end": v(-20.07, 41.54) * mm});
            skLineSegment(sketch, "E1440", {"start": v(-20.07, 41.54) * mm, "end": v(-20, 41.1) * mm});
            skLineSegment(sketch, "E1441", {"start": v(-20, 41.1) * mm, "end": v(-19.92, 40.66) * mm});
            skLineSegment(sketch, "E1442", {"start": v(-19.92, 40.66) * mm, "end": v(-19.84, 40.23) * mm});
            skLineSegment(sketch, "E1443", {"start": v(-19.84, 40.23) * mm, "end": v(-19.77, 39.79) * mm});
            skLineSegment(sketch, "E1444", {"start": v(-19.77, 39.79) * mm, "end": v(-19.7, 39.35) * mm});
            skLineSegment(sketch, "E1445", {"start": v(-19.7, 39.35) * mm, "end": v(-19.62, 38.9) * mm});
            skLineSegment(sketch, "E1446", {"start": v(-19.62, 38.9) * mm, "end": v(-19.55, 38.47) * mm});
            skLineSegment(sketch, "E1447", {"start": v(-19.55, 38.47) * mm, "end": v(-19.47, 38.04) * mm});
            skLineSegment(sketch, "E1448", {"start": v(-19.47, 38.04) * mm, "end": v(-19.85, 37.8) * mm});
            skLineSegment(sketch, "E1449", {"start": v(-19.85, 37.8) * mm, "end": v(-20.23, 37.58) * mm});
            skLineSegment(sketch, "E1450", {"start": v(-20.23, 37.58) * mm, "end": v(-20.62, 37.35) * mm});
            skLineSegment(sketch, "E1451", {"start": v(-20.62, 37.35) * mm, "end": v(-21, 37.11) * mm});
            skLineSegment(sketch, "E1452", {"start": v(-21, 37.11) * mm, "end": v(-21.38, 36.88) * mm});
            skLineSegment(sketch, "E1453", {"start": v(-21.38, 36.88) * mm, "end": v(-21.76, 36.65) * mm});
            skLineSegment(sketch, "E1454", {"start": v(-21.76, 36.65) * mm, "end": v(-22.14, 36.42) * mm});
            skLineSegment(sketch, "E1455", {"start": v(-22.14, 36.42) * mm, "end": v(-22.52, 36.2) * mm});
            skLineSegment(sketch, "E1456", {"start": v(-22.52, 36.2) * mm, "end": v(-22.9, 35.96) * mm});
            skLineSegment(sketch, "E1457", {"start": v(-22.9, 35.96) * mm, "end": v(-23.28, 35.73) * mm});
            skLineSegment(sketch, "E1458", {"start": v(-23.28, 35.73) * mm, "end": v(-23.66, 35.5) * mm});
            skLineSegment(sketch, "E1459", {"start": v(-23.66, 35.5) * mm, "end": v(-24.05, 35.27) * mm});
            skLineSegment(sketch, "E1460", {"start": v(-24.05, 35.27) * mm, "end": v(-24.43, 35.03) * mm});
            skLineSegment(sketch, "E1461", {"start": v(-24.43, 35.03) * mm, "end": v(-24.72, 34.86) * mm});
            skLineSegment(sketch, "E1462", {"start": v(-24.72, 34.86) * mm, "end": v(-24.96, 35.23) * mm});
            skLineSegment(sketch, "E1463", {"start": v(-24.96, 35.23) * mm, "end": v(-25.2, 35.6) * mm});
            skLineSegment(sketch, "E1464", {"start": v(-25.2, 35.6) * mm, "end": v(-25.45, 35.98) * mm});
            skLineSegment(sketch, "E1465", {"start": v(-25.45, 35.98) * mm, "end": v(-25.69, 36.35) * mm});
            skLineSegment(sketch, "E1466", {"start": v(-25.69, 36.35) * mm, "end": v(-25.93, 36.73) * mm});
            skLineSegment(sketch, "E1467", {"start": v(-25.93, 36.73) * mm, "end": v(-26.17, 37.1) * mm});
            skLineSegment(sketch, "E1468", {"start": v(-26.17, 37.1) * mm, "end": v(-26.42, 37.47) * mm});
            skLineSegment(sketch, "E1469", {"start": v(-26.42, 37.47) * mm, "end": v(-26.66, 37.85) * mm});
            skLineSegment(sketch, "E1470", {"start": v(-26.66, 37.85) * mm, "end": v(-26.9, 38.22) * mm});
            skLineSegment(sketch, "E1471", {"start": v(-26.9, 38.22) * mm, "end": v(-27.14, 38.6) * mm});
            skLineSegment(sketch, "E1472", {"start": v(-27.14, 38.6) * mm, "end": v(-27.39, 38.97) * mm});
            skLineSegment(sketch, "E1473", {"start": v(-27.39, 38.97) * mm, "end": v(-27.63, 39.34) * mm});
            skLineSegment(sketch, "E1474", {"start": v(-27.63, 39.34) * mm, "end": v(-27.87, 39.72) * mm});
            skLineSegment(sketch, "E1475", {"start": v(-27.87, 39.72) * mm, "end": v(-28.12, 40.1) * mm});
            skLineSegment(sketch, "E1476", {"start": v(-28.12, 40.1) * mm, "end": v(-28.36, 40.46) * mm});
            skLineSegment(sketch, "E1477", {"start": v(-28.36, 40.46) * mm, "end": v(-28.6, 40.84) * mm});
            skLineSegment(sketch, "E1478", {"start": v(-28.6, 40.84) * mm, "end": v(-28.68, 40.96) * mm});
            skLineSegment(sketch, "E1479", {"start": v(-28.68, 40.96) * mm, "end": v(-29.04, 40.7) * mm});
            skLineSegment(sketch, "E1480", {"start": v(-29.04, 40.7) * mm, "end": v(-29.4, 40.44) * mm});
            skLineSegment(sketch, "E1481", {"start": v(-29.4, 40.44) * mm, "end": v(-29.74, 40.2) * mm});
            skLineSegment(sketch, "E1482", {"start": v(-29.74, 40.2) * mm, "end": v(-29.58, 39.78) * mm});
            skLineSegment(sketch, "E1483", {"start": v(-29.58, 39.78) * mm, "end": v(-29.41, 39.36) * mm});
            skLineSegment(sketch, "E1484", {"start": v(-29.41, 39.36) * mm, "end": v(-29.25, 38.95) * mm});
            skLineSegment(sketch, "E1485", {"start": v(-29.25, 38.95) * mm, "end": v(-29.08, 38.54) * mm});
            skLineSegment(sketch, "E1486", {"start": v(-29.08, 38.54) * mm, "end": v(-28.92, 38.12) * mm});
            skLineSegment(sketch, "E1487", {"start": v(-28.92, 38.12) * mm, "end": v(-28.76, 37.7) * mm});
            skLineSegment(sketch, "E1488", {"start": v(-28.76, 37.7) * mm, "end": v(-28.6, 37.3) * mm});
            skLineSegment(sketch, "E1489", {"start": v(-28.6, 37.3) * mm, "end": v(-28.43, 36.88) * mm});
            skLineSegment(sketch, "E1490", {"start": v(-28.43, 36.88) * mm, "end": v(-28.26, 36.46) * mm});
            skLineSegment(sketch, "E1491", {"start": v(-28.26, 36.46) * mm, "end": v(-28.1, 36.05) * mm});
            skLineSegment(sketch, "E1492", {"start": v(-28.1, 36.05) * mm, "end": v(-27.94, 35.64) * mm});
            skLineSegment(sketch, "E1493", {"start": v(-27.94, 35.64) * mm, "end": v(-27.77, 35.22) * mm});
            skLineSegment(sketch, "E1494", {"start": v(-27.77, 35.22) * mm, "end": v(-27.6, 34.8) * mm});
            skLineSegment(sketch, "E1495", {"start": v(-27.6, 34.8) * mm, "end": v(-27.44, 34.4) * mm});
            skLineSegment(sketch, "E1496", {"start": v(-27.44, 34.4) * mm, "end": v(-27.28, 33.98) * mm});
            skLineSegment(sketch, "E1497", {"start": v(-27.28, 33.98) * mm, "end": v(-27.12, 33.56) * mm});
            skLineSegment(sketch, "E1498", {"start": v(-27.12, 33.56) * mm, "end": v(-26.96, 33.16) * mm});
            skLineSegment(sketch, "E1499", {"start": v(-26.96, 33.16) * mm, "end": v(-27.28, 32.85) * mm});
            skLineSegment(sketch, "E1500", {"start": v(-27.28, 32.85) * mm, "end": v(-27.6, 32.55) * mm});
            skLineSegment(sketch, "E1501", {"start": v(-27.6, 32.55) * mm, "end": v(-27.93, 32.24) * mm});
            skLineSegment(sketch, "E1502", {"start": v(-27.93, 32.24) * mm, "end": v(-28.25, 31.94) * mm});
            skLineSegment(sketch, "E1503", {"start": v(-28.25, 31.94) * mm, "end": v(-28.58, 31.63) * mm});
            skLineSegment(sketch, "E1504", {"start": v(-28.58, 31.63) * mm, "end": v(-28.9, 31.33) * mm});
            skLineSegment(sketch, "E1505", {"start": v(-28.9, 31.33) * mm, "end": v(-29.23, 31.02) * mm});
            skLineSegment(sketch, "E1506", {"start": v(-29.23, 31.02) * mm, "end": v(-29.55, 30.72) * mm});
            skLineSegment(sketch, "E1507", {"start": v(-29.55, 30.72) * mm, "end": v(-29.88, 30.41) * mm});
            skLineSegment(sketch, "E1508", {"start": v(-29.88, 30.41) * mm, "end": v(-30.2, 30.1) * mm});
            skLineSegment(sketch, "E1509", {"start": v(-30.2, 30.1) * mm, "end": v(-30.53, 29.8) * mm});
            skLineSegment(sketch, "E1510", {"start": v(-30.53, 29.8) * mm, "end": v(-30.85, 29.5) * mm});
            skLineSegment(sketch, "E1511", {"start": v(-30.85, 29.5) * mm, "end": v(-31.18, 29.2) * mm});
            skLineSegment(sketch, "E1512", {"start": v(-31.18, 29.2) * mm, "end": v(-31.43, 28.96) * mm});
            skLineSegment(sketch, "E1513", {"start": v(-31.43, 28.96) * mm, "end": v(-31.74, 29.27) * mm});
            skLineSegment(sketch, "E1514", {"start": v(-31.74, 29.27) * mm, "end": v(-32.06, 29.59) * mm});
            skLineSegment(sketch, "E1515", {"start": v(-32.06, 29.59) * mm, "end": v(-32.37, 29.9) * mm});
            skLineSegment(sketch, "E1516", {"start": v(-32.37, 29.9) * mm, "end": v(-32.69, 30.22) * mm});
            skLineSegment(sketch, "E1517", {"start": v(-32.69, 30.22) * mm, "end": v(-33, 30.53) * mm});
            skLineSegment(sketch, "E1518", {"start": v(-33, 30.53) * mm, "end": v(-33.32, 30.85) * mm});
            skLineSegment(sketch, "E1519", {"start": v(-33.32, 30.85) * mm, "end": v(-33.63, 31.16) * mm});
            skLineSegment(sketch, "E1520", {"start": v(-33.63, 31.16) * mm, "end": v(-33.95, 31.48) * mm});
            skLineSegment(sketch, "E1521", {"start": v(-33.95, 31.48) * mm, "end": v(-34.26, 31.8) * mm});
            skLineSegment(sketch, "E1522", {"start": v(-34.26, 31.8) * mm, "end": v(-34.58, 32.1) * mm});
            skLineSegment(sketch, "E1523", {"start": v(-34.58, 32.1) * mm, "end": v(-34.9, 32.42) * mm});
            skLineSegment(sketch, "E1524", {"start": v(-34.9, 32.42) * mm, "end": v(-35.2, 32.74) * mm});
            skLineSegment(sketch, "E1525", {"start": v(-35.2, 32.74) * mm, "end": v(-35.52, 33.05) * mm});
            skLineSegment(sketch, "E1526", {"start": v(-35.52, 33.05) * mm, "end": v(-35.84, 33.37) * mm});
            skLineSegment(sketch, "E1527", {"start": v(-35.84, 33.37) * mm, "end": v(-36.15, 33.68) * mm});
            skLineSegment(sketch, "E1528", {"start": v(-36.15, 33.68) * mm, "end": v(-36.47, 34) * mm});
            skLineSegment(sketch, "E1529", {"start": v(-36.47, 34) * mm, "end": v(-36.57, 34.1) * mm});
            skLineSegment(sketch, "E1530", {"start": v(-4.8, 2.64) * mm, "end": v(-4.62, 2.93) * mm});
            skLineSegment(sketch, "E1531", {"start": v(-4.62, 2.93) * mm, "end": v(-4.43, 3.22) * mm});
            skLineSegment(sketch, "E1532", {"start": v(-4.43, 3.22) * mm, "end": v(-4.22, 3.49) * mm});
            skLineSegment(sketch, "E1533", {"start": v(-4.22, 3.49) * mm, "end": v(-3.99, 3.75) * mm});
            skLineSegment(sketch, "E1534", {"start": v(-3.99, 3.75) * mm, "end": v(-3.75, 3.99) * mm});
            skLineSegment(sketch, "E1535", {"start": v(-3.75, 3.99) * mm, "end": v(-3.49, 4.22) * mm});
            skLineSegment(sketch, "E1536", {"start": v(-3.49, 4.22) * mm, "end": v(-3.22, 4.43) * mm});
            skLineSegment(sketch, "E1537", {"start": v(-3.22, 4.43) * mm, "end": v(-2.93, 4.62) * mm});
            skLineSegment(sketch, "E1538", {"start": v(-2.93, 4.62) * mm, "end": v(-2.64, 4.8) * mm});
            skLineSegment(sketch, "E1539", {"start": v(-2.64, 4.8) * mm, "end": v(-2.35, 4.94) * mm});
            skLineSegment(sketch, "E1540", {"start": v(-2.35, 4.94) * mm, "end": v(-2.43, 5.11) * mm});
            skLineSegment(sketch, "E1541", {"start": v(-2.43, 5.11) * mm, "end": v(-2.7, 5.64) * mm});
            skLineSegment(sketch, "E1542", {"start": v(-2.7, 5.64) * mm, "end": v(-2.95, 6.17) * mm});
            skLineSegment(sketch, "E1543", {"start": v(-2.95, 6.17) * mm, "end": v(-3.2, 6.7) * mm});
            skLineSegment(sketch, "E1544", {"start": v(-3.2, 6.7) * mm, "end": v(-3.43, 7.23) * mm});
            skLineSegment(sketch, "E1545", {"start": v(-3.43, 7.23) * mm, "end": v(-3.66, 7.76) * mm});
            skLineSegment(sketch, "E1546", {"start": v(-3.66, 7.76) * mm, "end": v(-3.88, 8.29) * mm});
            skLineSegment(sketch, "E1547", {"start": v(-3.88, 8.29) * mm, "end": v(-4.1, 8.82) * mm});
            skLineSegment(sketch, "E1548", {"start": v(-4.1, 8.82) * mm, "end": v(-4.3, 9.35) * mm});
            skLineSegment(sketch, "E1549", {"start": v(-4.3, 9.35) * mm, "end": v(-4.5, 9.89) * mm});
            skLineSegment(sketch, "E1550", {"start": v(-4.5, 9.89) * mm, "end": v(-4.68, 10.42) * mm});
            skLineSegment(sketch, "E1551", {"start": v(-4.68, 10.42) * mm, "end": v(-4.86, 10.95) * mm});
            skLineSegment(sketch, "E1552", {"start": v(-4.86, 10.95) * mm, "end": v(-5.03, 11.49) * mm});
            skLineSegment(sketch, "E1553", {"start": v(-5.03, 11.49) * mm, "end": v(-5.2, 12.02) * mm});
            skLineSegment(sketch, "E1554", {"start": v(-5.2, 12.02) * mm, "end": v(-5.34, 12.56) * mm});
            skLineSegment(sketch, "E1555", {"start": v(-5.34, 12.56) * mm, "end": v(-5.49, 13.1) * mm});
            skLineSegment(sketch, "E1556", {"start": v(-5.49, 13.1) * mm, "end": v(-5.62, 13.63) * mm});
            skLineSegment(sketch, "E1557", {"start": v(-5.62, 13.63) * mm, "end": v(-5.75, 14.17) * mm});
            skLineSegment(sketch, "E1558", {"start": v(-5.75, 14.17) * mm, "end": v(-5.87, 14.7) * mm});
            skLineSegment(sketch, "E1559", {"start": v(-5.87, 14.7) * mm, "end": v(-5.98, 15.24) * mm});
            skLineSegment(sketch, "E1560", {"start": v(-5.98, 15.24) * mm, "end": v(-6.08, 15.78) * mm});
            skLineSegment(sketch, "E1561", {"start": v(-6.08, 15.78) * mm, "end": v(-6.17, 16.32) * mm});
            skLineSegment(sketch, "E1562", {"start": v(-6.17, 16.32) * mm, "end": v(-6.25, 16.86) * mm});
            skLineSegment(sketch, "E1563", {"start": v(-6.25, 16.86) * mm, "end": v(-6.33, 17.4) * mm});
            skLineSegment(sketch, "E1564", {"start": v(-6.33, 17.4) * mm, "end": v(-6.4, 17.94) * mm});
            skLineSegment(sketch, "E1565", {"start": v(-6.4, 17.94) * mm, "end": v(-6.45, 18.48) * mm});
            skLineSegment(sketch, "E1566", {"start": v(-6.45, 18.48) * mm, "end": v(-6.5, 19.02) * mm});
            skLineSegment(sketch, "E1567", {"start": v(-6.5, 19.02) * mm, "end": v(-6.54, 19.56) * mm});
            skLineSegment(sketch, "E1568", {"start": v(-6.54, 19.56) * mm, "end": v(-6.57, 20.1) * mm});
            skLineSegment(sketch, "E1569", {"start": v(-6.57, 20.1) * mm, "end": v(-6.6, 20.65) * mm});
            skLineSegment(sketch, "E1570", {"start": v(-6.6, 20.65) * mm, "end": v(-6.6, 21.19) * mm});
            skLineSegment(sketch, "E1571", {"start": v(-6.6, 21.19) * mm, "end": v(-6.6, 21.73) * mm});
            skLineSegment(sketch, "E1572", {"start": v(-6.6, 21.73) * mm, "end": v(-6.6, 22.28) * mm});
            skLineSegment(sketch, "E1573", {"start": v(-6.6, 22.28) * mm, "end": v(-6.6, 22.84) * mm});
            skLineSegment(sketch, "E1574", {"start": v(-6.6, 22.84) * mm, "end": v(-6.57, 23.39) * mm});
            skLineSegment(sketch, "E1575", {"start": v(-6.57, 23.39) * mm, "end": v(-6.54, 23.94) * mm});
            skLineSegment(sketch, "E1576", {"start": v(-6.54, 23.94) * mm, "end": v(-6.5, 24.48) * mm});
            skLineSegment(sketch, "E1577", {"start": v(-6.5, 24.48) * mm, "end": v(-6.45, 25.03) * mm});
            skLineSegment(sketch, "E1578", {"start": v(-6.45, 25.03) * mm, "end": v(-6.39, 25.58) * mm});
            skLineSegment(sketch, "E1579", {"start": v(-6.39, 25.58) * mm, "end": v(-6.32, 26.13) * mm});
            skLineSegment(sketch, "E1580", {"start": v(-6.32, 26.13) * mm, "end": v(-6.24, 26.68) * mm});
            skLineSegment(sketch, "E1581", {"start": v(-6.24, 26.68) * mm, "end": v(-6.16, 27.22) * mm});
            skLineSegment(sketch, "E1582", {"start": v(-6.16, 27.22) * mm, "end": v(-6.06, 27.77) * mm});
            skLineSegment(sketch, "E1583", {"start": v(-6.06, 27.77) * mm, "end": v(-5.96, 28.32) * mm});
            skLineSegment(sketch, "E1584", {"start": v(-5.96, 28.32) * mm, "end": v(-5.85, 28.86) * mm});
            skLineSegment(sketch, "E1585", {"start": v(-5.85, 28.86) * mm, "end": v(-5.72, 29.4) * mm});
            skLineSegment(sketch, "E1586", {"start": v(-5.72, 29.4) * mm, "end": v(-5.6, 29.95) * mm});
            skLineSegment(sketch, "E1587", {"start": v(-5.6, 29.95) * mm, "end": v(-5.45, 30.5) * mm});
            skLineSegment(sketch, "E1588", {"start": v(-5.45, 30.5) * mm, "end": v(-5.3, 31.04) * mm});
            skLineSegment(sketch, "E1589", {"start": v(-5.3, 31.04) * mm, "end": v(-5.15, 31.58) * mm});
            skLineSegment(sketch, "E1590", {"start": v(-5.15, 31.58) * mm, "end": v(-4.98, 32.12) * mm});
            skLineSegment(sketch, "E1591", {"start": v(-4.98, 32.12) * mm, "end": v(-4.8, 32.67) * mm});
            skLineSegment(sketch, "E1592", {"start": v(-4.8, 32.67) * mm, "end": v(-4.63, 33.2) * mm});
            skLineSegment(sketch, "E1593", {"start": v(-4.63, 33.2) * mm, "end": v(-4.43, 33.75) * mm});
            skLineSegment(sketch, "E1594", {"start": v(-4.43, 33.75) * mm, "end": v(-4.23, 34.29) * mm});
            skLineSegment(sketch, "E1595", {"start": v(-4.23, 34.29) * mm, "end": v(-4.02, 34.83) * mm});
            skLineSegment(sketch, "E1596", {"start": v(-4.02, 34.83) * mm, "end": v(-3.8, 35.37) * mm});
            skLineSegment(sketch, "E1597", {"start": v(-3.8, 35.37) * mm, "end": v(-3.58, 35.9) * mm});
            skLineSegment(sketch, "E1598", {"start": v(-3.58, 35.9) * mm, "end": v(-3.34, 36.44) * mm});
            skLineSegment(sketch, "E1599", {"start": v(-3.34, 36.44) * mm, "end": v(-3.1, 36.98) * mm});
            skLineSegment(sketch, "E1600", {"start": v(-3.1, 36.98) * mm, "end": v(-2.85, 37.52) * mm});
            skLineSegment(sketch, "E1601", {"start": v(-2.85, 37.52) * mm, "end": v(-2.58, 38.05) * mm});
            skLineSegment(sketch, "E1602", {"start": v(-2.58, 38.05) * mm, "end": v(-2.42, 38.38) * mm});
            skLineSegment(sketch, "E1603", {"start": v(-2.42, 38.38) * mm, "end": v(-4.82, 38.15) * mm});
            skLineSegment(sketch, "E1604", {"start": v(-4.82, 38.15) * mm, "end": v(-7.2, 37.78) * mm});
            skLineSegment(sketch, "E1605", {"start": v(-7.2, 37.78) * mm, "end": v(-9.56, 37.25) * mm});
            skLineSegment(sketch, "E1606", {"start": v(-9.56, 37.25) * mm, "end": v(-11.88, 36.58) * mm});
            skLineSegment(sketch, "E1607", {"start": v(-11.88, 36.58) * mm, "end": v(-14.16, 35.76) * mm});
            skLineSegment(sketch, "E1608", {"start": v(-14.16, 35.76) * mm, "end": v(-16.37, 34.8) * mm});
            skLineSegment(sketch, "E1609", {"start": v(-16.37, 34.8) * mm, "end": v(-18.53, 33.7) * mm});
            skLineSegment(sketch, "E1610", {"start": v(-18.53, 33.7) * mm, "end": v(-20.6, 32.47) * mm});
            skLineSegment(sketch, "E1611", {"start": v(-20.6, 32.47) * mm, "end": v(-22.6, 31.11) * mm});
            skLineSegment(sketch, "E1612", {"start": v(-22.6, 31.11) * mm, "end": v(-24.51, 29.63) * mm});
            skLineSegment(sketch, "E1613", {"start": v(-24.51, 29.63) * mm, "end": v(-26.33, 28.03) * mm});
            skLineSegment(sketch, "E1614", {"start": v(-26.33, 28.03) * mm, "end": v(-28.03, 26.33) * mm});
            skLineSegment(sketch, "E1615", {"start": v(-28.03, 26.33) * mm, "end": v(-29.63, 24.51) * mm});
            skLineSegment(sketch, "E1616", {"start": v(-29.63, 24.51) * mm, "end": v(-31.11, 22.6) * mm});
            skLineSegment(sketch, "E1617", {"start": v(-31.11, 22.6) * mm, "end": v(-32.47, 20.6) * mm});
            skLineSegment(sketch, "E1618", {"start": v(-32.47, 20.6) * mm, "end": v(-33.7, 18.53) * mm});
            skLineSegment(sketch, "E1619", {"start": v(-33.7, 18.53) * mm, "end": v(-34.8, 16.37) * mm});
            skLineSegment(sketch, "E1620", {"start": v(-34.8, 16.37) * mm, "end": v(-35.76, 14.16) * mm});
            skLineSegment(sketch, "E1621", {"start": v(-35.76, 14.16) * mm, "end": v(-36.58, 11.88) * mm});
            skLineSegment(sketch, "E1622", {"start": v(-36.58, 11.88) * mm, "end": v(-37.25, 9.56) * mm});
            skLineSegment(sketch, "E1623", {"start": v(-37.25, 9.56) * mm, "end": v(-37.78, 7.2) * mm});
            skLineSegment(sketch, "E1624", {"start": v(-37.78, 7.2) * mm, "end": v(-38.15, 4.82) * mm});
            skLineSegment(sketch, "E1625", {"start": v(-38.15, 4.82) * mm, "end": v(-38.35, 2.74) * mm});
            skLineSegment(sketch, "E1626", {"start": v(-38.35, 2.74) * mm, "end": v(-38.05, 2.87) * mm});
            skLineSegment(sketch, "E1627", {"start": v(-38.05, 2.87) * mm, "end": v(-37.52, 3.1) * mm});
            skLineSegment(sketch, "E1628", {"start": v(-37.52, 3.1) * mm, "end": v(-36.98, 3.31) * mm});
            skLineSegment(sketch, "E1629", {"start": v(-36.98, 3.31) * mm, "end": v(-36.44, 3.52) * mm});
            skLineSegment(sketch, "E1630", {"start": v(-36.44, 3.52) * mm, "end": v(-35.9, 3.72) * mm});
            skLineSegment(sketch, "E1631", {"start": v(-35.9, 3.72) * mm, "end": v(-35.37, 3.92) * mm});
            skLineSegment(sketch, "E1632", {"start": v(-35.37, 3.92) * mm, "end": v(-34.83, 4.1) * mm});
            skLineSegment(sketch, "E1633", {"start": v(-34.83, 4.1) * mm, "end": v(-34.29, 4.29) * mm});
            skLineSegment(sketch, "E1634", {"start": v(-34.29, 4.29) * mm, "end": v(-33.75, 4.46) * mm});
            skLineSegment(sketch, "E1635", {"start": v(-33.75, 4.46) * mm, "end": v(-33.2, 4.62) * mm});
            skLineSegment(sketch, "E1636", {"start": v(-33.2, 4.62) * mm, "end": v(-32.67, 4.78) * mm});
            skLineSegment(sketch, "E1637", {"start": v(-32.67, 4.78) * mm, "end": v(-32.12, 4.93) * mm});
            skLineSegment(sketch, "E1638", {"start": v(-32.12, 4.93) * mm, "end": v(-31.58, 5.07) * mm});
            skLineSegment(sketch, "E1639", {"start": v(-31.58, 5.07) * mm, "end": v(-31.04, 5.2) * mm});
            skLineSegment(sketch, "E1640", {"start": v(-31.04, 5.2) * mm, "end": v(-30.5, 5.34) * mm});
            skLineSegment(sketch, "E1641", {"start": v(-30.5, 5.34) * mm, "end": v(-29.95, 5.46) * mm});
            skLineSegment(sketch, "E1642", {"start": v(-29.95, 5.46) * mm, "end": v(-29.4, 5.57) * mm});
            skLineSegment(sketch, "E1643", {"start": v(-29.4, 5.57) * mm, "end": v(-28.86, 5.67) * mm});
            skLineSegment(sketch, "E1644", {"start": v(-28.86, 5.67) * mm, "end": v(-28.32, 5.77) * mm});
            skLineSegment(sketch, "E1645", {"start": v(-28.32, 5.77) * mm, "end": v(-27.77, 5.86) * mm});
            skLineSegment(sketch, "E1646", {"start": v(-27.77, 5.86) * mm, "end": v(-27.22, 5.94) * mm});
            skLineSegment(sketch, "E1647", {"start": v(-27.22, 5.94) * mm, "end": v(-26.68, 6.01) * mm});
            skLineSegment(sketch, "E1648", {"start": v(-26.68, 6.01) * mm, "end": v(-26.13, 6.08) * mm});
            skLineSegment(sketch, "E1649", {"start": v(-26.13, 6.08) * mm, "end": v(-25.58, 6.14) * mm});
            skLineSegment(sketch, "E1650", {"start": v(-25.58, 6.14) * mm, "end": v(-25.03, 6.19) * mm});
            skLineSegment(sketch, "E1651", {"start": v(-25.03, 6.19) * mm, "end": v(-24.48, 6.23) * mm});
            skLineSegment(sketch, "E1652", {"start": v(-24.48, 6.23) * mm, "end": v(-23.94, 6.27) * mm});
            skLineSegment(sketch, "E1653", {"start": v(-23.94, 6.27) * mm, "end": v(-23.39, 6.3) * mm});
            skLineSegment(sketch, "E1654", {"start": v(-23.39, 6.3) * mm, "end": v(-22.84, 6.31) * mm});
            skLineSegment(sketch, "E1655", {"start": v(-22.84, 6.31) * mm, "end": v(-22.28, 6.32) * mm});
            skLineSegment(sketch, "E1656", {"start": v(-22.28, 6.32) * mm, "end": v(-21.73, 6.33) * mm});
            skLineSegment(sketch, "E1657", {"start": v(-21.73, 6.33) * mm, "end": v(-21.19, 6.32) * mm});
            skLineSegment(sketch, "E1658", {"start": v(-21.19, 6.32) * mm, "end": v(-20.65, 6.31) * mm});
            skLineSegment(sketch, "E1659", {"start": v(-20.65, 6.31) * mm, "end": v(-20.1, 6.3) * mm});
            skLineSegment(sketch, "E1660", {"start": v(-20.1, 6.3) * mm, "end": v(-19.56, 6.27) * mm});
            skLineSegment(sketch, "E1661", {"start": v(-19.56, 6.27) * mm, "end": v(-19.02, 6.23) * mm});
            skLineSegment(sketch, "E1662", {"start": v(-19.02, 6.23) * mm, "end": v(-18.48, 6.2) * mm});
            skLineSegment(sketch, "E1663", {"start": v(-18.48, 6.2) * mm, "end": v(-17.94, 6.14) * mm});
            skLineSegment(sketch, "E1664", {"start": v(-17.94, 6.14) * mm, "end": v(-17.4, 6.09) * mm});
            skLineSegment(sketch, "E1665", {"start": v(-17.4, 6.09) * mm, "end": v(-16.86, 6.02) * mm});
            skLineSegment(sketch, "E1666", {"start": v(-16.86, 6.02) * mm, "end": v(-16.32, 5.95) * mm});
            skLineSegment(sketch, "E1667", {"start": v(-16.32, 5.95) * mm, "end": v(-15.78, 5.87) * mm});
            skLineSegment(sketch, "E1668", {"start": v(-15.78, 5.87) * mm, "end": v(-15.24, 5.78) * mm});
            skLineSegment(sketch, "E1669", {"start": v(-15.24, 5.78) * mm, "end": v(-14.7, 5.7) * mm});
            skLineSegment(sketch, "E1670", {"start": v(-14.7, 5.7) * mm, "end": v(-14.17, 5.59) * mm});
            skLineSegment(sketch, "E1671", {"start": v(-14.17, 5.59) * mm, "end": v(-13.63, 5.48) * mm});
            skLineSegment(sketch, "E1672", {"start": v(-13.63, 5.48) * mm, "end": v(-13.1, 5.36) * mm});
            skLineSegment(sketch, "E1673", {"start": v(-13.1, 5.36) * mm, "end": v(-12.56, 5.24) * mm});
            skLineSegment(sketch, "E1674", {"start": v(-12.56, 5.24) * mm, "end": v(-12.02, 5.1) * mm});
            skLineSegment(sketch, "E1675", {"start": v(-12.02, 5.1) * mm, "end": v(-11.49, 4.97) * mm});
            skLineSegment(sketch, "E1676", {"start": v(-11.49, 4.97) * mm, "end": v(-10.95, 4.83) * mm});
            skLineSegment(sketch, "E1677", {"start": v(-10.95, 4.83) * mm, "end": v(-10.42, 4.67) * mm});
            skLineSegment(sketch, "E1678", {"start": v(-10.42, 4.67) * mm, "end": v(-9.89, 4.51) * mm});
            skLineSegment(sketch, "E1679", {"start": v(-9.89, 4.51) * mm, "end": v(-9.35, 4.34) * mm});
            skLineSegment(sketch, "E1680", {"start": v(-9.35, 4.34) * mm, "end": v(-8.82, 4.17) * mm});
            skLineSegment(sketch, "E1681", {"start": v(-8.82, 4.17) * mm, "end": v(-8.29, 3.99) * mm});
            skLineSegment(sketch, "E1682", {"start": v(-8.29, 3.99) * mm, "end": v(-7.76, 3.8) * mm});
            skLineSegment(sketch, "E1683", {"start": v(-7.76, 3.8) * mm, "end": v(-7.23, 3.6) * mm});
            skLineSegment(sketch, "E1684", {"start": v(-7.23, 3.6) * mm, "end": v(-6.7, 3.4) * mm});
            skLineSegment(sketch, "E1685", {"start": v(-6.7, 3.4) * mm, "end": v(-6.17, 3.18) * mm});
            skLineSegment(sketch, "E1686", {"start": v(-6.17, 3.18) * mm, "end": v(-5.64, 2.97) * mm});
            skLineSegment(sketch, "E1687", {"start": v(-5.64, 2.97) * mm, "end": v(-5.11, 2.74) * mm});
            skLineSegment(sketch, "E1688", {"start": v(-5.11, 2.74) * mm, "end": v(-4.81, 2.6) * mm});
            skLineSegment(sketch, "E1689", {"start": v(-4.81, 2.6) * mm, "end": v(-4.8, 2.64) * mm});
            skLineSegment(sketch, "E1690", {"start": v(5.11, 2.43) * mm, "end": v(5.64, 2.7) * mm});
            skLineSegment(sketch, "E1691", {"start": v(5.64, 2.7) * mm, "end": v(6.17, 2.95) * mm});
            skLineSegment(sketch, "E1692", {"start": v(6.17, 2.95) * mm, "end": v(6.7, 3.2) * mm});
            skLineSegment(sketch, "E1693", {"start": v(6.7, 3.2) * mm, "end": v(7.23, 3.43) * mm});
            skLineSegment(sketch, "E1694", {"start": v(7.23, 3.43) * mm, "end": v(7.76, 3.66) * mm});
            skLineSegment(sketch, "E1695", {"start": v(7.76, 3.66) * mm, "end": v(8.29, 3.88) * mm});
            skLineSegment(sketch, "E1696", {"start": v(8.29, 3.88) * mm, "end": v(8.82, 4.1) * mm});
            skLineSegment(sketch, "E1697", {"start": v(8.82, 4.1) * mm, "end": v(9.35, 4.3) * mm});
            skLineSegment(sketch, "E1698", {"start": v(9.35, 4.3) * mm, "end": v(9.89, 4.5) * mm});
            skLineSegment(sketch, "E1699", {"start": v(9.89, 4.5) * mm, "end": v(10.42, 4.68) * mm});
            skLineSegment(sketch, "E1700", {"start": v(10.42, 4.68) * mm, "end": v(10.95, 4.86) * mm});
            skLineSegment(sketch, "E1701", {"start": v(10.95, 4.86) * mm, "end": v(11.49, 5.03) * mm});
            skLineSegment(sketch, "E1702", {"start": v(11.49, 5.03) * mm, "end": v(12.02, 5.2) * mm});
            skLineSegment(sketch, "E1703", {"start": v(12.02, 5.2) * mm, "end": v(12.56, 5.34) * mm});
            skLineSegment(sketch, "E1704", {"start": v(12.56, 5.34) * mm, "end": v(13.1, 5.49) * mm});
            skLineSegment(sketch, "E1705", {"start": v(13.1, 5.49) * mm, "end": v(13.63, 5.62) * mm});
            skLineSegment(sketch, "E1706", {"start": v(13.63, 5.62) * mm, "end": v(14.17, 5.75) * mm});
            skLineSegment(sketch, "E1707", {"start": v(14.17, 5.75) * mm, "end": v(14.7, 5.87) * mm});
            skLineSegment(sketch, "E1708", {"start": v(14.7, 5.87) * mm, "end": v(15.24, 5.98) * mm});
            skLineSegment(sketch, "E1709", {"start": v(15.24, 5.98) * mm, "end": v(15.78, 6.08) * mm});
            skLineSegment(sketch, "E1710", {"start": v(15.78, 6.08) * mm, "end": v(16.32, 6.17) * mm});
            skLineSegment(sketch, "E1711", {"start": v(16.32, 6.17) * mm, "end": v(16.86, 6.25) * mm});
            skLineSegment(sketch, "E1712", {"start": v(16.86, 6.25) * mm, "end": v(17.4, 6.33) * mm});
            skLineSegment(sketch, "E1713", {"start": v(17.4, 6.33) * mm, "end": v(17.94, 6.4) * mm});
            skLineSegment(sketch, "E1714", {"start": v(17.94, 6.4) * mm, "end": v(18.48, 6.45) * mm});
            skLineSegment(sketch, "E1715", {"start": v(18.48, 6.45) * mm, "end": v(19.02, 6.5) * mm});
            skLineSegment(sketch, "E1716", {"start": v(19.02, 6.5) * mm, "end": v(19.56, 6.54) * mm});
            skLineSegment(sketch, "E1717", {"start": v(19.56, 6.54) * mm, "end": v(20.1, 6.57) * mm});
            skLineSegment(sketch, "E1718", {"start": v(20.1, 6.57) * mm, "end": v(20.65, 6.6) * mm});
            skLineSegment(sketch, "E1719", {"start": v(20.65, 6.6) * mm, "end": v(21.19, 6.6) * mm});
            skLineSegment(sketch, "E1720", {"start": v(21.19, 6.6) * mm, "end": v(21.73, 6.6) * mm});
            skLineSegment(sketch, "E1721", {"start": v(21.73, 6.6) * mm, "end": v(22.28, 6.6) * mm});
            skLineSegment(sketch, "E1722", {"start": v(22.28, 6.6) * mm, "end": v(22.84, 6.6) * mm});
            skLineSegment(sketch, "E1723", {"start": v(22.84, 6.6) * mm, "end": v(23.39, 6.57) * mm});
            skLineSegment(sketch, "E1724", {"start": v(23.39, 6.57) * mm, "end": v(23.94, 6.54) * mm});
            skLineSegment(sketch, "E1725", {"start": v(23.94, 6.54) * mm, "end": v(24.48, 6.5) * mm});
            skLineSegment(sketch, "E1726", {"start": v(24.48, 6.5) * mm, "end": v(25.03, 6.45) * mm});
            skLineSegment(sketch, "E1727", {"start": v(25.03, 6.45) * mm, "end": v(25.58, 6.39) * mm});
            skLineSegment(sketch, "E1728", {"start": v(25.58, 6.39) * mm, "end": v(26.13, 6.32) * mm});
            skLineSegment(sketch, "E1729", {"start": v(26.13, 6.32) * mm, "end": v(26.68, 6.24) * mm});
            skLineSegment(sketch, "E1730", {"start": v(26.68, 6.24) * mm, "end": v(27.22, 6.16) * mm});
            skLineSegment(sketch, "E1731", {"start": v(27.22, 6.16) * mm, "end": v(27.77, 6.06) * mm});
            skLineSegment(sketch, "E1732", {"start": v(27.77, 6.06) * mm, "end": v(28.32, 5.96) * mm});
            skLineSegment(sketch, "E1733", {"start": v(28.32, 5.96) * mm, "end": v(28.86, 5.85) * mm});
            skLineSegment(sketch, "E1734", {"start": v(28.86, 5.85) * mm, "end": v(29.4, 5.72) * mm});
            skLineSegment(sketch, "E1735", {"start": v(29.4, 5.72) * mm, "end": v(29.95, 5.6) * mm});
            skLineSegment(sketch, "E1736", {"start": v(29.95, 5.6) * mm, "end": v(30.5, 5.45) * mm});
            skLineSegment(sketch, "E1737", {"start": v(30.5, 5.45) * mm, "end": v(31.04, 5.3) * mm});
            skLineSegment(sketch, "E1738", {"start": v(31.04, 5.3) * mm, "end": v(31.58, 5.15) * mm});
            skLineSegment(sketch, "E1739", {"start": v(31.58, 5.15) * mm, "end": v(32.12, 4.98) * mm});
            skLineSegment(sketch, "E1740", {"start": v(32.12, 4.98) * mm, "end": v(32.67, 4.8) * mm});
            skLineSegment(sketch, "E1741", {"start": v(32.67, 4.8) * mm, "end": v(33.2, 4.63) * mm});
            skLineSegment(sketch, "E1742", {"start": v(33.2, 4.63) * mm, "end": v(33.75, 4.43) * mm});
            skLineSegment(sketch, "E1743", {"start": v(33.75, 4.43) * mm, "end": v(34.29, 4.23) * mm});
            skLineSegment(sketch, "E1744", {"start": v(34.29, 4.23) * mm, "end": v(34.83, 4.02) * mm});
            skLineSegment(sketch, "E1745", {"start": v(34.83, 4.02) * mm, "end": v(35.37, 3.8) * mm});
            skLineSegment(sketch, "E1746", {"start": v(35.37, 3.8) * mm, "end": v(35.9, 3.58) * mm});
            skLineSegment(sketch, "E1747", {"start": v(35.9, 3.58) * mm, "end": v(36.44, 3.34) * mm});
            skLineSegment(sketch, "E1748", {"start": v(36.44, 3.34) * mm, "end": v(36.98, 3.1) * mm});
            skLineSegment(sketch, "E1749", {"start": v(36.98, 3.1) * mm, "end": v(37.52, 2.85) * mm});
            skLineSegment(sketch, "E1750", {"start": v(37.52, 2.85) * mm, "end": v(38.05, 2.58) * mm});
            skLineSegment(sketch, "E1751", {"start": v(38.05, 2.58) * mm, "end": v(38.38, 2.42) * mm});
            skLineSegment(sketch, "E1752", {"start": v(38.38, 2.42) * mm, "end": v(38.15, 4.82) * mm});
            skLineSegment(sketch, "E1753", {"start": v(38.15, 4.82) * mm, "end": v(37.78, 7.2) * mm});
            skLineSegment(sketch, "E1754", {"start": v(37.78, 7.2) * mm, "end": v(37.25, 9.56) * mm});
            skLineSegment(sketch, "E1755", {"start": v(37.25, 9.56) * mm, "end": v(36.58, 11.88) * mm});
            skLineSegment(sketch, "E1756", {"start": v(36.58, 11.88) * mm, "end": v(35.76, 14.16) * mm});
            skLineSegment(sketch, "E1757", {"start": v(35.76, 14.16) * mm, "end": v(34.8, 16.37) * mm});
            skLineSegment(sketch, "E1758", {"start": v(34.8, 16.37) * mm, "end": v(33.7, 18.53) * mm});
            skLineSegment(sketch, "E1759", {"start": v(33.7, 18.53) * mm, "end": v(32.47, 20.6) * mm});
            skLineSegment(sketch, "E1760", {"start": v(32.47, 20.6) * mm, "end": v(31.11, 22.6) * mm});
            skLineSegment(sketch, "E1761", {"start": v(31.11, 22.6) * mm, "end": v(29.63, 24.51) * mm});
            skLineSegment(sketch, "E1762", {"start": v(29.63, 24.51) * mm, "end": v(28.03, 26.33) * mm});
            skLineSegment(sketch, "E1763", {"start": v(28.03, 26.33) * mm, "end": v(26.33, 28.03) * mm});
            skLineSegment(sketch, "E1764", {"start": v(26.33, 28.03) * mm, "end": v(24.51, 29.63) * mm});
            skLineSegment(sketch, "E1765", {"start": v(24.51, 29.63) * mm, "end": v(22.6, 31.11) * mm});
            skLineSegment(sketch, "E1766", {"start": v(22.6, 31.11) * mm, "end": v(20.6, 32.47) * mm});
            skLineSegment(sketch, "E1767", {"start": v(20.6, 32.47) * mm, "end": v(18.53, 33.7) * mm});
            skLineSegment(sketch, "E1768", {"start": v(18.53, 33.7) * mm, "end": v(16.37, 34.8) * mm});
            skLineSegment(sketch, "E1769", {"start": v(16.37, 34.8) * mm, "end": v(14.16, 35.76) * mm});
            skLineSegment(sketch, "E1770", {"start": v(14.16, 35.76) * mm, "end": v(11.88, 36.58) * mm});
            skLineSegment(sketch, "E1771", {"start": v(11.88, 36.58) * mm, "end": v(9.56, 37.25) * mm});
            skLineSegment(sketch, "E1772", {"start": v(9.56, 37.25) * mm, "end": v(7.2, 37.78) * mm});
            skLineSegment(sketch, "E1773", {"start": v(7.2, 37.78) * mm, "end": v(4.82, 38.15) * mm});
            skLineSegment(sketch, "E1774", {"start": v(4.82, 38.15) * mm, "end": v(2.74, 38.35) * mm});
            skLineSegment(sketch, "E1775", {"start": v(2.74, 38.35) * mm, "end": v(2.87, 38.05) * mm});
            skLineSegment(sketch, "E1776", {"start": v(2.87, 38.05) * mm, "end": v(3.1, 37.52) * mm});
            skLineSegment(sketch, "E1777", {"start": v(3.1, 37.52) * mm, "end": v(3.31, 36.98) * mm});
            skLineSegment(sketch, "E1778", {"start": v(3.31, 36.98) * mm, "end": v(3.52, 36.44) * mm});
            skLineSegment(sketch, "E1779", {"start": v(3.52, 36.44) * mm, "end": v(3.72, 35.9) * mm});
            skLineSegment(sketch, "E1780", {"start": v(3.72, 35.9) * mm, "end": v(3.92, 35.37) * mm});
            skLineSegment(sketch, "E1781", {"start": v(3.92, 35.37) * mm, "end": v(4.1, 34.83) * mm});
            skLineSegment(sketch, "E1782", {"start": v(4.1, 34.83) * mm, "end": v(4.29, 34.29) * mm});
            skLineSegment(sketch, "E1783", {"start": v(4.29, 34.29) * mm, "end": v(4.46, 33.75) * mm});
            skLineSegment(sketch, "E1784", {"start": v(4.46, 33.75) * mm, "end": v(4.62, 33.2) * mm});
            skLineSegment(sketch, "E1785", {"start": v(4.62, 33.2) * mm, "end": v(4.78, 32.67) * mm});
            skLineSegment(sketch, "E1786", {"start": v(4.78, 32.67) * mm, "end": v(4.93, 32.12) * mm});
            skLineSegment(sketch, "E1787", {"start": v(4.93, 32.12) * mm, "end": v(5.07, 31.58) * mm});
            skLineSegment(sketch, "E1788", {"start": v(5.07, 31.58) * mm, "end": v(5.2, 31.04) * mm});
            skLineSegment(sketch, "E1789", {"start": v(5.2, 31.04) * mm, "end": v(5.34, 30.5) * mm});
            skLineSegment(sketch, "E1790", {"start": v(5.34, 30.5) * mm, "end": v(5.46, 29.95) * mm});
            skLineSegment(sketch, "E1791", {"start": v(5.46, 29.95) * mm, "end": v(5.57, 29.4) * mm});
            skLineSegment(sketch, "E1792", {"start": v(5.57, 29.4) * mm, "end": v(5.67, 28.86) * mm});
            skLineSegment(sketch, "E1793", {"start": v(5.67, 28.86) * mm, "end": v(5.77, 28.32) * mm});
            skLineSegment(sketch, "E1794", {"start": v(5.77, 28.32) * mm, "end": v(5.86, 27.77) * mm});
            skLineSegment(sketch, "E1795", {"start": v(5.86, 27.77) * mm, "end": v(5.94, 27.22) * mm});
            skLineSegment(sketch, "E1796", {"start": v(5.94, 27.22) * mm, "end": v(6.01, 26.68) * mm});
            skLineSegment(sketch, "E1797", {"start": v(6.01, 26.68) * mm, "end": v(6.08, 26.13) * mm});
            skLineSegment(sketch, "E1798", {"start": v(6.08, 26.13) * mm, "end": v(6.14, 25.58) * mm});
            skLineSegment(sketch, "E1799", {"start": v(6.14, 25.58) * mm, "end": v(6.19, 25.03) * mm});
            skLineSegment(sketch, "E1800", {"start": v(6.19, 25.03) * mm, "end": v(6.23, 24.48) * mm});
            skLineSegment(sketch, "E1801", {"start": v(6.23, 24.48) * mm, "end": v(6.27, 23.94) * mm});
            skLineSegment(sketch, "E1802", {"start": v(6.27, 23.94) * mm, "end": v(6.3, 23.39) * mm});
            skLineSegment(sketch, "E1803", {"start": v(6.3, 23.39) * mm, "end": v(6.31, 22.84) * mm});
            skLineSegment(sketch, "E1804", {"start": v(6.31, 22.84) * mm, "end": v(6.32, 22.28) * mm});
            skLineSegment(sketch, "E1805", {"start": v(6.32, 22.28) * mm, "end": v(6.33, 21.73) * mm});
            skLineSegment(sketch, "E1806", {"start": v(6.33, 21.73) * mm, "end": v(6.32, 21.19) * mm});
            skLineSegment(sketch, "E1807", {"start": v(6.32, 21.19) * mm, "end": v(6.31, 20.65) * mm});
            skLineSegment(sketch, "E1808", {"start": v(6.31, 20.65) * mm, "end": v(6.3, 20.1) * mm});
            skLineSegment(sketch, "E1809", {"start": v(6.3, 20.1) * mm, "end": v(6.27, 19.56) * mm});
            skLineSegment(sketch, "E1810", {"start": v(6.27, 19.56) * mm, "end": v(6.23, 19.02) * mm});
            skLineSegment(sketch, "E1811", {"start": v(6.23, 19.02) * mm, "end": v(6.2, 18.48) * mm});
            skLineSegment(sketch, "E1812", {"start": v(6.2, 18.48) * mm, "end": v(6.14, 17.94) * mm});
            skLineSegment(sketch, "E1813", {"start": v(6.14, 17.94) * mm, "end": v(6.09, 17.4) * mm});
            skLineSegment(sketch, "E1814", {"start": v(6.09, 17.4) * mm, "end": v(6.02, 16.86) * mm});
            skLineSegment(sketch, "E1815", {"start": v(6.02, 16.86) * mm, "end": v(5.95, 16.32) * mm});
            skLineSegment(sketch, "E1816", {"start": v(5.95, 16.32) * mm, "end": v(5.87, 15.78) * mm});
            skLineSegment(sketch, "E1817", {"start": v(5.87, 15.78) * mm, "end": v(5.78, 15.24) * mm});
            skLineSegment(sketch, "E1818", {"start": v(5.78, 15.24) * mm, "end": v(5.7, 14.7) * mm});
            skLineSegment(sketch, "E1819", {"start": v(5.7, 14.7) * mm, "end": v(5.59, 14.17) * mm});
            skLineSegment(sketch, "E1820", {"start": v(5.59, 14.17) * mm, "end": v(5.48, 13.63) * mm});
            skLineSegment(sketch, "E1821", {"start": v(5.48, 13.63) * mm, "end": v(5.36, 13.1) * mm});
            skLineSegment(sketch, "E1822", {"start": v(5.36, 13.1) * mm, "end": v(5.24, 12.56) * mm});
            skLineSegment(sketch, "E1823", {"start": v(5.24, 12.56) * mm, "end": v(5.1, 12.02) * mm});
            skLineSegment(sketch, "E1824", {"start": v(5.1, 12.02) * mm, "end": v(4.97, 11.49) * mm});
            skLineSegment(sketch, "E1825", {"start": v(4.97, 11.49) * mm, "end": v(4.83, 10.95) * mm});
            skLineSegment(sketch, "E1826", {"start": v(4.83, 10.95) * mm, "end": v(4.67, 10.42) * mm});
            skLineSegment(sketch, "E1827", {"start": v(4.67, 10.42) * mm, "end": v(4.51, 9.89) * mm});
            skLineSegment(sketch, "E1828", {"start": v(4.51, 9.89) * mm, "end": v(4.34, 9.35) * mm});
            skLineSegment(sketch, "E1829", {"start": v(4.34, 9.35) * mm, "end": v(4.17, 8.82) * mm});
            skLineSegment(sketch, "E1830", {"start": v(4.17, 8.82) * mm, "end": v(3.99, 8.29) * mm});
            skLineSegment(sketch, "E1831", {"start": v(3.99, 8.29) * mm, "end": v(3.8, 7.76) * mm});
            skLineSegment(sketch, "E1832", {"start": v(3.8, 7.76) * mm, "end": v(3.6, 7.23) * mm});
            skLineSegment(sketch, "E1833", {"start": v(3.6, 7.23) * mm, "end": v(3.4, 6.7) * mm});
            skLineSegment(sketch, "E1834", {"start": v(3.4, 6.7) * mm, "end": v(3.18, 6.17) * mm});
            skLineSegment(sketch, "E1835", {"start": v(3.18, 6.17) * mm, "end": v(2.97, 5.64) * mm});
            skLineSegment(sketch, "E1836", {"start": v(2.97, 5.64) * mm, "end": v(2.74, 5.11) * mm});
            skLineSegment(sketch, "E1837", {"start": v(2.74, 5.11) * mm, "end": v(2.6, 4.81) * mm});
            skLineSegment(sketch, "E1838", {"start": v(2.6, 4.81) * mm, "end": v(2.64, 4.8) * mm});
            skLineSegment(sketch, "E1839", {"start": v(2.64, 4.8) * mm, "end": v(2.93, 4.62) * mm});
            skLineSegment(sketch, "E1840", {"start": v(2.93, 4.62) * mm, "end": v(3.22, 4.43) * mm});
            skLineSegment(sketch, "E1841", {"start": v(3.22, 4.43) * mm, "end": v(3.49, 4.22) * mm});
            skLineSegment(sketch, "E1842", {"start": v(3.49, 4.22) * mm, "end": v(3.75, 3.99) * mm});
            skLineSegment(sketch, "E1843", {"start": v(3.75, 3.99) * mm, "end": v(3.99, 3.75) * mm});
            skLineSegment(sketch, "E1844", {"start": v(3.99, 3.75) * mm, "end": v(4.22, 3.49) * mm});
            skLineSegment(sketch, "E1845", {"start": v(4.22, 3.49) * mm, "end": v(4.43, 3.22) * mm});
            skLineSegment(sketch, "E1846", {"start": v(4.43, 3.22) * mm, "end": v(4.62, 2.93) * mm});
            skLineSegment(sketch, "E1847", {"start": v(4.62, 2.93) * mm, "end": v(4.8, 2.64) * mm});
            skLineSegment(sketch, "E1848", {"start": v(4.8, 2.64) * mm, "end": v(4.94, 2.35) * mm});
            skLineSegment(sketch, "E1849", {"start": v(4.94, 2.35) * mm, "end": v(5.11, 2.43) * mm});
            skLineSegment(sketch, "E1850", {"start": v(0.88, 13.27) * mm, "end": v(1, 13.55) * mm});
            skLineSegment(sketch, "E1851", {"start": v(1, 13.55) * mm, "end": v(1.13, 13.84) * mm});
            skLineSegment(sketch, "E1852", {"start": v(1.13, 13.84) * mm, "end": v(1.24, 14.12) * mm});
            skLineSegment(sketch, "E1853", {"start": v(1.24, 14.12) * mm, "end": v(1.36, 14.4) * mm});
            skLineSegment(sketch, "E1854", {"start": v(1.36, 14.4) * mm, "end": v(1.46, 14.69) * mm});
            skLineSegment(sketch, "E1855", {"start": v(1.46, 14.69) * mm, "end": v(1.57, 14.97) * mm});
            skLineSegment(sketch, "E1856", {"start": v(1.57, 14.97) * mm, "end": v(1.67, 15.25) * mm});
            skLineSegment(sketch, "E1857", {"start": v(1.67, 15.25) * mm, "end": v(1.77, 15.54) * mm});
            skLineSegment(sketch, "E1858", {"start": v(1.77, 15.54) * mm, "end": v(1.86, 15.82) * mm});
            skLineSegment(sketch, "E1859", {"start": v(1.86, 15.82) * mm, "end": v(1.95, 16.1) * mm});
            skLineSegment(sketch, "E1860", {"start": v(1.95, 16.1) * mm, "end": v(2.03, 16.4) * mm});
            skLineSegment(sketch, "E1861", {"start": v(2.03, 16.4) * mm, "end": v(2.1, 16.68) * mm});
            skLineSegment(sketch, "E1862", {"start": v(2.1, 16.68) * mm, "end": v(2.18, 16.96) * mm});
            skLineSegment(sketch, "E1863", {"start": v(2.18, 16.96) * mm, "end": v(2.25, 17.24) * mm});
            skLineSegment(sketch, "E1864", {"start": v(2.25, 17.24) * mm, "end": v(2.32, 17.53) * mm});
            skLineSegment(sketch, "E1865", {"start": v(2.32, 17.53) * mm, "end": v(2.38, 17.82) * mm});
            skLineSegment(sketch, "E1866", {"start": v(2.38, 17.82) * mm, "end": v(2.44, 18.1) * mm});
            skLineSegment(sketch, "E1867", {"start": v(2.44, 18.1) * mm, "end": v(2.5, 18.39) * mm});
            skLineSegment(sketch, "E1868", {"start": v(2.5, 18.39) * mm, "end": v(2.54, 18.67) * mm});
            skLineSegment(sketch, "E1869", {"start": v(2.54, 18.67) * mm, "end": v(2.59, 18.96) * mm});
            skLineSegment(sketch, "E1870", {"start": v(2.59, 18.96) * mm, "end": v(2.63, 19.24) * mm});
            skLineSegment(sketch, "E1871", {"start": v(2.63, 19.24) * mm, "end": v(2.67, 19.53) * mm});
            skLineSegment(sketch, "E1872", {"start": v(2.67, 19.53) * mm, "end": v(2.7, 19.82) * mm});
            skLineSegment(sketch, "E1873", {"start": v(2.7, 19.82) * mm, "end": v(2.73, 20.1) * mm});
            skLineSegment(sketch, "E1874", {"start": v(2.73, 20.1) * mm, "end": v(2.75, 20.4) * mm});
            skLineSegment(sketch, "E1875", {"start": v(2.75, 20.4) * mm, "end": v(2.77, 20.68) * mm});
            skLineSegment(sketch, "E1876", {"start": v(2.77, 20.68) * mm, "end": v(2.79, 20.97) * mm});
            skLineSegment(sketch, "E1877", {"start": v(2.79, 20.97) * mm, "end": v(2.8, 21.25) * mm});
            skLineSegment(sketch, "E1878", {"start": v(2.8, 21.25) * mm, "end": v(2.8, 21.54) * mm});
            skLineSegment(sketch, "E1879", {"start": v(2.8, 21.54) * mm, "end": v(2.8, 21.83) * mm});
            skLineSegment(sketch, "E1880", {"start": v(2.8, 21.83) * mm, "end": v(2.8, 22.12) * mm});
            skLineSegment(sketch, "E1881", {"start": v(2.8, 22.12) * mm, "end": v(2.8, 22.42) * mm});
            skLineSegment(sketch, "E1882", {"start": v(2.8, 22.42) * mm, "end": v(2.79, 22.7) * mm});
            skLineSegment(sketch, "E1883", {"start": v(2.79, 22.7) * mm, "end": v(2.77, 23) * mm});
            skLineSegment(sketch, "E1884", {"start": v(2.77, 23) * mm, "end": v(2.75, 23.3) * mm});
            skLineSegment(sketch, "E1885", {"start": v(2.75, 23.3) * mm, "end": v(2.73, 23.58) * mm});
            skLineSegment(sketch, "E1886", {"start": v(2.73, 23.58) * mm, "end": v(2.7, 23.87) * mm});
            skLineSegment(sketch, "E1887", {"start": v(2.7, 23.87) * mm, "end": v(2.66, 24.16) * mm});
            skLineSegment(sketch, "E1888", {"start": v(2.66, 24.16) * mm, "end": v(2.63, 24.45) * mm});
            skLineSegment(sketch, "E1889", {"start": v(2.63, 24.45) * mm, "end": v(2.58, 24.74) * mm});
            skLineSegment(sketch, "E1890", {"start": v(2.58, 24.74) * mm, "end": v(2.54, 25.03) * mm});
            skLineSegment(sketch, "E1891", {"start": v(2.54, 25.03) * mm, "end": v(2.49, 25.32) * mm});
            skLineSegment(sketch, "E1892", {"start": v(2.49, 25.32) * mm, "end": v(2.43, 25.61) * mm});
            skLineSegment(sketch, "E1893", {"start": v(2.43, 25.61) * mm, "end": v(2.37, 25.9) * mm});
            skLineSegment(sketch, "E1894", {"start": v(2.37, 25.9) * mm, "end": v(2.3, 26.2) * mm});
            skLineSegment(sketch, "E1895", {"start": v(2.3, 26.2) * mm, "end": v(2.24, 26.48) * mm});
            skLineSegment(sketch, "E1896", {"start": v(2.24, 26.48) * mm, "end": v(2.17, 26.77) * mm});
            skLineSegment(sketch, "E1897", {"start": v(2.17, 26.77) * mm, "end": v(2.09, 27.06) * mm});
            skLineSegment(sketch, "E1898", {"start": v(2.09, 27.06) * mm, "end": v(2, 27.35) * mm});
            skLineSegment(sketch, "E1899", {"start": v(2, 27.35) * mm, "end": v(1.92, 27.64) * mm});
            skLineSegment(sketch, "E1900", {"start": v(1.92, 27.64) * mm, "end": v(1.83, 27.92) * mm});
            skLineSegment(sketch, "E1901", {"start": v(1.83, 27.92) * mm, "end": v(1.74, 28.21) * mm});
            skLineSegment(sketch, "E1902", {"start": v(1.74, 28.21) * mm, "end": v(1.64, 28.5) * mm});
            skLineSegment(sketch, "E1903", {"start": v(1.64, 28.5) * mm, "end": v(1.53, 28.79) * mm});
            skLineSegment(sketch, "E1904", {"start": v(1.53, 28.79) * mm, "end": v(1.43, 29.08) * mm});
            skLineSegment(sketch, "E1905", {"start": v(1.43, 29.08) * mm, "end": v(1.31, 29.36) * mm});
            skLineSegment(sketch, "E1906", {"start": v(1.31, 29.36) * mm, "end": v(1.2, 29.65) * mm});
            skLineSegment(sketch, "E1907", {"start": v(1.2, 29.65) * mm, "end": v(1.08, 29.94) * mm});
            skLineSegment(sketch, "E1908", {"start": v(1.08, 29.94) * mm, "end": v(0.95, 30.22) * mm});
            skLineSegment(sketch, "E1909", {"start": v(0.95, 30.22) * mm, "end": v(0.82, 30.51) * mm});
            skLineSegment(sketch, "E1910", {"start": v(0.82, 30.51) * mm, "end": v(0.8, 30.55) * mm});
            skLineSegment(sketch, "E1911", {"start": v(0.8, 30.55) * mm, "end": v(-0.59, 30.55) * mm});
            skLineSegment(sketch, "E1912", {"start": v(-0.59, 30.55) * mm, "end": v(-0.63, 30.46) * mm});
            skLineSegment(sketch, "E1913", {"start": v(-0.63, 30.46) * mm, "end": v(-0.78, 30.18) * mm});
            skLineSegment(sketch, "E1914", {"start": v(-0.78, 30.18) * mm, "end": v(-0.93, 29.9) * mm});
            skLineSegment(sketch, "E1915", {"start": v(-0.93, 29.9) * mm, "end": v(-1.07, 29.6) * mm});
            skLineSegment(sketch, "E1916", {"start": v(-1.07, 29.6) * mm, "end": v(-1.2, 29.32) * mm});
            skLineSegment(sketch, "E1917", {"start": v(-1.2, 29.32) * mm, "end": v(-1.33, 29.03) * mm});
            skLineSegment(sketch, "E1918", {"start": v(-1.33, 29.03) * mm, "end": v(-1.46, 28.75) * mm});
            skLineSegment(sketch, "E1919", {"start": v(-1.46, 28.75) * mm, "end": v(-1.58, 28.46) * mm});
            skLineSegment(sketch, "E1920", {"start": v(-1.58, 28.46) * mm, "end": v(-1.7, 28.17) * mm});
            skLineSegment(sketch, "E1921", {"start": v(-1.7, 28.17) * mm, "end": v(-1.8, 27.89) * mm});
            skLineSegment(sketch, "E1922", {"start": v(-1.8, 27.89) * mm, "end": v(-1.9, 27.6) * mm});
            skLineSegment(sketch, "E1923", {"start": v(-1.9, 27.6) * mm, "end": v(-2, 27.31) * mm});
            skLineSegment(sketch, "E1924", {"start": v(-2, 27.31) * mm, "end": v(-2.1, 27.02) * mm});
            skLineSegment(sketch, "E1925", {"start": v(-2.1, 27.02) * mm, "end": v(-2.19, 26.74) * mm});
            skLineSegment(sketch, "E1926", {"start": v(-2.19, 26.74) * mm, "end": v(-2.27, 26.45) * mm});
            skLineSegment(sketch, "E1927", {"start": v(-2.27, 26.45) * mm, "end": v(-2.35, 26.16) * mm});
            skLineSegment(sketch, "E1928", {"start": v(-2.35, 26.16) * mm, "end": v(-2.43, 25.87) * mm});
            skLineSegment(sketch, "E1929", {"start": v(-2.43, 25.87) * mm, "end": v(-2.5, 25.59) * mm});
            skLineSegment(sketch, "E1930", {"start": v(-2.5, 25.59) * mm, "end": v(-2.56, 25.3) * mm});
            skLineSegment(sketch, "E1931", {"start": v(-2.56, 25.3) * mm, "end": v(-2.62, 25.01) * mm});
            skLineSegment(sketch, "E1932", {"start": v(-2.62, 25.01) * mm, "end": v(-2.67, 24.72) * mm});
            skLineSegment(sketch, "E1933", {"start": v(-2.67, 24.72) * mm, "end": v(-2.72, 24.43) * mm});
            skLineSegment(sketch, "E1934", {"start": v(-2.72, 24.43) * mm, "end": v(-2.76, 24.15) * mm});
            skLineSegment(sketch, "E1935", {"start": v(-2.76, 24.15) * mm, "end": v(-2.8, 23.86) * mm});
            skLineSegment(sketch, "E1936", {"start": v(-2.8, 23.86) * mm, "end": v(-2.84, 23.57) * mm});
            skLineSegment(sketch, "E1937", {"start": v(-2.84, 23.57) * mm, "end": v(-2.86, 23.28) * mm});
            skLineSegment(sketch, "E1938", {"start": v(-2.86, 23.28) * mm, "end": v(-2.89, 23) * mm});
            skLineSegment(sketch, "E1939", {"start": v(-2.89, 23) * mm, "end": v(-2.9, 22.7) * mm});
            skLineSegment(sketch, "E1940", {"start": v(-2.9, 22.7) * mm, "end": v(-2.92, 22.41) * mm});
            skLineSegment(sketch, "E1941", {"start": v(-2.92, 22.41) * mm, "end": v(-2.93, 22.12) * mm});
            skLineSegment(sketch, "E1942", {"start": v(-2.93, 22.12) * mm, "end": v(-2.93, 21.83) * mm});
            skLineSegment(sketch, "E1943", {"start": v(-2.93, 21.83) * mm, "end": v(-2.93, 21.54) * mm});
            skLineSegment(sketch, "E1944", {"start": v(-2.93, 21.54) * mm, "end": v(-2.92, 21.26) * mm});
            skLineSegment(sketch, "E1945", {"start": v(-2.92, 21.26) * mm, "end": v(-2.9, 20.97) * mm});
            skLineSegment(sketch, "E1946", {"start": v(-2.9, 20.97) * mm, "end": v(-2.89, 20.69) * mm});
            skLineSegment(sketch, "E1947", {"start": v(-2.89, 20.69) * mm, "end": v(-2.87, 20.4) * mm});
            skLineSegment(sketch, "E1948", {"start": v(-2.87, 20.4) * mm, "end": v(-2.84, 20.12) * mm});
            skLineSegment(sketch, "E1949", {"start": v(-2.84, 20.12) * mm, "end": v(-2.8, 19.83) * mm});
            skLineSegment(sketch, "E1950", {"start": v(-2.8, 19.83) * mm, "end": v(-2.77, 19.55) * mm});
            skLineSegment(sketch, "E1951", {"start": v(-2.77, 19.55) * mm, "end": v(-2.73, 19.26) * mm});
            skLineSegment(sketch, "E1952", {"start": v(-2.73, 19.26) * mm, "end": v(-2.68, 18.98) * mm});
            skLineSegment(sketch, "E1953", {"start": v(-2.68, 18.98) * mm, "end": v(-2.63, 18.7) * mm});
            skLineSegment(sketch, "E1954", {"start": v(-2.63, 18.7) * mm, "end": v(-2.57, 18.41) * mm});
            skLineSegment(sketch, "E1955", {"start": v(-2.57, 18.41) * mm, "end": v(-2.5, 18.13) * mm});
            skLineSegment(sketch, "E1956", {"start": v(-2.5, 18.13) * mm, "end": v(-2.44, 17.84) * mm});
            skLineSegment(sketch, "E1957", {"start": v(-2.44, 17.84) * mm, "end": v(-2.37, 17.56) * mm});
            skLineSegment(sketch, "E1958", {"start": v(-2.37, 17.56) * mm, "end": v(-2.3, 17.28) * mm});
            skLineSegment(sketch, "E1959", {"start": v(-2.3, 17.28) * mm, "end": v(-2.2, 17) * mm});
            skLineSegment(sketch, "E1960", {"start": v(-2.2, 17) * mm, "end": v(-2.12, 16.7) * mm});
            skLineSegment(sketch, "E1961", {"start": v(-2.12, 16.7) * mm, "end": v(-2.03, 16.43) * mm});
            skLineSegment(sketch, "E1962", {"start": v(-2.03, 16.43) * mm, "end": v(-1.93, 16.14) * mm});
            skLineSegment(sketch, "E1963", {"start": v(-1.93, 16.14) * mm, "end": v(-1.83, 15.86) * mm});
            skLineSegment(sketch, "E1964", {"start": v(-1.83, 15.86) * mm, "end": v(-1.73, 15.58) * mm});
            skLineSegment(sketch, "E1965", {"start": v(-1.73, 15.58) * mm, "end": v(-1.61, 15.3) * mm});
            skLineSegment(sketch, "E1966", {"start": v(-1.61, 15.3) * mm, "end": v(-1.5, 15.01) * mm});
            skLineSegment(sketch, "E1967", {"start": v(-1.5, 15.01) * mm, "end": v(-1.38, 14.73) * mm});
            skLineSegment(sketch, "E1968", {"start": v(-1.38, 14.73) * mm, "end": v(-1.25, 14.45) * mm});
            skLineSegment(sketch, "E1969", {"start": v(-1.25, 14.45) * mm, "end": v(-1.12, 14.17) * mm});
            skLineSegment(sketch, "E1970", {"start": v(-1.12, 14.17) * mm, "end": v(-0.98, 13.88) * mm});
            skLineSegment(sketch, "E1971", {"start": v(-0.98, 13.88) * mm, "end": v(-0.84, 13.6) * mm});
            skLineSegment(sketch, "E1972", {"start": v(-0.84, 13.6) * mm, "end": v(-0.7, 13.32) * mm});
            skLineSegment(sketch, "E1973", {"start": v(-0.7, 13.32) * mm, "end": v(-0.66, 13.25) * mm});
            skLineSegment(sketch, "E1974", {"start": v(-0.66, 13.25) * mm, "end": v(0.87, 13.25) * mm});
            skLineSegment(sketch, "E1975", {"start": v(0.87, 13.25) * mm, "end": v(0.88, 13.27) * mm});
            skLineSegment(sketch, "E1976", {"start": v(22.12, -2.8) * mm, "end": v(22.42, -2.8) * mm});
            skLineSegment(sketch, "E1977", {"start": v(22.42, -2.8) * mm, "end": v(22.7, -2.79) * mm});
            skLineSegment(sketch, "E1978", {"start": v(22.7, -2.79) * mm, "end": v(23, -2.77) * mm});
            skLineSegment(sketch, "E1979", {"start": v(23, -2.77) * mm, "end": v(23.3, -2.75) * mm});
            skLineSegment(sketch, "E1980", {"start": v(23.3, -2.75) * mm, "end": v(23.58, -2.73) * mm});
            skLineSegment(sketch, "E1981", {"start": v(23.58, -2.73) * mm, "end": v(23.87, -2.7) * mm});
            skLineSegment(sketch, "E1982", {"start": v(23.87, -2.7) * mm, "end": v(24.16, -2.66) * mm});
            skLineSegment(sketch, "E1983", {"start": v(24.16, -2.66) * mm, "end": v(24.45, -2.63) * mm});
            skLineSegment(sketch, "E1984", {"start": v(24.45, -2.63) * mm, "end": v(24.74, -2.58) * mm});
            skLineSegment(sketch, "E1985", {"start": v(24.74, -2.58) * mm, "end": v(25.03, -2.54) * mm});
            skLineSegment(sketch, "E1986", {"start": v(25.03, -2.54) * mm, "end": v(25.32, -2.49) * mm});
            skLineSegment(sketch, "E1987", {"start": v(25.32, -2.49) * mm, "end": v(25.61, -2.43) * mm});
            skLineSegment(sketch, "E1988", {"start": v(25.61, -2.43) * mm, "end": v(25.9, -2.37) * mm});
            skLineSegment(sketch, "E1989", {"start": v(25.9, -2.37) * mm, "end": v(26.2, -2.3) * mm});
            skLineSegment(sketch, "E1990", {"start": v(26.2, -2.3) * mm, "end": v(26.48, -2.24) * mm});
            skLineSegment(sketch, "E1991", {"start": v(26.48, -2.24) * mm, "end": v(26.77, -2.17) * mm});
            skLineSegment(sketch, "E1992", {"start": v(26.77, -2.17) * mm, "end": v(27.06, -2.09) * mm});
            skLineSegment(sketch, "E1993", {"start": v(27.06, -2.09) * mm, "end": v(27.35, -2) * mm});
            skLineSegment(sketch, "E1994", {"start": v(27.35, -2) * mm, "end": v(27.64, -1.92) * mm});
            skLineSegment(sketch, "E1995", {"start": v(27.64, -1.92) * mm, "end": v(27.92, -1.83) * mm});
            skLineSegment(sketch, "E1996", {"start": v(27.92, -1.83) * mm, "end": v(28.21, -1.74) * mm});
            skLineSegment(sketch, "E1997", {"start": v(28.21, -1.74) * mm, "end": v(28.5, -1.64) * mm});
            skLineSegment(sketch, "E1998", {"start": v(28.5, -1.64) * mm, "end": v(28.79, -1.53) * mm});
            skLineSegment(sketch, "E1999", {"start": v(28.79, -1.53) * mm, "end": v(29.08, -1.43) * mm});
            skLineSegment(sketch, "E2000", {"start": v(29.08, -1.43) * mm, "end": v(29.36, -1.31) * mm});
            skLineSegment(sketch, "E2001", {"start": v(29.36, -1.31) * mm, "end": v(29.65, -1.2) * mm});
            skLineSegment(sketch, "E2002", {"start": v(29.65, -1.2) * mm, "end": v(29.94, -1.08) * mm});
            skLineSegment(sketch, "E2003", {"start": v(29.94, -1.08) * mm, "end": v(30.22, -0.95) * mm});
            skLineSegment(sketch, "E2004", {"start": v(30.22, -0.95) * mm, "end": v(30.51, -0.82) * mm});
            skLineSegment(sketch, "E2005", {"start": v(30.51, -0.82) * mm, "end": v(30.55, -0.8) * mm});
            skLineSegment(sketch, "E2006", {"start": v(30.55, -0.8) * mm, "end": v(30.55, 0.59) * mm});
            skLineSegment(sketch, "E2007", {"start": v(30.55, 0.59) * mm, "end": v(30.46, 0.63) * mm});
            skLineSegment(sketch, "E2008", {"start": v(30.46, 0.63) * mm, "end": v(30.18, 0.78) * mm});
            skLineSegment(sketch, "E2009", {"start": v(30.18, 0.78) * mm, "end": v(29.9, 0.93) * mm});
            skLineSegment(sketch, "E2010", {"start": v(29.9, 0.93) * mm, "end": v(29.6, 1.07) * mm});
            skLineSegment(sketch, "E2011", {"start": v(29.6, 1.07) * mm, "end": v(29.32, 1.2) * mm});
            skLineSegment(sketch, "E2012", {"start": v(29.32, 1.2) * mm, "end": v(29.03, 1.33) * mm});
            skLineSegment(sketch, "E2013", {"start": v(29.03, 1.33) * mm, "end": v(28.75, 1.46) * mm});
            skLineSegment(sketch, "E2014", {"start": v(28.75, 1.46) * mm, "end": v(28.46, 1.58) * mm});
            skLineSegment(sketch, "E2015", {"start": v(28.46, 1.58) * mm, "end": v(28.17, 1.7) * mm});
            skLineSegment(sketch, "E2016", {"start": v(28.17, 1.7) * mm, "end": v(27.89, 1.8) * mm});
            skLineSegment(sketch, "E2017", {"start": v(27.89, 1.8) * mm, "end": v(27.6, 1.9) * mm});
            skLineSegment(sketch, "E2018", {"start": v(27.6, 1.9) * mm, "end": v(27.31, 2) * mm});
            skLineSegment(sketch, "E2019", {"start": v(27.31, 2) * mm, "end": v(27.02, 2.1) * mm});
            skLineSegment(sketch, "E2020", {"start": v(27.02, 2.1) * mm, "end": v(26.74, 2.19) * mm});
            skLineSegment(sketch, "E2021", {"start": v(26.74, 2.19) * mm, "end": v(26.45, 2.27) * mm});
            skLineSegment(sketch, "E2022", {"start": v(26.45, 2.27) * mm, "end": v(26.16, 2.35) * mm});
            skLineSegment(sketch, "E2023", {"start": v(26.16, 2.35) * mm, "end": v(25.87, 2.43) * mm});
            skLineSegment(sketch, "E2024", {"start": v(25.87, 2.43) * mm, "end": v(25.59, 2.5) * mm});
            skLineSegment(sketch, "E2025", {"start": v(25.59, 2.5) * mm, "end": v(25.3, 2.56) * mm});
            skLineSegment(sketch, "E2026", {"start": v(25.3, 2.56) * mm, "end": v(25.01, 2.62) * mm});
            skLineSegment(sketch, "E2027", {"start": v(25.01, 2.62) * mm, "end": v(24.72, 2.67) * mm});
            skLineSegment(sketch, "E2028", {"start": v(24.72, 2.67) * mm, "end": v(24.43, 2.72) * mm});
            skLineSegment(sketch, "E2029", {"start": v(24.43, 2.72) * mm, "end": v(24.15, 2.76) * mm});
            skLineSegment(sketch, "E2030", {"start": v(24.15, 2.76) * mm, "end": v(23.86, 2.8) * mm});
            skLineSegment(sketch, "E2031", {"start": v(23.86, 2.8) * mm, "end": v(23.57, 2.84) * mm});
            skLineSegment(sketch, "E2032", {"start": v(23.57, 2.84) * mm, "end": v(23.28, 2.86) * mm});
            skLineSegment(sketch, "E2033", {"start": v(23.28, 2.86) * mm, "end": v(23, 2.89) * mm});
            skLineSegment(sketch, "E2034", {"start": v(23, 2.89) * mm, "end": v(22.7, 2.9) * mm});
            skLineSegment(sketch, "E2035", {"start": v(22.7, 2.9) * mm, "end": v(22.41, 2.92) * mm});
            skLineSegment(sketch, "E2036", {"start": v(22.41, 2.92) * mm, "end": v(22.12, 2.93) * mm});
            skLineSegment(sketch, "E2037", {"start": v(22.12, 2.93) * mm, "end": v(21.83, 2.93) * mm});
            skLineSegment(sketch, "E2038", {"start": v(21.83, 2.93) * mm, "end": v(21.54, 2.93) * mm});
            skLineSegment(sketch, "E2039", {"start": v(21.54, 2.93) * mm, "end": v(21.26, 2.92) * mm});
            skLineSegment(sketch, "E2040", {"start": v(21.26, 2.92) * mm, "end": v(20.97, 2.9) * mm});
            skLineSegment(sketch, "E2041", {"start": v(20.97, 2.9) * mm, "end": v(20.69, 2.89) * mm});
            skLineSegment(sketch, "E2042", {"start": v(20.69, 2.89) * mm, "end": v(20.4, 2.87) * mm});
            skLineSegment(sketch, "E2043", {"start": v(20.4, 2.87) * mm, "end": v(20.12, 2.84) * mm});
            skLineSegment(sketch, "E2044", {"start": v(20.12, 2.84) * mm, "end": v(19.83, 2.8) * mm});
            skLineSegment(sketch, "E2045", {"start": v(19.83, 2.8) * mm, "end": v(19.55, 2.77) * mm});
            skLineSegment(sketch, "E2046", {"start": v(19.55, 2.77) * mm, "end": v(19.26, 2.73) * mm});
            skLineSegment(sketch, "E2047", {"start": v(19.26, 2.73) * mm, "end": v(18.98, 2.68) * mm});
            skLineSegment(sketch, "E2048", {"start": v(18.98, 2.68) * mm, "end": v(18.7, 2.63) * mm});
            skLineSegment(sketch, "E2049", {"start": v(18.7, 2.63) * mm, "end": v(18.41, 2.57) * mm});
            skLineSegment(sketch, "E2050", {"start": v(18.41, 2.57) * mm, "end": v(18.13, 2.5) * mm});
            skLineSegment(sketch, "E2051", {"start": v(18.13, 2.5) * mm, "end": v(17.84, 2.44) * mm});
            skLineSegment(sketch, "E2052", {"start": v(17.84, 2.44) * mm, "end": v(17.56, 2.37) * mm});
            skLineSegment(sketch, "E2053", {"start": v(17.56, 2.37) * mm, "end": v(17.28, 2.3) * mm});
            skLineSegment(sketch, "E2054", {"start": v(17.28, 2.3) * mm, "end": v(17, 2.2) * mm});
            skLineSegment(sketch, "E2055", {"start": v(17, 2.2) * mm, "end": v(16.7, 2.12) * mm});
            skLineSegment(sketch, "E2056", {"start": v(16.7, 2.12) * mm, "end": v(16.43, 2.03) * mm});
            skLineSegment(sketch, "E2057", {"start": v(16.43, 2.03) * mm, "end": v(16.14, 1.93) * mm});
            skLineSegment(sketch, "E2058", {"start": v(16.14, 1.93) * mm, "end": v(15.86, 1.83) * mm});
            skLineSegment(sketch, "E2059", {"start": v(15.86, 1.83) * mm, "end": v(15.58, 1.73) * mm});
            skLineSegment(sketch, "E2060", {"start": v(15.58, 1.73) * mm, "end": v(15.3, 1.61) * mm});
            skLineSegment(sketch, "E2061", {"start": v(15.3, 1.61) * mm, "end": v(15.01, 1.5) * mm});
            skLineSegment(sketch, "E2062", {"start": v(15.01, 1.5) * mm, "end": v(14.73, 1.38) * mm});
            skLineSegment(sketch, "E2063", {"start": v(14.73, 1.38) * mm, "end": v(14.45, 1.25) * mm});
            skLineSegment(sketch, "E2064", {"start": v(14.45, 1.25) * mm, "end": v(14.17, 1.12) * mm});
            skLineSegment(sketch, "E2065", {"start": v(14.17, 1.12) * mm, "end": v(13.88, 0.98) * mm});
            skLineSegment(sketch, "E2066", {"start": v(13.88, 0.98) * mm, "end": v(13.6, 0.84) * mm});
            skLineSegment(sketch, "E2067", {"start": v(13.6, 0.84) * mm, "end": v(13.32, 0.7) * mm});
            skLineSegment(sketch, "E2068", {"start": v(13.32, 0.7) * mm, "end": v(13.25, 0.66) * mm});
            skLineSegment(sketch, "E2069", {"start": v(13.25, 0.66) * mm, "end": v(13.25, -0.87) * mm});
            skLineSegment(sketch, "E2070", {"start": v(13.25, -0.87) * mm, "end": v(13.27, -0.88) * mm});
            skLineSegment(sketch, "E2071", {"start": v(13.27, -0.88) * mm, "end": v(13.55, -1) * mm});
            skLineSegment(sketch, "E2072", {"start": v(13.55, -1) * mm, "end": v(13.84, -1.13) * mm});
            skLineSegment(sketch, "E2073", {"start": v(13.84, -1.13) * mm, "end": v(14.12, -1.24) * mm});
            skLineSegment(sketch, "E2074", {"start": v(14.12, -1.24) * mm, "end": v(14.4, -1.36) * mm});
            skLineSegment(sketch, "E2075", {"start": v(14.4, -1.36) * mm, "end": v(14.69, -1.46) * mm});
            skLineSegment(sketch, "E2076", {"start": v(14.69, -1.46) * mm, "end": v(14.97, -1.57) * mm});
            skLineSegment(sketch, "E2077", {"start": v(14.97, -1.57) * mm, "end": v(15.25, -1.67) * mm});
            skLineSegment(sketch, "E2078", {"start": v(15.25, -1.67) * mm, "end": v(15.54, -1.77) * mm});
            skLineSegment(sketch, "E2079", {"start": v(15.54, -1.77) * mm, "end": v(15.82, -1.86) * mm});
            skLineSegment(sketch, "E2080", {"start": v(15.82, -1.86) * mm, "end": v(16.1, -1.95) * mm});
            skLineSegment(sketch, "E2081", {"start": v(16.1, -1.95) * mm, "end": v(16.4, -2.03) * mm});
            skLineSegment(sketch, "E2082", {"start": v(16.4, -2.03) * mm, "end": v(16.68, -2.1) * mm});
            skLineSegment(sketch, "E2083", {"start": v(16.68, -2.1) * mm, "end": v(16.96, -2.18) * mm});
            skLineSegment(sketch, "E2084", {"start": v(16.96, -2.18) * mm, "end": v(17.24, -2.25) * mm});
            skLineSegment(sketch, "E2085", {"start": v(17.24, -2.25) * mm, "end": v(17.53, -2.32) * mm});
            skLineSegment(sketch, "E2086", {"start": v(17.53, -2.32) * mm, "end": v(17.82, -2.38) * mm});
            skLineSegment(sketch, "E2087", {"start": v(17.82, -2.38) * mm, "end": v(18.1, -2.44) * mm});
            skLineSegment(sketch, "E2088", {"start": v(18.1, -2.44) * mm, "end": v(18.39, -2.5) * mm});
            skLineSegment(sketch, "E2089", {"start": v(18.39, -2.5) * mm, "end": v(18.67, -2.54) * mm});
            skLineSegment(sketch, "E2090", {"start": v(18.67, -2.54) * mm, "end": v(18.96, -2.59) * mm});
            skLineSegment(sketch, "E2091", {"start": v(18.96, -2.59) * mm, "end": v(19.24, -2.63) * mm});
            skLineSegment(sketch, "E2092", {"start": v(19.24, -2.63) * mm, "end": v(19.53, -2.67) * mm});
            skLineSegment(sketch, "E2093", {"start": v(19.53, -2.67) * mm, "end": v(19.82, -2.7) * mm});
            skLineSegment(sketch, "E2094", {"start": v(19.82, -2.7) * mm, "end": v(20.1, -2.73) * mm});
            skLineSegment(sketch, "E2095", {"start": v(20.1, -2.73) * mm, "end": v(20.4, -2.75) * mm});
            skLineSegment(sketch, "E2096", {"start": v(20.4, -2.75) * mm, "end": v(20.68, -2.77) * mm});
            skLineSegment(sketch, "E2097", {"start": v(20.68, -2.77) * mm, "end": v(20.97, -2.79) * mm});
            skLineSegment(sketch, "E2098", {"start": v(20.97, -2.79) * mm, "end": v(21.25, -2.8) * mm});
            skLineSegment(sketch, "E2099", {"start": v(21.25, -2.8) * mm, "end": v(21.54, -2.8) * mm});
            skLineSegment(sketch, "E2100", {"start": v(21.54, -2.8) * mm, "end": v(21.83, -2.8) * mm});
            skLineSegment(sketch, "E2101", {"start": v(21.83, -2.8) * mm, "end": v(22.12, -2.8) * mm});
            skLineSegment(sketch, "E2102", {"start": v(-21.54, -2.93) * mm, "end": v(-21.26, -2.92) * mm});
            skLineSegment(sketch, "E2103", {"start": v(-21.26, -2.92) * mm, "end": v(-20.97, -2.9) * mm});
            skLineSegment(sketch, "E2104", {"start": v(-20.97, -2.9) * mm, "end": v(-20.69, -2.89) * mm});
            skLineSegment(sketch, "E2105", {"start": v(-20.69, -2.89) * mm, "end": v(-20.4, -2.87) * mm});
            skLineSegment(sketch, "E2106", {"start": v(-20.4, -2.87) * mm, "end": v(-20.12, -2.84) * mm});
            skLineSegment(sketch, "E2107", {"start": v(-20.12, -2.84) * mm, "end": v(-19.83, -2.8) * mm});
            skLineSegment(sketch, "E2108", {"start": v(-19.83, -2.8) * mm, "end": v(-19.55, -2.77) * mm});
            skLineSegment(sketch, "E2109", {"start": v(-19.55, -2.77) * mm, "end": v(-19.26, -2.73) * mm});
            skLineSegment(sketch, "E2110", {"start": v(-19.26, -2.73) * mm, "end": v(-18.98, -2.68) * mm});
            skLineSegment(sketch, "E2111", {"start": v(-18.98, -2.68) * mm, "end": v(-18.7, -2.63) * mm});
            skLineSegment(sketch, "E2112", {"start": v(-18.7, -2.63) * mm, "end": v(-18.41, -2.57) * mm});
            skLineSegment(sketch, "E2113", {"start": v(-18.41, -2.57) * mm, "end": v(-18.13, -2.5) * mm});
            skLineSegment(sketch, "E2114", {"start": v(-18.13, -2.5) * mm, "end": v(-17.84, -2.44) * mm});
            skLineSegment(sketch, "E2115", {"start": v(-17.84, -2.44) * mm, "end": v(-17.56, -2.37) * mm});
            skLineSegment(sketch, "E2116", {"start": v(-17.56, -2.37) * mm, "end": v(-17.28, -2.3) * mm});
            skLineSegment(sketch, "E2117", {"start": v(-17.28, -2.3) * mm, "end": v(-17, -2.2) * mm});
            skLineSegment(sketch, "E2118", {"start": v(-17, -2.2) * mm, "end": v(-16.7, -2.12) * mm});
            skLineSegment(sketch, "E2119", {"start": v(-16.7, -2.12) * mm, "end": v(-16.43, -2.03) * mm});
            skLineSegment(sketch, "E2120", {"start": v(-16.43, -2.03) * mm, "end": v(-16.14, -1.93) * mm});
            skLineSegment(sketch, "E2121", {"start": v(-16.14, -1.93) * mm, "end": v(-15.86, -1.83) * mm});
            skLineSegment(sketch, "E2122", {"start": v(-15.86, -1.83) * mm, "end": v(-15.58, -1.73) * mm});
            skLineSegment(sketch, "E2123", {"start": v(-15.58, -1.73) * mm, "end": v(-15.3, -1.61) * mm});
            skLineSegment(sketch, "E2124", {"start": v(-15.3, -1.61) * mm, "end": v(-15.01, -1.5) * mm});
            skLineSegment(sketch, "E2125", {"start": v(-15.01, -1.5) * mm, "end": v(-14.73, -1.38) * mm});
            skLineSegment(sketch, "E2126", {"start": v(-14.73, -1.38) * mm, "end": v(-14.45, -1.25) * mm});
            skLineSegment(sketch, "E2127", {"start": v(-14.45, -1.25) * mm, "end": v(-14.17, -1.12) * mm});
            skLineSegment(sketch, "E2128", {"start": v(-14.17, -1.12) * mm, "end": v(-13.88, -0.98) * mm});
            skLineSegment(sketch, "E2129", {"start": v(-13.88, -0.98) * mm, "end": v(-13.6, -0.84) * mm});
            skLineSegment(sketch, "E2130", {"start": v(-13.6, -0.84) * mm, "end": v(-13.32, -0.7) * mm});
            skLineSegment(sketch, "E2131", {"start": v(-13.32, -0.7) * mm, "end": v(-13.25, -0.66) * mm});
            skLineSegment(sketch, "E2132", {"start": v(-13.25, -0.66) * mm, "end": v(-13.25, 0.87) * mm});
            skLineSegment(sketch, "E2133", {"start": v(-13.25, 0.87) * mm, "end": v(-13.27, 0.88) * mm});
            skLineSegment(sketch, "E2134", {"start": v(-13.27, 0.88) * mm, "end": v(-13.55, 1) * mm});
            skLineSegment(sketch, "E2135", {"start": v(-13.55, 1) * mm, "end": v(-13.84, 1.13) * mm});
            skLineSegment(sketch, "E2136", {"start": v(-13.84, 1.13) * mm, "end": v(-14.12, 1.24) * mm});
            skLineSegment(sketch, "E2137", {"start": v(-14.12, 1.24) * mm, "end": v(-14.4, 1.36) * mm});
            skLineSegment(sketch, "E2138", {"start": v(-14.4, 1.36) * mm, "end": v(-14.69, 1.46) * mm});
            skLineSegment(sketch, "E2139", {"start": v(-14.69, 1.46) * mm, "end": v(-14.97, 1.57) * mm});
            skLineSegment(sketch, "E2140", {"start": v(-14.97, 1.57) * mm, "end": v(-15.25, 1.67) * mm});
            skLineSegment(sketch, "E2141", {"start": v(-15.25, 1.67) * mm, "end": v(-15.54, 1.77) * mm});
            skLineSegment(sketch, "E2142", {"start": v(-15.54, 1.77) * mm, "end": v(-15.82, 1.86) * mm});
            skLineSegment(sketch, "E2143", {"start": v(-15.82, 1.86) * mm, "end": v(-16.1, 1.95) * mm});
            skLineSegment(sketch, "E2144", {"start": v(-16.1, 1.95) * mm, "end": v(-16.4, 2.03) * mm});
            skLineSegment(sketch, "E2145", {"start": v(-16.4, 2.03) * mm, "end": v(-16.68, 2.1) * mm});
            skLineSegment(sketch, "E2146", {"start": v(-16.68, 2.1) * mm, "end": v(-16.96, 2.18) * mm});
            skLineSegment(sketch, "E2147", {"start": v(-16.96, 2.18) * mm, "end": v(-17.24, 2.25) * mm});
            skLineSegment(sketch, "E2148", {"start": v(-17.24, 2.25) * mm, "end": v(-17.53, 2.32) * mm});
            skLineSegment(sketch, "E2149", {"start": v(-17.53, 2.32) * mm, "end": v(-17.82, 2.38) * mm});
            skLineSegment(sketch, "E2150", {"start": v(-17.82, 2.38) * mm, "end": v(-18.1, 2.44) * mm});
            skLineSegment(sketch, "E2151", {"start": v(-18.1, 2.44) * mm, "end": v(-18.39, 2.5) * mm});
            skLineSegment(sketch, "E2152", {"start": v(-18.39, 2.5) * mm, "end": v(-18.67, 2.54) * mm});
            skLineSegment(sketch, "E2153", {"start": v(-18.67, 2.54) * mm, "end": v(-18.96, 2.59) * mm});
            skLineSegment(sketch, "E2154", {"start": v(-18.96, 2.59) * mm, "end": v(-19.24, 2.63) * mm});
            skLineSegment(sketch, "E2155", {"start": v(-19.24, 2.63) * mm, "end": v(-19.53, 2.67) * mm});
            skLineSegment(sketch, "E2156", {"start": v(-19.53, 2.67) * mm, "end": v(-19.82, 2.7) * mm});
            skLineSegment(sketch, "E2157", {"start": v(-19.82, 2.7) * mm, "end": v(-20.1, 2.73) * mm});
            skLineSegment(sketch, "E2158", {"start": v(-20.1, 2.73) * mm, "end": v(-20.4, 2.75) * mm});
            skLineSegment(sketch, "E2159", {"start": v(-20.4, 2.75) * mm, "end": v(-20.68, 2.77) * mm});
            skLineSegment(sketch, "E2160", {"start": v(-20.68, 2.77) * mm, "end": v(-20.97, 2.79) * mm});
            skLineSegment(sketch, "E2161", {"start": v(-20.97, 2.79) * mm, "end": v(-21.25, 2.8) * mm});
            skLineSegment(sketch, "E2162", {"start": v(-21.25, 2.8) * mm, "end": v(-21.54, 2.8) * mm});
            skLineSegment(sketch, "E2163", {"start": v(-21.54, 2.8) * mm, "end": v(-21.83, 2.8) * mm});
            skLineSegment(sketch, "E2164", {"start": v(-21.83, 2.8) * mm, "end": v(-22.12, 2.8) * mm});
            skLineSegment(sketch, "E2165", {"start": v(-22.12, 2.8) * mm, "end": v(-22.42, 2.8) * mm});
            skLineSegment(sketch, "E2166", {"start": v(-22.42, 2.8) * mm, "end": v(-22.7, 2.79) * mm});
            skLineSegment(sketch, "E2167", {"start": v(-22.7, 2.79) * mm, "end": v(-23, 2.77) * mm});
            skLineSegment(sketch, "E2168", {"start": v(-23, 2.77) * mm, "end": v(-23.3, 2.75) * mm});
            skLineSegment(sketch, "E2169", {"start": v(-23.3, 2.75) * mm, "end": v(-23.58, 2.73) * mm});
            skLineSegment(sketch, "E2170", {"start": v(-23.58, 2.73) * mm, "end": v(-23.87, 2.7) * mm});
            skLineSegment(sketch, "E2171", {"start": v(-23.87, 2.7) * mm, "end": v(-24.16, 2.66) * mm});
            skLineSegment(sketch, "E2172", {"start": v(-24.16, 2.66) * mm, "end": v(-24.45, 2.63) * mm});
            skLineSegment(sketch, "E2173", {"start": v(-24.45, 2.63) * mm, "end": v(-24.74, 2.58) * mm});
            skLineSegment(sketch, "E2174", {"start": v(-24.74, 2.58) * mm, "end": v(-25.03, 2.54) * mm});
            skLineSegment(sketch, "E2175", {"start": v(-25.03, 2.54) * mm, "end": v(-25.32, 2.49) * mm});
            skLineSegment(sketch, "E2176", {"start": v(-25.32, 2.49) * mm, "end": v(-25.61, 2.43) * mm});
            skLineSegment(sketch, "E2177", {"start": v(-25.61, 2.43) * mm, "end": v(-25.9, 2.37) * mm});
            skLineSegment(sketch, "E2178", {"start": v(-25.9, 2.37) * mm, "end": v(-26.2, 2.3) * mm});
            skLineSegment(sketch, "E2179", {"start": v(-26.2, 2.3) * mm, "end": v(-26.48, 2.24) * mm});
            skLineSegment(sketch, "E2180", {"start": v(-26.48, 2.24) * mm, "end": v(-26.77, 2.17) * mm});
            skLineSegment(sketch, "E2181", {"start": v(-26.77, 2.17) * mm, "end": v(-27.06, 2.09) * mm});
            skLineSegment(sketch, "E2182", {"start": v(-27.06, 2.09) * mm, "end": v(-27.35, 2) * mm});
            skLineSegment(sketch, "E2183", {"start": v(-27.35, 2) * mm, "end": v(-27.64, 1.92) * mm});
            skLineSegment(sketch, "E2184", {"start": v(-27.64, 1.92) * mm, "end": v(-27.92, 1.83) * mm});
            skLineSegment(sketch, "E2185", {"start": v(-27.92, 1.83) * mm, "end": v(-28.21, 1.74) * mm});
            skLineSegment(sketch, "E2186", {"start": v(-28.21, 1.74) * mm, "end": v(-28.5, 1.64) * mm});
            skLineSegment(sketch, "E2187", {"start": v(-28.5, 1.64) * mm, "end": v(-28.79, 1.53) * mm});
            skLineSegment(sketch, "E2188", {"start": v(-28.79, 1.53) * mm, "end": v(-29.08, 1.43) * mm});
            skLineSegment(sketch, "E2189", {"start": v(-29.08, 1.43) * mm, "end": v(-29.36, 1.31) * mm});
            skLineSegment(sketch, "E2190", {"start": v(-29.36, 1.31) * mm, "end": v(-29.65, 1.2) * mm});
            skLineSegment(sketch, "E2191", {"start": v(-29.65, 1.2) * mm, "end": v(-29.94, 1.08) * mm});
            skLineSegment(sketch, "E2192", {"start": v(-29.94, 1.08) * mm, "end": v(-30.22, 0.95) * mm});
            skLineSegment(sketch, "E2193", {"start": v(-30.22, 0.95) * mm, "end": v(-30.51, 0.82) * mm});
            skLineSegment(sketch, "E2194", {"start": v(-30.51, 0.82) * mm, "end": v(-30.55, 0.8) * mm});
            skLineSegment(sketch, "E2195", {"start": v(-30.55, 0.8) * mm, "end": v(-30.55, -0.59) * mm});
            skLineSegment(sketch, "E2196", {"start": v(-30.55, -0.59) * mm, "end": v(-30.46, -0.63) * mm});
            skLineSegment(sketch, "E2197", {"start": v(-30.46, -0.63) * mm, "end": v(-30.18, -0.78) * mm});
            skLineSegment(sketch, "E2198", {"start": v(-30.18, -0.78) * mm, "end": v(-29.9, -0.93) * mm});
            skLineSegment(sketch, "E2199", {"start": v(-29.9, -0.93) * mm, "end": v(-29.6, -1.07) * mm});
            skLineSegment(sketch, "E2200", {"start": v(-29.6, -1.07) * mm, "end": v(-29.32, -1.2) * mm});
            skLineSegment(sketch, "E2201", {"start": v(-29.32, -1.2) * mm, "end": v(-29.03, -1.33) * mm});
            skLineSegment(sketch, "E2202", {"start": v(-29.03, -1.33) * mm, "end": v(-28.75, -1.46) * mm});
            skLineSegment(sketch, "E2203", {"start": v(-28.75, -1.46) * mm, "end": v(-28.46, -1.58) * mm});
            skLineSegment(sketch, "E2204", {"start": v(-28.46, -1.58) * mm, "end": v(-28.17, -1.7) * mm});
            skLineSegment(sketch, "E2205", {"start": v(-28.17, -1.7) * mm, "end": v(-27.89, -1.8) * mm});
            skLineSegment(sketch, "E2206", {"start": v(-27.89, -1.8) * mm, "end": v(-27.6, -1.9) * mm});
            skLineSegment(sketch, "E2207", {"start": v(-27.6, -1.9) * mm, "end": v(-27.31, -2) * mm});
            skLineSegment(sketch, "E2208", {"start": v(-27.31, -2) * mm, "end": v(-27.02, -2.1) * mm});
            skLineSegment(sketch, "E2209", {"start": v(-27.02, -2.1) * mm, "end": v(-26.74, -2.19) * mm});
            skLineSegment(sketch, "E2210", {"start": v(-26.74, -2.19) * mm, "end": v(-26.45, -2.27) * mm});
            skLineSegment(sketch, "E2211", {"start": v(-26.45, -2.27) * mm, "end": v(-26.16, -2.35) * mm});
            skLineSegment(sketch, "E2212", {"start": v(-26.16, -2.35) * mm, "end": v(-25.87, -2.43) * mm});
            skLineSegment(sketch, "E2213", {"start": v(-25.87, -2.43) * mm, "end": v(-25.59, -2.5) * mm});
            skLineSegment(sketch, "E2214", {"start": v(-25.59, -2.5) * mm, "end": v(-25.3, -2.56) * mm});
            skLineSegment(sketch, "E2215", {"start": v(-25.3, -2.56) * mm, "end": v(-25.01, -2.62) * mm});
            skLineSegment(sketch, "E2216", {"start": v(-25.01, -2.62) * mm, "end": v(-24.72, -2.67) * mm});
            skLineSegment(sketch, "E2217", {"start": v(-24.72, -2.67) * mm, "end": v(-24.43, -2.72) * mm});
            skLineSegment(sketch, "E2218", {"start": v(-24.43, -2.72) * mm, "end": v(-24.15, -2.76) * mm});
            skLineSegment(sketch, "E2219", {"start": v(-24.15, -2.76) * mm, "end": v(-23.86, -2.8) * mm});
            skLineSegment(sketch, "E2220", {"start": v(-23.86, -2.8) * mm, "end": v(-23.57, -2.84) * mm});
            skLineSegment(sketch, "E2221", {"start": v(-23.57, -2.84) * mm, "end": v(-23.28, -2.86) * mm});
            skLineSegment(sketch, "E2222", {"start": v(-23.28, -2.86) * mm, "end": v(-23, -2.89) * mm});
            skLineSegment(sketch, "E2223", {"start": v(-23, -2.89) * mm, "end": v(-22.7, -2.9) * mm});
            skLineSegment(sketch, "E2224", {"start": v(-22.7, -2.9) * mm, "end": v(-22.41, -2.92) * mm});
            skLineSegment(sketch, "E2225", {"start": v(-22.41, -2.92) * mm, "end": v(-22.12, -2.93) * mm});
            skLineSegment(sketch, "E2226", {"start": v(-22.12, -2.93) * mm, "end": v(-21.83, -2.93) * mm});
            skLineSegment(sketch, "E2227", {"start": v(-21.83, -2.93) * mm, "end": v(-21.54, -2.93) * mm});
            skLineSegment(sketch, "E2228", {"start": v(-2.87, -38.05) * mm, "end": v(-3.1, -37.52) * mm});
            skLineSegment(sketch, "E2229", {"start": v(-3.1, -37.52) * mm, "end": v(-3.31, -36.98) * mm});
            skLineSegment(sketch, "E2230", {"start": v(-3.31, -36.98) * mm, "end": v(-3.52, -36.44) * mm});
            skLineSegment(sketch, "E2231", {"start": v(-3.52, -36.44) * mm, "end": v(-3.72, -35.9) * mm});
            skLineSegment(sketch, "E2232", {"start": v(-3.72, -35.9) * mm, "end": v(-3.92, -35.37) * mm});
            skLineSegment(sketch, "E2233", {"start": v(-3.92, -35.37) * mm, "end": v(-4.1, -34.83) * mm});
            skLineSegment(sketch, "E2234", {"start": v(-4.1, -34.83) * mm, "end": v(-4.29, -34.29) * mm});
            skLineSegment(sketch, "E2235", {"start": v(-4.29, -34.29) * mm, "end": v(-4.46, -33.75) * mm});
            skLineSegment(sketch, "E2236", {"start": v(-4.46, -33.75) * mm, "end": v(-4.62, -33.2) * mm});
            skLineSegment(sketch, "E2237", {"start": v(-4.62, -33.2) * mm, "end": v(-4.78, -32.67) * mm});
            skLineSegment(sketch, "E2238", {"start": v(-4.78, -32.67) * mm, "end": v(-4.93, -32.12) * mm});
            skLineSegment(sketch, "E2239", {"start": v(-4.93, -32.12) * mm, "end": v(-5.07, -31.58) * mm});
            skLineSegment(sketch, "E2240", {"start": v(-5.07, -31.58) * mm, "end": v(-5.2, -31.04) * mm});
            skLineSegment(sketch, "E2241", {"start": v(-5.2, -31.04) * mm, "end": v(-5.34, -30.5) * mm});
            skLineSegment(sketch, "E2242", {"start": v(-5.34, -30.5) * mm, "end": v(-5.46, -29.95) * mm});
            skLineSegment(sketch, "E2243", {"start": v(-5.46, -29.95) * mm, "end": v(-5.57, -29.4) * mm});
            skLineSegment(sketch, "E2244", {"start": v(-5.57, -29.4) * mm, "end": v(-5.67, -28.86) * mm});
            skLineSegment(sketch, "E2245", {"start": v(-5.67, -28.86) * mm, "end": v(-5.77, -28.32) * mm});
            skLineSegment(sketch, "E2246", {"start": v(-5.77, -28.32) * mm, "end": v(-5.86, -27.77) * mm});
            skLineSegment(sketch, "E2247", {"start": v(-5.86, -27.77) * mm, "end": v(-5.94, -27.22) * mm});
            skLineSegment(sketch, "E2248", {"start": v(-5.94, -27.22) * mm, "end": v(-6.01, -26.68) * mm});
            skLineSegment(sketch, "E2249", {"start": v(-6.01, -26.68) * mm, "end": v(-6.08, -26.13) * mm});
            skLineSegment(sketch, "E2250", {"start": v(-6.08, -26.13) * mm, "end": v(-6.14, -25.58) * mm});
            skLineSegment(sketch, "E2251", {"start": v(-6.14, -25.58) * mm, "end": v(-6.19, -25.03) * mm});
            skLineSegment(sketch, "E2252", {"start": v(-6.19, -25.03) * mm, "end": v(-6.23, -24.48) * mm});
            skLineSegment(sketch, "E2253", {"start": v(-6.23, -24.48) * mm, "end": v(-6.27, -23.94) * mm});
            skLineSegment(sketch, "E2254", {"start": v(-6.27, -23.94) * mm, "end": v(-6.3, -23.39) * mm});
            skLineSegment(sketch, "E2255", {"start": v(-6.3, -23.39) * mm, "end": v(-6.31, -22.84) * mm});
            skLineSegment(sketch, "E2256", {"start": v(-6.31, -22.84) * mm, "end": v(-6.32, -22.28) * mm});
            skLineSegment(sketch, "E2257", {"start": v(-6.32, -22.28) * mm, "end": v(-6.33, -21.73) * mm});
            skLineSegment(sketch, "E2258", {"start": v(-6.33, -21.73) * mm, "end": v(-6.32, -21.19) * mm});
            skLineSegment(sketch, "E2259", {"start": v(-6.32, -21.19) * mm, "end": v(-6.31, -20.65) * mm});
            skLineSegment(sketch, "E2260", {"start": v(-6.31, -20.65) * mm, "end": v(-6.3, -20.1) * mm});
            skLineSegment(sketch, "E2261", {"start": v(-6.3, -20.1) * mm, "end": v(-6.27, -19.56) * mm});
            skLineSegment(sketch, "E2262", {"start": v(-6.27, -19.56) * mm, "end": v(-6.23, -19.02) * mm});
            skLineSegment(sketch, "E2263", {"start": v(-6.23, -19.02) * mm, "end": v(-6.2, -18.48) * mm});
            skLineSegment(sketch, "E2264", {"start": v(-6.2, -18.48) * mm, "end": v(-6.14, -17.94) * mm});
            skLineSegment(sketch, "E2265", {"start": v(-6.14, -17.94) * mm, "end": v(-6.09, -17.4) * mm});
            skLineSegment(sketch, "E2266", {"start": v(-6.09, -17.4) * mm, "end": v(-6.02, -16.86) * mm});
            skLineSegment(sketch, "E2267", {"start": v(-6.02, -16.86) * mm, "end": v(-5.95, -16.32) * mm});
            skLineSegment(sketch, "E2268", {"start": v(-5.95, -16.32) * mm, "end": v(-5.87, -15.78) * mm});
            skLineSegment(sketch, "E2269", {"start": v(-5.87, -15.78) * mm, "end": v(-5.78, -15.24) * mm});
            skLineSegment(sketch, "E2270", {"start": v(-5.78, -15.24) * mm, "end": v(-5.7, -14.7) * mm});
            skLineSegment(sketch, "E2271", {"start": v(-5.7, -14.7) * mm, "end": v(-5.59, -14.17) * mm});
            skLineSegment(sketch, "E2272", {"start": v(-5.59, -14.17) * mm, "end": v(-5.48, -13.63) * mm});
            skLineSegment(sketch, "E2273", {"start": v(-5.48, -13.63) * mm, "end": v(-5.36, -13.1) * mm});
            skLineSegment(sketch, "E2274", {"start": v(-5.36, -13.1) * mm, "end": v(-5.24, -12.56) * mm});
            skLineSegment(sketch, "E2275", {"start": v(-5.24, -12.56) * mm, "end": v(-5.1, -12.02) * mm});
            skLineSegment(sketch, "E2276", {"start": v(-5.1, -12.02) * mm, "end": v(-4.97, -11.49) * mm});
            skLineSegment(sketch, "E2277", {"start": v(-4.97, -11.49) * mm, "end": v(-4.83, -10.95) * mm});
            skLineSegment(sketch, "E2278", {"start": v(-4.83, -10.95) * mm, "end": v(-4.67, -10.42) * mm});
            skLineSegment(sketch, "E2279", {"start": v(-4.67, -10.42) * mm, "end": v(-4.51, -9.89) * mm});
            skLineSegment(sketch, "E2280", {"start": v(-4.51, -9.89) * mm, "end": v(-4.34, -9.35) * mm});
            skLineSegment(sketch, "E2281", {"start": v(-4.34, -9.35) * mm, "end": v(-4.17, -8.82) * mm});
            skLineSegment(sketch, "E2282", {"start": v(-4.17, -8.82) * mm, "end": v(-3.99, -8.29) * mm});
            skLineSegment(sketch, "E2283", {"start": v(-3.99, -8.29) * mm, "end": v(-3.8, -7.76) * mm});
            skLineSegment(sketch, "E2284", {"start": v(-3.8, -7.76) * mm, "end": v(-3.6, -7.23) * mm});
            skLineSegment(sketch, "E2285", {"start": v(-3.6, -7.23) * mm, "end": v(-3.4, -6.7) * mm});
            skLineSegment(sketch, "E2286", {"start": v(-3.4, -6.7) * mm, "end": v(-3.18, -6.17) * mm});
            skLineSegment(sketch, "E2287", {"start": v(-3.18, -6.17) * mm, "end": v(-2.97, -5.64) * mm});
            skLineSegment(sketch, "E2288", {"start": v(-2.97, -5.64) * mm, "end": v(-2.74, -5.11) * mm});
            skLineSegment(sketch, "E2289", {"start": v(-2.74, -5.11) * mm, "end": v(-2.6, -4.81) * mm});
            skLineSegment(sketch, "E2290", {"start": v(-2.6, -4.81) * mm, "end": v(-2.64, -4.8) * mm});
            skLineSegment(sketch, "E2291", {"start": v(-2.64, -4.8) * mm, "end": v(-2.93, -4.62) * mm});
            skLineSegment(sketch, "E2292", {"start": v(-2.93, -4.62) * mm, "end": v(-3.22, -4.43) * mm});
            skLineSegment(sketch, "E2293", {"start": v(-3.22, -4.43) * mm, "end": v(-3.49, -4.22) * mm});
            skLineSegment(sketch, "E2294", {"start": v(-3.49, -4.22) * mm, "end": v(-3.75, -3.99) * mm});
            skLineSegment(sketch, "E2295", {"start": v(-3.75, -3.99) * mm, "end": v(-3.99, -3.75) * mm});
            skLineSegment(sketch, "E2296", {"start": v(-3.99, -3.75) * mm, "end": v(-4.22, -3.49) * mm});
            skLineSegment(sketch, "E2297", {"start": v(-4.22, -3.49) * mm, "end": v(-4.43, -3.22) * mm});
            skLineSegment(sketch, "E2298", {"start": v(-4.43, -3.22) * mm, "end": v(-4.62, -2.93) * mm});
            skLineSegment(sketch, "E2299", {"start": v(-4.62, -2.93) * mm, "end": v(-4.8, -2.64) * mm});
            skLineSegment(sketch, "E2300", {"start": v(-4.8, -2.64) * mm, "end": v(-4.94, -2.35) * mm});
            skLineSegment(sketch, "E2301", {"start": v(-4.94, -2.35) * mm, "end": v(-5.11, -2.43) * mm});
            skLineSegment(sketch, "E2302", {"start": v(-5.11, -2.43) * mm, "end": v(-5.64, -2.7) * mm});
            skLineSegment(sketch, "E2303", {"start": v(-5.64, -2.7) * mm, "end": v(-6.17, -2.95) * mm});
            skLineSegment(sketch, "E2304", {"start": v(-6.17, -2.95) * mm, "end": v(-6.7, -3.2) * mm});
            skLineSegment(sketch, "E2305", {"start": v(-6.7, -3.2) * mm, "end": v(-7.23, -3.43) * mm});
            skLineSegment(sketch, "E2306", {"start": v(-7.23, -3.43) * mm, "end": v(-7.76, -3.66) * mm});
            skLineSegment(sketch, "E2307", {"start": v(-7.76, -3.66) * mm, "end": v(-8.29, -3.88) * mm});
            skLineSegment(sketch, "E2308", {"start": v(-8.29, -3.88) * mm, "end": v(-8.82, -4.1) * mm});
            skLineSegment(sketch, "E2309", {"start": v(-8.82, -4.1) * mm, "end": v(-9.35, -4.3) * mm});
            skLineSegment(sketch, "E2310", {"start": v(-9.35, -4.3) * mm, "end": v(-9.89, -4.5) * mm});
            skLineSegment(sketch, "E2311", {"start": v(-9.89, -4.5) * mm, "end": v(-10.42, -4.68) * mm});
            skLineSegment(sketch, "E2312", {"start": v(-10.42, -4.68) * mm, "end": v(-10.95, -4.86) * mm});
            skLineSegment(sketch, "E2313", {"start": v(-10.95, -4.86) * mm, "end": v(-11.49, -5.03) * mm});
            skLineSegment(sketch, "E2314", {"start": v(-11.49, -5.03) * mm, "end": v(-12.02, -5.2) * mm});
            skLineSegment(sketch, "E2315", {"start": v(-12.02, -5.2) * mm, "end": v(-12.56, -5.34) * mm});
            skLineSegment(sketch, "E2316", {"start": v(-12.56, -5.34) * mm, "end": v(-13.1, -5.49) * mm});
            skLineSegment(sketch, "E2317", {"start": v(-13.1, -5.49) * mm, "end": v(-13.63, -5.62) * mm});
            skLineSegment(sketch, "E2318", {"start": v(-13.63, -5.62) * mm, "end": v(-14.17, -5.75) * mm});
            skLineSegment(sketch, "E2319", {"start": v(-14.17, -5.75) * mm, "end": v(-14.7, -5.87) * mm});
            skLineSegment(sketch, "E2320", {"start": v(-14.7, -5.87) * mm, "end": v(-15.24, -5.98) * mm});
            skLineSegment(sketch, "E2321", {"start": v(-15.24, -5.98) * mm, "end": v(-15.78, -6.08) * mm});
            skLineSegment(sketch, "E2322", {"start": v(-15.78, -6.08) * mm, "end": v(-16.32, -6.17) * mm});
            skLineSegment(sketch, "E2323", {"start": v(-16.32, -6.17) * mm, "end": v(-16.86, -6.25) * mm});
            skLineSegment(sketch, "E2324", {"start": v(-16.86, -6.25) * mm, "end": v(-17.4, -6.33) * mm});
            skLineSegment(sketch, "E2325", {"start": v(-17.4, -6.33) * mm, "end": v(-17.94, -6.4) * mm});
            skLineSegment(sketch, "E2326", {"start": v(-17.94, -6.4) * mm, "end": v(-18.48, -6.45) * mm});
            skLineSegment(sketch, "E2327", {"start": v(-18.48, -6.45) * mm, "end": v(-19.02, -6.5) * mm});
            skLineSegment(sketch, "E2328", {"start": v(-19.02, -6.5) * mm, "end": v(-19.56, -6.54) * mm});
            skLineSegment(sketch, "E2329", {"start": v(-19.56, -6.54) * mm, "end": v(-20.1, -6.57) * mm});
            skLineSegment(sketch, "E2330", {"start": v(-20.1, -6.57) * mm, "end": v(-20.65, -6.6) * mm});
            skLineSegment(sketch, "E2331", {"start": v(-20.65, -6.6) * mm, "end": v(-21.19, -6.6) * mm});
            skLineSegment(sketch, "E2332", {"start": v(-21.19, -6.6) * mm, "end": v(-21.73, -6.6) * mm});
            skLineSegment(sketch, "E2333", {"start": v(-21.73, -6.6) * mm, "end": v(-22.28, -6.6) * mm});
            skLineSegment(sketch, "E2334", {"start": v(-22.28, -6.6) * mm, "end": v(-22.84, -6.6) * mm});
            skLineSegment(sketch, "E2335", {"start": v(-22.84, -6.6) * mm, "end": v(-23.39, -6.57) * mm});
            skLineSegment(sketch, "E2336", {"start": v(-23.39, -6.57) * mm, "end": v(-23.94, -6.54) * mm});
            skLineSegment(sketch, "E2337", {"start": v(-23.94, -6.54) * mm, "end": v(-24.48, -6.5) * mm});
            skLineSegment(sketch, "E2338", {"start": v(-24.48, -6.5) * mm, "end": v(-25.03, -6.45) * mm});
            skLineSegment(sketch, "E2339", {"start": v(-25.03, -6.45) * mm, "end": v(-25.58, -6.39) * mm});
            skLineSegment(sketch, "E2340", {"start": v(-25.58, -6.39) * mm, "end": v(-26.13, -6.32) * mm});
            skLineSegment(sketch, "E2341", {"start": v(-26.13, -6.32) * mm, "end": v(-26.68, -6.24) * mm});
            skLineSegment(sketch, "E2342", {"start": v(-26.68, -6.24) * mm, "end": v(-27.22, -6.16) * mm});
            skLineSegment(sketch, "E2343", {"start": v(-27.22, -6.16) * mm, "end": v(-27.77, -6.06) * mm});
            skLineSegment(sketch, "E2344", {"start": v(-27.77, -6.06) * mm, "end": v(-28.32, -5.96) * mm});
            skLineSegment(sketch, "E2345", {"start": v(-28.32, -5.96) * mm, "end": v(-28.86, -5.85) * mm});
            skLineSegment(sketch, "E2346", {"start": v(-28.86, -5.85) * mm, "end": v(-29.4, -5.72) * mm});
            skLineSegment(sketch, "E2347", {"start": v(-29.4, -5.72) * mm, "end": v(-29.95, -5.6) * mm});
            skLineSegment(sketch, "E2348", {"start": v(-29.95, -5.6) * mm, "end": v(-30.5, -5.45) * mm});
            skLineSegment(sketch, "E2349", {"start": v(-30.5, -5.45) * mm, "end": v(-31.04, -5.3) * mm});
            skLineSegment(sketch, "E2350", {"start": v(-31.04, -5.3) * mm, "end": v(-31.58, -5.15) * mm});
            skLineSegment(sketch, "E2351", {"start": v(-31.58, -5.15) * mm, "end": v(-32.12, -4.98) * mm});
            skLineSegment(sketch, "E2352", {"start": v(-32.12, -4.98) * mm, "end": v(-32.67, -4.8) * mm});
            skLineSegment(sketch, "E2353", {"start": v(-32.67, -4.8) * mm, "end": v(-33.2, -4.63) * mm});
            skLineSegment(sketch, "E2354", {"start": v(-33.2, -4.63) * mm, "end": v(-33.75, -4.43) * mm});
            skLineSegment(sketch, "E2355", {"start": v(-33.75, -4.43) * mm, "end": v(-34.29, -4.23) * mm});
            skLineSegment(sketch, "E2356", {"start": v(-34.29, -4.23) * mm, "end": v(-34.83, -4.02) * mm});
            skLineSegment(sketch, "E2357", {"start": v(-34.83, -4.02) * mm, "end": v(-35.37, -3.8) * mm});
            skLineSegment(sketch, "E2358", {"start": v(-35.37, -3.8) * mm, "end": v(-35.9, -3.58) * mm});
            skLineSegment(sketch, "E2359", {"start": v(-35.9, -3.58) * mm, "end": v(-36.44, -3.34) * mm});
            skLineSegment(sketch, "E2360", {"start": v(-36.44, -3.34) * mm, "end": v(-36.98, -3.1) * mm});
            skLineSegment(sketch, "E2361", {"start": v(-36.98, -3.1) * mm, "end": v(-37.52, -2.85) * mm});
            skLineSegment(sketch, "E2362", {"start": v(-37.52, -2.85) * mm, "end": v(-38.05, -2.58) * mm});
            skLineSegment(sketch, "E2363", {"start": v(-38.05, -2.58) * mm, "end": v(-38.38, -2.42) * mm});
            skLineSegment(sketch, "E2364", {"start": v(-38.38, -2.42) * mm, "end": v(-38.15, -4.82) * mm});
            skLineSegment(sketch, "E2365", {"start": v(-38.15, -4.82) * mm, "end": v(-37.78, -7.2) * mm});
            skLineSegment(sketch, "E2366", {"start": v(-37.78, -7.2) * mm, "end": v(-37.25, -9.56) * mm});
            skLineSegment(sketch, "E2367", {"start": v(-37.25, -9.56) * mm, "end": v(-36.58, -11.88) * mm});
            skLineSegment(sketch, "E2368", {"start": v(-36.58, -11.88) * mm, "end": v(-35.76, -14.16) * mm});
            skLineSegment(sketch, "E2369", {"start": v(-35.76, -14.16) * mm, "end": v(-34.8, -16.37) * mm});
            skLineSegment(sketch, "E2370", {"start": v(-34.8, -16.37) * mm, "end": v(-33.7, -18.53) * mm});
            skLineSegment(sketch, "E2371", {"start": v(-33.7, -18.53) * mm, "end": v(-32.47, -20.6) * mm});
            skLineSegment(sketch, "E2372", {"start": v(-32.47, -20.6) * mm, "end": v(-31.11, -22.6) * mm});
            skLineSegment(sketch, "E2373", {"start": v(-31.11, -22.6) * mm, "end": v(-29.63, -24.51) * mm});
            skLineSegment(sketch, "E2374", {"start": v(-29.63, -24.51) * mm, "end": v(-28.03, -26.33) * mm});
            skLineSegment(sketch, "E2375", {"start": v(-28.03, -26.33) * mm, "end": v(-26.33, -28.03) * mm});
            skLineSegment(sketch, "E2376", {"start": v(-26.33, -28.03) * mm, "end": v(-24.51, -29.63) * mm});
            skLineSegment(sketch, "E2377", {"start": v(-24.51, -29.63) * mm, "end": v(-22.6, -31.11) * mm});
            skLineSegment(sketch, "E2378", {"start": v(-22.6, -31.11) * mm, "end": v(-20.6, -32.47) * mm});
            skLineSegment(sketch, "E2379", {"start": v(-20.6, -32.47) * mm, "end": v(-18.53, -33.7) * mm});
            skLineSegment(sketch, "E2380", {"start": v(-18.53, -33.7) * mm, "end": v(-16.37, -34.8) * mm});
            skLineSegment(sketch, "E2381", {"start": v(-16.37, -34.8) * mm, "end": v(-14.16, -35.76) * mm});
            skLineSegment(sketch, "E2382", {"start": v(-14.16, -35.76) * mm, "end": v(-11.88, -36.58) * mm});
            skLineSegment(sketch, "E2383", {"start": v(-11.88, -36.58) * mm, "end": v(-9.56, -37.25) * mm});
            skLineSegment(sketch, "E2384", {"start": v(-9.56, -37.25) * mm, "end": v(-7.2, -37.78) * mm});
            skLineSegment(sketch, "E2385", {"start": v(-7.2, -37.78) * mm, "end": v(-4.82, -38.15) * mm});
            skLineSegment(sketch, "E2386", {"start": v(-4.82, -38.15) * mm, "end": v(-2.74, -38.35) * mm});
            skLineSegment(sketch, "E2387", {"start": v(-2.74, -38.35) * mm, "end": v(-2.87, -38.05) * mm});
            skLineSegment(sketch, "E2388", {"start": v(4.82, -38.15) * mm, "end": v(7.2, -37.78) * mm});
            skLineSegment(sketch, "E2389", {"start": v(7.2, -37.78) * mm, "end": v(9.56, -37.25) * mm});
            skLineSegment(sketch, "E2390", {"start": v(9.56, -37.25) * mm, "end": v(11.88, -36.58) * mm});
            skLineSegment(sketch, "E2391", {"start": v(11.88, -36.58) * mm, "end": v(14.16, -35.76) * mm});
            skLineSegment(sketch, "E2392", {"start": v(14.16, -35.76) * mm, "end": v(16.37, -34.8) * mm});
            skLineSegment(sketch, "E2393", {"start": v(16.37, -34.8) * mm, "end": v(18.53, -33.7) * mm});
            skLineSegment(sketch, "E2394", {"start": v(18.53, -33.7) * mm, "end": v(20.6, -32.47) * mm});
            skLineSegment(sketch, "E2395", {"start": v(20.6, -32.47) * mm, "end": v(22.6, -31.11) * mm});
            skLineSegment(sketch, "E2396", {"start": v(22.6, -31.11) * mm, "end": v(24.51, -29.63) * mm});
            skLineSegment(sketch, "E2397", {"start": v(24.51, -29.63) * mm, "end": v(26.33, -28.03) * mm});
            skLineSegment(sketch, "E2398", {"start": v(26.33, -28.03) * mm, "end": v(28.03, -26.33) * mm});
            skLineSegment(sketch, "E2399", {"start": v(28.03, -26.33) * mm, "end": v(29.63, -24.51) * mm});
            skLineSegment(sketch, "E2400", {"start": v(29.63, -24.51) * mm, "end": v(31.11, -22.6) * mm});
            skLineSegment(sketch, "E2401", {"start": v(31.11, -22.6) * mm, "end": v(32.47, -20.6) * mm});
            skLineSegment(sketch, "E2402", {"start": v(32.47, -20.6) * mm, "end": v(33.7, -18.53) * mm});
            skLineSegment(sketch, "E2403", {"start": v(33.7, -18.53) * mm, "end": v(34.8, -16.37) * mm});
            skLineSegment(sketch, "E2404", {"start": v(34.8, -16.37) * mm, "end": v(35.76, -14.16) * mm});
            skLineSegment(sketch, "E2405", {"start": v(35.76, -14.16) * mm, "end": v(36.58, -11.88) * mm});
            skLineSegment(sketch, "E2406", {"start": v(36.58, -11.88) * mm, "end": v(37.25, -9.56) * mm});
            skLineSegment(sketch, "E2407", {"start": v(37.25, -9.56) * mm, "end": v(37.78, -7.2) * mm});
            skLineSegment(sketch, "E2408", {"start": v(37.78, -7.2) * mm, "end": v(38.15, -4.82) * mm});
            skLineSegment(sketch, "E2409", {"start": v(38.15, -4.82) * mm, "end": v(38.35, -2.74) * mm});
            skLineSegment(sketch, "E2410", {"start": v(38.35, -2.74) * mm, "end": v(38.05, -2.87) * mm});
            skLineSegment(sketch, "E2411", {"start": v(38.05, -2.87) * mm, "end": v(37.52, -3.1) * mm});
            skLineSegment(sketch, "E2412", {"start": v(37.52, -3.1) * mm, "end": v(36.98, -3.31) * mm});
            skLineSegment(sketch, "E2413", {"start": v(36.98, -3.31) * mm, "end": v(36.44, -3.52) * mm});
            skLineSegment(sketch, "E2414", {"start": v(36.44, -3.52) * mm, "end": v(35.9, -3.72) * mm});
            skLineSegment(sketch, "E2415", {"start": v(35.9, -3.72) * mm, "end": v(35.37, -3.92) * mm});
            skLineSegment(sketch, "E2416", {"start": v(35.37, -3.92) * mm, "end": v(34.83, -4.1) * mm});
            skLineSegment(sketch, "E2417", {"start": v(34.83, -4.1) * mm, "end": v(34.29, -4.29) * mm});
            skLineSegment(sketch, "E2418", {"start": v(34.29, -4.29) * mm, "end": v(33.75, -4.46) * mm});
            skLineSegment(sketch, "E2419", {"start": v(33.75, -4.46) * mm, "end": v(33.2, -4.62) * mm});
            skLineSegment(sketch, "E2420", {"start": v(33.2, -4.62) * mm, "end": v(32.67, -4.78) * mm});
            skLineSegment(sketch, "E2421", {"start": v(32.67, -4.78) * mm, "end": v(32.12, -4.93) * mm});
            skLineSegment(sketch, "E2422", {"start": v(32.12, -4.93) * mm, "end": v(31.58, -5.07) * mm});
            skLineSegment(sketch, "E2423", {"start": v(31.58, -5.07) * mm, "end": v(31.04, -5.2) * mm});
            skLineSegment(sketch, "E2424", {"start": v(31.04, -5.2) * mm, "end": v(30.5, -5.34) * mm});
            skLineSegment(sketch, "E2425", {"start": v(30.5, -5.34) * mm, "end": v(29.95, -5.46) * mm});
            skLineSegment(sketch, "E2426", {"start": v(29.95, -5.46) * mm, "end": v(29.4, -5.57) * mm});
            skLineSegment(sketch, "E2427", {"start": v(29.4, -5.57) * mm, "end": v(28.86, -5.67) * mm});
            skLineSegment(sketch, "E2428", {"start": v(28.86, -5.67) * mm, "end": v(28.32, -5.77) * mm});
            skLineSegment(sketch, "E2429", {"start": v(28.32, -5.77) * mm, "end": v(27.77, -5.86) * mm});
            skLineSegment(sketch, "E2430", {"start": v(27.77, -5.86) * mm, "end": v(27.22, -5.94) * mm});
            skLineSegment(sketch, "E2431", {"start": v(27.22, -5.94) * mm, "end": v(26.68, -6.01) * mm});
            skLineSegment(sketch, "E2432", {"start": v(26.68, -6.01) * mm, "end": v(26.13, -6.08) * mm});
            skLineSegment(sketch, "E2433", {"start": v(26.13, -6.08) * mm, "end": v(25.58, -6.14) * mm});
            skLineSegment(sketch, "E2434", {"start": v(25.58, -6.14) * mm, "end": v(25.03, -6.19) * mm});
            skLineSegment(sketch, "E2435", {"start": v(25.03, -6.19) * mm, "end": v(24.48, -6.23) * mm});
            skLineSegment(sketch, "E2436", {"start": v(24.48, -6.23) * mm, "end": v(23.94, -6.27) * mm});
            skLineSegment(sketch, "E2437", {"start": v(23.94, -6.27) * mm, "end": v(23.39, -6.3) * mm});
            skLineSegment(sketch, "E2438", {"start": v(23.39, -6.3) * mm, "end": v(22.84, -6.31) * mm});
            skLineSegment(sketch, "E2439", {"start": v(22.84, -6.31) * mm, "end": v(22.28, -6.32) * mm});
            skLineSegment(sketch, "E2440", {"start": v(22.28, -6.32) * mm, "end": v(21.73, -6.33) * mm});
            skLineSegment(sketch, "E2441", {"start": v(21.73, -6.33) * mm, "end": v(21.19, -6.32) * mm});
            skLineSegment(sketch, "E2442", {"start": v(21.19, -6.32) * mm, "end": v(20.65, -6.31) * mm});
            skLineSegment(sketch, "E2443", {"start": v(20.65, -6.31) * mm, "end": v(20.1, -6.3) * mm});
            skLineSegment(sketch, "E2444", {"start": v(20.1, -6.3) * mm, "end": v(19.56, -6.27) * mm});
            skLineSegment(sketch, "E2445", {"start": v(19.56, -6.27) * mm, "end": v(19.02, -6.23) * mm});
            skLineSegment(sketch, "E2446", {"start": v(19.02, -6.23) * mm, "end": v(18.48, -6.2) * mm});
            skLineSegment(sketch, "E2447", {"start": v(18.48, -6.2) * mm, "end": v(17.94, -6.14) * mm});
            skLineSegment(sketch, "E2448", {"start": v(17.94, -6.14) * mm, "end": v(17.4, -6.09) * mm});
            skLineSegment(sketch, "E2449", {"start": v(17.4, -6.09) * mm, "end": v(16.86, -6.02) * mm});
            skLineSegment(sketch, "E2450", {"start": v(16.86, -6.02) * mm, "end": v(16.32, -5.95) * mm});
            skLineSegment(sketch, "E2451", {"start": v(16.32, -5.95) * mm, "end": v(15.78, -5.87) * mm});
            skLineSegment(sketch, "E2452", {"start": v(15.78, -5.87) * mm, "end": v(15.24, -5.78) * mm});
            skLineSegment(sketch, "E2453", {"start": v(15.24, -5.78) * mm, "end": v(14.7, -5.7) * mm});
            skLineSegment(sketch, "E2454", {"start": v(14.7, -5.7) * mm, "end": v(14.17, -5.59) * mm});
            skLineSegment(sketch, "E2455", {"start": v(14.17, -5.59) * mm, "end": v(13.63, -5.48) * mm});
            skLineSegment(sketch, "E2456", {"start": v(13.63, -5.48) * mm, "end": v(13.1, -5.36) * mm});
            skLineSegment(sketch, "E2457", {"start": v(13.1, -5.36) * mm, "end": v(12.56, -5.24) * mm});
            skLineSegment(sketch, "E2458", {"start": v(12.56, -5.24) * mm, "end": v(12.02, -5.1) * mm});
            skLineSegment(sketch, "E2459", {"start": v(12.02, -5.1) * mm, "end": v(11.49, -4.97) * mm});
            skLineSegment(sketch, "E2460", {"start": v(11.49, -4.97) * mm, "end": v(10.95, -4.83) * mm});
            skLineSegment(sketch, "E2461", {"start": v(10.95, -4.83) * mm, "end": v(10.42, -4.67) * mm});
            skLineSegment(sketch, "E2462", {"start": v(10.42, -4.67) * mm, "end": v(9.89, -4.51) * mm});
            skLineSegment(sketch, "E2463", {"start": v(9.89, -4.51) * mm, "end": v(9.35, -4.34) * mm});
            skLineSegment(sketch, "E2464", {"start": v(9.35, -4.34) * mm, "end": v(8.82, -4.17) * mm});
            skLineSegment(sketch, "E2465", {"start": v(8.82, -4.17) * mm, "end": v(8.29, -3.99) * mm});
            skLineSegment(sketch, "E2466", {"start": v(8.29, -3.99) * mm, "end": v(7.76, -3.8) * mm});
            skLineSegment(sketch, "E2467", {"start": v(7.76, -3.8) * mm, "end": v(7.23, -3.6) * mm});
            skLineSegment(sketch, "E2468", {"start": v(7.23, -3.6) * mm, "end": v(6.7, -3.4) * mm});
            skLineSegment(sketch, "E2469", {"start": v(6.7, -3.4) * mm, "end": v(6.17, -3.18) * mm});
            skLineSegment(sketch, "E2470", {"start": v(6.17, -3.18) * mm, "end": v(5.64, -2.97) * mm});
            skLineSegment(sketch, "E2471", {"start": v(5.64, -2.97) * mm, "end": v(5.11, -2.74) * mm});
            skLineSegment(sketch, "E2472", {"start": v(5.11, -2.74) * mm, "end": v(4.81, -2.6) * mm});
            skLineSegment(sketch, "E2473", {"start": v(4.81, -2.6) * mm, "end": v(4.8, -2.64) * mm});
            skLineSegment(sketch, "E2474", {"start": v(4.8, -2.64) * mm, "end": v(4.62, -2.93) * mm});
            skLineSegment(sketch, "E2475", {"start": v(4.62, -2.93) * mm, "end": v(4.43, -3.22) * mm});
            skLineSegment(sketch, "E2476", {"start": v(4.43, -3.22) * mm, "end": v(4.22, -3.49) * mm});
            skLineSegment(sketch, "E2477", {"start": v(4.22, -3.49) * mm, "end": v(3.99, -3.75) * mm});
            skLineSegment(sketch, "E2478", {"start": v(3.99, -3.75) * mm, "end": v(3.75, -3.99) * mm});
            skLineSegment(sketch, "E2479", {"start": v(3.75, -3.99) * mm, "end": v(3.49, -4.22) * mm});
            skLineSegment(sketch, "E2480", {"start": v(3.49, -4.22) * mm, "end": v(3.22, -4.43) * mm});
            skLineSegment(sketch, "E2481", {"start": v(3.22, -4.43) * mm, "end": v(2.93, -4.62) * mm});
            skLineSegment(sketch, "E2482", {"start": v(2.93, -4.62) * mm, "end": v(2.64, -4.8) * mm});
            skLineSegment(sketch, "E2483", {"start": v(2.64, -4.8) * mm, "end": v(2.35, -4.94) * mm});
            skLineSegment(sketch, "E2484", {"start": v(2.35, -4.94) * mm, "end": v(2.43, -5.11) * mm});
            skLineSegment(sketch, "E2485", {"start": v(2.43, -5.11) * mm, "end": v(2.7, -5.64) * mm});
            skLineSegment(sketch, "E2486", {"start": v(2.7, -5.64) * mm, "end": v(2.95, -6.17) * mm});
            skLineSegment(sketch, "E2487", {"start": v(2.95, -6.17) * mm, "end": v(3.2, -6.7) * mm});
            skLineSegment(sketch, "E2488", {"start": v(3.2, -6.7) * mm, "end": v(3.43, -7.23) * mm});
            skLineSegment(sketch, "E2489", {"start": v(3.43, -7.23) * mm, "end": v(3.66, -7.76) * mm});
            skLineSegment(sketch, "E2490", {"start": v(3.66, -7.76) * mm, "end": v(3.88, -8.29) * mm});
            skLineSegment(sketch, "E2491", {"start": v(3.88, -8.29) * mm, "end": v(4.1, -8.82) * mm});
            skLineSegment(sketch, "E2492", {"start": v(4.1, -8.82) * mm, "end": v(4.3, -9.35) * mm});
            skLineSegment(sketch, "E2493", {"start": v(4.3, -9.35) * mm, "end": v(4.5, -9.89) * mm});
            skLineSegment(sketch, "E2494", {"start": v(4.5, -9.89) * mm, "end": v(4.68, -10.42) * mm});
            skLineSegment(sketch, "E2495", {"start": v(4.68, -10.42) * mm, "end": v(4.86, -10.95) * mm});
            skLineSegment(sketch, "E2496", {"start": v(4.86, -10.95) * mm, "end": v(5.03, -11.49) * mm});
            skLineSegment(sketch, "E2497", {"start": v(5.03, -11.49) * mm, "end": v(5.2, -12.02) * mm});
            skLineSegment(sketch, "E2498", {"start": v(5.2, -12.02) * mm, "end": v(5.34, -12.56) * mm});
            skLineSegment(sketch, "E2499", {"start": v(5.34, -12.56) * mm, "end": v(5.49, -13.1) * mm});
            skLineSegment(sketch, "E2500", {"start": v(5.49, -13.1) * mm, "end": v(5.62, -13.63) * mm});
            skLineSegment(sketch, "E2501", {"start": v(5.62, -13.63) * mm, "end": v(5.75, -14.17) * mm});
            skLineSegment(sketch, "E2502", {"start": v(5.75, -14.17) * mm, "end": v(5.87, -14.7) * mm});
            skLineSegment(sketch, "E2503", {"start": v(5.87, -14.7) * mm, "end": v(5.98, -15.24) * mm});
            skLineSegment(sketch, "E2504", {"start": v(5.98, -15.24) * mm, "end": v(6.08, -15.78) * mm});
            skLineSegment(sketch, "E2505", {"start": v(6.08, -15.78) * mm, "end": v(6.17, -16.32) * mm});
            skLineSegment(sketch, "E2506", {"start": v(6.17, -16.32) * mm, "end": v(6.25, -16.86) * mm});
            skLineSegment(sketch, "E2507", {"start": v(6.25, -16.86) * mm, "end": v(6.33, -17.4) * mm});
            skLineSegment(sketch, "E2508", {"start": v(6.33, -17.4) * mm, "end": v(6.4, -17.94) * mm});
            skLineSegment(sketch, "E2509", {"start": v(6.4, -17.94) * mm, "end": v(6.45, -18.48) * mm});
            skLineSegment(sketch, "E2510", {"start": v(6.45, -18.48) * mm, "end": v(6.5, -19.02) * mm});
            skLineSegment(sketch, "E2511", {"start": v(6.5, -19.02) * mm, "end": v(6.54, -19.56) * mm});
            skLineSegment(sketch, "E2512", {"start": v(6.54, -19.56) * mm, "end": v(6.57, -20.1) * mm});
            skLineSegment(sketch, "E2513", {"start": v(6.57, -20.1) * mm, "end": v(6.6, -20.65) * mm});
            skLineSegment(sketch, "E2514", {"start": v(6.6, -20.65) * mm, "end": v(6.6, -21.19) * mm});
            skLineSegment(sketch, "E2515", {"start": v(6.6, -21.19) * mm, "end": v(6.6, -21.73) * mm});
            skLineSegment(sketch, "E2516", {"start": v(6.6, -21.73) * mm, "end": v(6.6, -22.28) * mm});
            skLineSegment(sketch, "E2517", {"start": v(6.6, -22.28) * mm, "end": v(6.6, -22.84) * mm});
            skLineSegment(sketch, "E2518", {"start": v(6.6, -22.84) * mm, "end": v(6.57, -23.39) * mm});
            skLineSegment(sketch, "E2519", {"start": v(6.57, -23.39) * mm, "end": v(6.54, -23.94) * mm});
            skLineSegment(sketch, "E2520", {"start": v(6.54, -23.94) * mm, "end": v(6.5, -24.48) * mm});
            skLineSegment(sketch, "E2521", {"start": v(6.5, -24.48) * mm, "end": v(6.45, -25.03) * mm});
            skLineSegment(sketch, "E2522", {"start": v(6.45, -25.03) * mm, "end": v(6.39, -25.58) * mm});
            skLineSegment(sketch, "E2523", {"start": v(6.39, -25.58) * mm, "end": v(6.32, -26.13) * mm});
            skLineSegment(sketch, "E2524", {"start": v(6.32, -26.13) * mm, "end": v(6.24, -26.68) * mm});
            skLineSegment(sketch, "E2525", {"start": v(6.24, -26.68) * mm, "end": v(6.16, -27.22) * mm});
            skLineSegment(sketch, "E2526", {"start": v(6.16, -27.22) * mm, "end": v(6.06, -27.77) * mm});
            skLineSegment(sketch, "E2527", {"start": v(6.06, -27.77) * mm, "end": v(5.96, -28.32) * mm});
            skLineSegment(sketch, "E2528", {"start": v(5.96, -28.32) * mm, "end": v(5.85, -28.86) * mm});
            skLineSegment(sketch, "E2529", {"start": v(5.85, -28.86) * mm, "end": v(5.72, -29.4) * mm});
            skLineSegment(sketch, "E2530", {"start": v(5.72, -29.4) * mm, "end": v(5.6, -29.95) * mm});
            skLineSegment(sketch, "E2531", {"start": v(5.6, -29.95) * mm, "end": v(5.45, -30.5) * mm});
            skLineSegment(sketch, "E2532", {"start": v(5.45, -30.5) * mm, "end": v(5.3, -31.04) * mm});
            skLineSegment(sketch, "E2533", {"start": v(5.3, -31.04) * mm, "end": v(5.15, -31.58) * mm});
            skLineSegment(sketch, "E2534", {"start": v(5.15, -31.58) * mm, "end": v(4.98, -32.12) * mm});
            skLineSegment(sketch, "E2535", {"start": v(4.98, -32.12) * mm, "end": v(4.8, -32.67) * mm});
            skLineSegment(sketch, "E2536", {"start": v(4.8, -32.67) * mm, "end": v(4.63, -33.2) * mm});
            skLineSegment(sketch, "E2537", {"start": v(4.63, -33.2) * mm, "end": v(4.43, -33.75) * mm});
            skLineSegment(sketch, "E2538", {"start": v(4.43, -33.75) * mm, "end": v(4.23, -34.29) * mm});
            skLineSegment(sketch, "E2539", {"start": v(4.23, -34.29) * mm, "end": v(4.02, -34.83) * mm});
            skLineSegment(sketch, "E2540", {"start": v(4.02, -34.83) * mm, "end": v(3.8, -35.37) * mm});
            skLineSegment(sketch, "E2541", {"start": v(3.8, -35.37) * mm, "end": v(3.58, -35.9) * mm});
            skLineSegment(sketch, "E2542", {"start": v(3.58, -35.9) * mm, "end": v(3.34, -36.44) * mm});
            skLineSegment(sketch, "E2543", {"start": v(3.34, -36.44) * mm, "end": v(3.1, -36.98) * mm});
            skLineSegment(sketch, "E2544", {"start": v(3.1, -36.98) * mm, "end": v(2.85, -37.52) * mm});
            skLineSegment(sketch, "E2545", {"start": v(2.85, -37.52) * mm, "end": v(2.58, -38.05) * mm});
            skLineSegment(sketch, "E2546", {"start": v(2.58, -38.05) * mm, "end": v(2.42, -38.38) * mm});
            skLineSegment(sketch, "E2547", {"start": v(2.42, -38.38) * mm, "end": v(4.82, -38.15) * mm});
            skLineSegment(sketch, "E2548", {"start": v(0.63, -30.46) * mm, "end": v(0.78, -30.18) * mm});
            skLineSegment(sketch, "E2549", {"start": v(0.78, -30.18) * mm, "end": v(0.93, -29.9) * mm});
            skLineSegment(sketch, "E2550", {"start": v(0.93, -29.9) * mm, "end": v(1.07, -29.6) * mm});
            skLineSegment(sketch, "E2551", {"start": v(1.07, -29.6) * mm, "end": v(1.2, -29.32) * mm});
            skLineSegment(sketch, "E2552", {"start": v(1.2, -29.32) * mm, "end": v(1.33, -29.03) * mm});
            skLineSegment(sketch, "E2553", {"start": v(1.33, -29.03) * mm, "end": v(1.46, -28.75) * mm});
            skLineSegment(sketch, "E2554", {"start": v(1.46, -28.75) * mm, "end": v(1.58, -28.46) * mm});
            skLineSegment(sketch, "E2555", {"start": v(1.58, -28.46) * mm, "end": v(1.7, -28.17) * mm});
            skLineSegment(sketch, "E2556", {"start": v(1.7, -28.17) * mm, "end": v(1.8, -27.89) * mm});
            skLineSegment(sketch, "E2557", {"start": v(1.8, -27.89) * mm, "end": v(1.9, -27.6) * mm});
            skLineSegment(sketch, "E2558", {"start": v(1.9, -27.6) * mm, "end": v(2, -27.31) * mm});
            skLineSegment(sketch, "E2559", {"start": v(2, -27.31) * mm, "end": v(2.1, -27.02) * mm});
            skLineSegment(sketch, "E2560", {"start": v(2.1, -27.02) * mm, "end": v(2.19, -26.74) * mm});
            skLineSegment(sketch, "E2561", {"start": v(2.19, -26.74) * mm, "end": v(2.27, -26.45) * mm});
            skLineSegment(sketch, "E2562", {"start": v(2.27, -26.45) * mm, "end": v(2.35, -26.16) * mm});
            skLineSegment(sketch, "E2563", {"start": v(2.35, -26.16) * mm, "end": v(2.43, -25.87) * mm});
            skLineSegment(sketch, "E2564", {"start": v(2.43, -25.87) * mm, "end": v(2.5, -25.59) * mm});
            skLineSegment(sketch, "E2565", {"start": v(2.5, -25.59) * mm, "end": v(2.56, -25.3) * mm});
            skLineSegment(sketch, "E2566", {"start": v(2.56, -25.3) * mm, "end": v(2.62, -25.01) * mm});
            skLineSegment(sketch, "E2567", {"start": v(2.62, -25.01) * mm, "end": v(2.67, -24.72) * mm});
            skLineSegment(sketch, "E2568", {"start": v(2.67, -24.72) * mm, "end": v(2.72, -24.43) * mm});
            skLineSegment(sketch, "E2569", {"start": v(2.72, -24.43) * mm, "end": v(2.76, -24.15) * mm});
            skLineSegment(sketch, "E2570", {"start": v(2.76, -24.15) * mm, "end": v(2.8, -23.86) * mm});
            skLineSegment(sketch, "E2571", {"start": v(2.8, -23.86) * mm, "end": v(2.84, -23.57) * mm});
            skLineSegment(sketch, "E2572", {"start": v(2.84, -23.57) * mm, "end": v(2.86, -23.28) * mm});
            skLineSegment(sketch, "E2573", {"start": v(2.86, -23.28) * mm, "end": v(2.89, -23) * mm});
            skLineSegment(sketch, "E2574", {"start": v(2.89, -23) * mm, "end": v(2.9, -22.7) * mm});
            skLineSegment(sketch, "E2575", {"start": v(2.9, -22.7) * mm, "end": v(2.92, -22.41) * mm});
            skLineSegment(sketch, "E2576", {"start": v(2.92, -22.41) * mm, "end": v(2.93, -22.12) * mm});
            skLineSegment(sketch, "E2577", {"start": v(2.93, -22.12) * mm, "end": v(2.93, -21.83) * mm});
            skLineSegment(sketch, "E2578", {"start": v(2.93, -21.83) * mm, "end": v(2.93, -21.54) * mm});
            skLineSegment(sketch, "E2579", {"start": v(2.93, -21.54) * mm, "end": v(2.92, -21.26) * mm});
            skLineSegment(sketch, "E2580", {"start": v(2.92, -21.26) * mm, "end": v(2.9, -20.97) * mm});
            skLineSegment(sketch, "E2581", {"start": v(2.9, -20.97) * mm, "end": v(2.89, -20.69) * mm});
            skLineSegment(sketch, "E2582", {"start": v(2.89, -20.69) * mm, "end": v(2.87, -20.4) * mm});
            skLineSegment(sketch, "E2583", {"start": v(2.87, -20.4) * mm, "end": v(2.84, -20.12) * mm});
            skLineSegment(sketch, "E2584", {"start": v(2.84, -20.12) * mm, "end": v(2.8, -19.83) * mm});
            skLineSegment(sketch, "E2585", {"start": v(2.8, -19.83) * mm, "end": v(2.77, -19.55) * mm});
            skLineSegment(sketch, "E2586", {"start": v(2.77, -19.55) * mm, "end": v(2.73, -19.26) * mm});
            skLineSegment(sketch, "E2587", {"start": v(2.73, -19.26) * mm, "end": v(2.68, -18.98) * mm});
            skLineSegment(sketch, "E2588", {"start": v(2.68, -18.98) * mm, "end": v(2.63, -18.7) * mm});
            skLineSegment(sketch, "E2589", {"start": v(2.63, -18.7) * mm, "end": v(2.57, -18.41) * mm});
            skLineSegment(sketch, "E2590", {"start": v(2.57, -18.41) * mm, "end": v(2.5, -18.13) * mm});
            skLineSegment(sketch, "E2591", {"start": v(2.5, -18.13) * mm, "end": v(2.44, -17.84) * mm});
            skLineSegment(sketch, "E2592", {"start": v(2.44, -17.84) * mm, "end": v(2.37, -17.56) * mm});
            skLineSegment(sketch, "E2593", {"start": v(2.37, -17.56) * mm, "end": v(2.3, -17.28) * mm});
            skLineSegment(sketch, "E2594", {"start": v(2.3, -17.28) * mm, "end": v(2.2, -17) * mm});
            skLineSegment(sketch, "E2595", {"start": v(2.2, -17) * mm, "end": v(2.12, -16.7) * mm});
            skLineSegment(sketch, "E2596", {"start": v(2.12, -16.7) * mm, "end": v(2.03, -16.43) * mm});
            skLineSegment(sketch, "E2597", {"start": v(2.03, -16.43) * mm, "end": v(1.93, -16.14) * mm});
            skLineSegment(sketch, "E2598", {"start": v(1.93, -16.14) * mm, "end": v(1.83, -15.86) * mm});
            skLineSegment(sketch, "E2599", {"start": v(1.83, -15.86) * mm, "end": v(1.73, -15.58) * mm});
            skLineSegment(sketch, "E2600", {"start": v(1.73, -15.58) * mm, "end": v(1.61, -15.3) * mm});
            skLineSegment(sketch, "E2601", {"start": v(1.61, -15.3) * mm, "end": v(1.5, -15.01) * mm});
            skLineSegment(sketch, "E2602", {"start": v(1.5, -15.01) * mm, "end": v(1.38, -14.73) * mm});
            skLineSegment(sketch, "E2603", {"start": v(1.38, -14.73) * mm, "end": v(1.25, -14.45) * mm});
            skLineSegment(sketch, "E2604", {"start": v(1.25, -14.45) * mm, "end": v(1.12, -14.17) * mm});
            skLineSegment(sketch, "E2605", {"start": v(1.12, -14.17) * mm, "end": v(0.98, -13.88) * mm});
            skLineSegment(sketch, "E2606", {"start": v(0.98, -13.88) * mm, "end": v(0.84, -13.6) * mm});
            skLineSegment(sketch, "E2607", {"start": v(0.84, -13.6) * mm, "end": v(0.7, -13.32) * mm});
            skLineSegment(sketch, "E2608", {"start": v(0.7, -13.32) * mm, "end": v(0.66, -13.25) * mm});
            skLineSegment(sketch, "E2609", {"start": v(0.66, -13.25) * mm, "end": v(-0.87, -13.25) * mm});
            skLineSegment(sketch, "E2610", {"start": v(-0.87, -13.25) * mm, "end": v(-0.88, -13.27) * mm});
            skLineSegment(sketch, "E2611", {"start": v(-0.88, -13.27) * mm, "end": v(-1, -13.55) * mm});
            skLineSegment(sketch, "E2612", {"start": v(-1, -13.55) * mm, "end": v(-1.13, -13.84) * mm});
            skLineSegment(sketch, "E2613", {"start": v(-1.13, -13.84) * mm, "end": v(-1.24, -14.12) * mm});
            skLineSegment(sketch, "E2614", {"start": v(-1.24, -14.12) * mm, "end": v(-1.36, -14.4) * mm});
            skLineSegment(sketch, "E2615", {"start": v(-1.36, -14.4) * mm, "end": v(-1.46, -14.69) * mm});
            skLineSegment(sketch, "E2616", {"start": v(-1.46, -14.69) * mm, "end": v(-1.57, -14.97) * mm});
            skLineSegment(sketch, "E2617", {"start": v(-1.57, -14.97) * mm, "end": v(-1.67, -15.25) * mm});
            skLineSegment(sketch, "E2618", {"start": v(-1.67, -15.25) * mm, "end": v(-1.77, -15.54) * mm});
            skLineSegment(sketch, "E2619", {"start": v(-1.77, -15.54) * mm, "end": v(-1.86, -15.82) * mm});
            skLineSegment(sketch, "E2620", {"start": v(-1.86, -15.82) * mm, "end": v(-1.95, -16.1) * mm});
            skLineSegment(sketch, "E2621", {"start": v(-1.95, -16.1) * mm, "end": v(-2.03, -16.4) * mm});
            skLineSegment(sketch, "E2622", {"start": v(-2.03, -16.4) * mm, "end": v(-2.1, -16.68) * mm});
            skLineSegment(sketch, "E2623", {"start": v(-2.1, -16.68) * mm, "end": v(-2.18, -16.96) * mm});
            skLineSegment(sketch, "E2624", {"start": v(-2.18, -16.96) * mm, "end": v(-2.25, -17.24) * mm});
            skLineSegment(sketch, "E2625", {"start": v(-2.25, -17.24) * mm, "end": v(-2.32, -17.53) * mm});
            skLineSegment(sketch, "E2626", {"start": v(-2.32, -17.53) * mm, "end": v(-2.38, -17.82) * mm});
            skLineSegment(sketch, "E2627", {"start": v(-2.38, -17.82) * mm, "end": v(-2.44, -18.1) * mm});
            skLineSegment(sketch, "E2628", {"start": v(-2.44, -18.1) * mm, "end": v(-2.5, -18.39) * mm});
            skLineSegment(sketch, "E2629", {"start": v(-2.5, -18.39) * mm, "end": v(-2.54, -18.67) * mm});
            skLineSegment(sketch, "E2630", {"start": v(-2.54, -18.67) * mm, "end": v(-2.59, -18.96) * mm});
            skLineSegment(sketch, "E2631", {"start": v(-2.59, -18.96) * mm, "end": v(-2.63, -19.24) * mm});
            skLineSegment(sketch, "E2632", {"start": v(-2.63, -19.24) * mm, "end": v(-2.67, -19.53) * mm});
            skLineSegment(sketch, "E2633", {"start": v(-2.67, -19.53) * mm, "end": v(-2.7, -19.82) * mm});
            skLineSegment(sketch, "E2634", {"start": v(-2.7, -19.82) * mm, "end": v(-2.73, -20.1) * mm});
            skLineSegment(sketch, "E2635", {"start": v(-2.73, -20.1) * mm, "end": v(-2.75, -20.4) * mm});
            skLineSegment(sketch, "E2636", {"start": v(-2.75, -20.4) * mm, "end": v(-2.77, -20.68) * mm});
            skLineSegment(sketch, "E2637", {"start": v(-2.77, -20.68) * mm, "end": v(-2.79, -20.97) * mm});
            skLineSegment(sketch, "E2638", {"start": v(-2.79, -20.97) * mm, "end": v(-2.8, -21.25) * mm});
            skLineSegment(sketch, "E2639", {"start": v(-2.8, -21.25) * mm, "end": v(-2.8, -21.54) * mm});
            skLineSegment(sketch, "E2640", {"start": v(-2.8, -21.54) * mm, "end": v(-2.8, -21.83) * mm});
            skLineSegment(sketch, "E2641", {"start": v(-2.8, -21.83) * mm, "end": v(-2.8, -22.12) * mm});
            skLineSegment(sketch, "E2642", {"start": v(-2.8, -22.12) * mm, "end": v(-2.8, -22.42) * mm});
            skLineSegment(sketch, "E2643", {"start": v(-2.8, -22.42) * mm, "end": v(-2.79, -22.7) * mm});
            skLineSegment(sketch, "E2644", {"start": v(-2.79, -22.7) * mm, "end": v(-2.77, -23) * mm});
            skLineSegment(sketch, "E2645", {"start": v(-2.77, -23) * mm, "end": v(-2.75, -23.3) * mm});
            skLineSegment(sketch, "E2646", {"start": v(-2.75, -23.3) * mm, "end": v(-2.73, -23.58) * mm});
            skLineSegment(sketch, "E2647", {"start": v(-2.73, -23.58) * mm, "end": v(-2.7, -23.87) * mm});
            skLineSegment(sketch, "E2648", {"start": v(-2.7, -23.87) * mm, "end": v(-2.66, -24.16) * mm});
            skLineSegment(sketch, "E2649", {"start": v(-2.66, -24.16) * mm, "end": v(-2.63, -24.45) * mm});
            skLineSegment(sketch, "E2650", {"start": v(-2.63, -24.45) * mm, "end": v(-2.58, -24.74) * mm});
            skLineSegment(sketch, "E2651", {"start": v(-2.58, -24.74) * mm, "end": v(-2.54, -25.03) * mm});
            skLineSegment(sketch, "E2652", {"start": v(-2.54, -25.03) * mm, "end": v(-2.49, -25.32) * mm});
            skLineSegment(sketch, "E2653", {"start": v(-2.49, -25.32) * mm, "end": v(-2.43, -25.61) * mm});
            skLineSegment(sketch, "E2654", {"start": v(-2.43, -25.61) * mm, "end": v(-2.37, -25.9) * mm});
            skLineSegment(sketch, "E2655", {"start": v(-2.37, -25.9) * mm, "end": v(-2.3, -26.2) * mm});
            skLineSegment(sketch, "E2656", {"start": v(-2.3, -26.2) * mm, "end": v(-2.24, -26.48) * mm});
            skLineSegment(sketch, "E2657", {"start": v(-2.24, -26.48) * mm, "end": v(-2.17, -26.77) * mm});
            skLineSegment(sketch, "E2658", {"start": v(-2.17, -26.77) * mm, "end": v(-2.09, -27.06) * mm});
            skLineSegment(sketch, "E2659", {"start": v(-2.09, -27.06) * mm, "end": v(-2, -27.35) * mm});
            skLineSegment(sketch, "E2660", {"start": v(-2, -27.35) * mm, "end": v(-1.92, -27.64) * mm});
            skLineSegment(sketch, "E2661", {"start": v(-1.92, -27.64) * mm, "end": v(-1.83, -27.92) * mm});
            skLineSegment(sketch, "E2662", {"start": v(-1.83, -27.92) * mm, "end": v(-1.74, -28.21) * mm});
            skLineSegment(sketch, "E2663", {"start": v(-1.74, -28.21) * mm, "end": v(-1.64, -28.5) * mm});
            skLineSegment(sketch, "E2664", {"start": v(-1.64, -28.5) * mm, "end": v(-1.53, -28.79) * mm});
            skLineSegment(sketch, "E2665", {"start": v(-1.53, -28.79) * mm, "end": v(-1.43, -29.08) * mm});
            skLineSegment(sketch, "E2666", {"start": v(-1.43, -29.08) * mm, "end": v(-1.31, -29.36) * mm});
            skLineSegment(sketch, "E2667", {"start": v(-1.31, -29.36) * mm, "end": v(-1.2, -29.65) * mm});
            skLineSegment(sketch, "E2668", {"start": v(-1.2, -29.65) * mm, "end": v(-1.08, -29.94) * mm});
            skLineSegment(sketch, "E2669", {"start": v(-1.08, -29.94) * mm, "end": v(-0.95, -30.22) * mm});
            skLineSegment(sketch, "E2670", {"start": v(-0.95, -30.22) * mm, "end": v(-0.82, -30.51) * mm});
            skLineSegment(sketch, "E2671", {"start": v(-0.82, -30.51) * mm, "end": v(-0.8, -30.55) * mm});
            skLineSegment(sketch, "E2672", {"start": v(-0.8, -30.55) * mm, "end": v(0.59, -30.55) * mm});
            skLineSegment(sketch, "E2673", {"start": v(0.59, -30.55) * mm, "end": v(0.63, -30.46) * mm});
            skCircle(sketch, "E2674", {"center": v(0, 0.2) * mm, "radius": 1.5 * mm});
            skLineSegment(sketch, "E2675", {"start": v(0, 1.7) * mm, "end": v(0, -0.8) * mm, "construction": true});
            skLineSegment(sketch, "E2676", {"start": v(-1.12, -0.8) * mm, "end": v(1.12, -0.8) * mm});
            skSolve(sketch);
        }
        {
            var Q0;
            Q0=makeQuery(id+"F0.imprint","IMPRINT",FACE,{"disambiguationData":[TD([[makeQuery(id+"F0.imprint","IMPRINT",EDGE,{"derivedFrom":sQuery(id+"F0.wireOp",EDGE,"E0")}),1.0]])]});
            var Q1;
            {var subQ0=sQuery(id+"F0.wireOp",EDGE,"E2676");Q1=makeQuery(id+"F0.imprint","IMPRINT",FACE,{"disambiguationData":[TD([[makeQuery(id+"F0.imprint","IMPRINT",EDGE,{"derivedFrom":subQ0}),-1.0]])]});}
            extrude(context, id + "F1", {"entities" : qUnion([Q0, Q1]), "depth" : 5 * mm});
        }
    });
